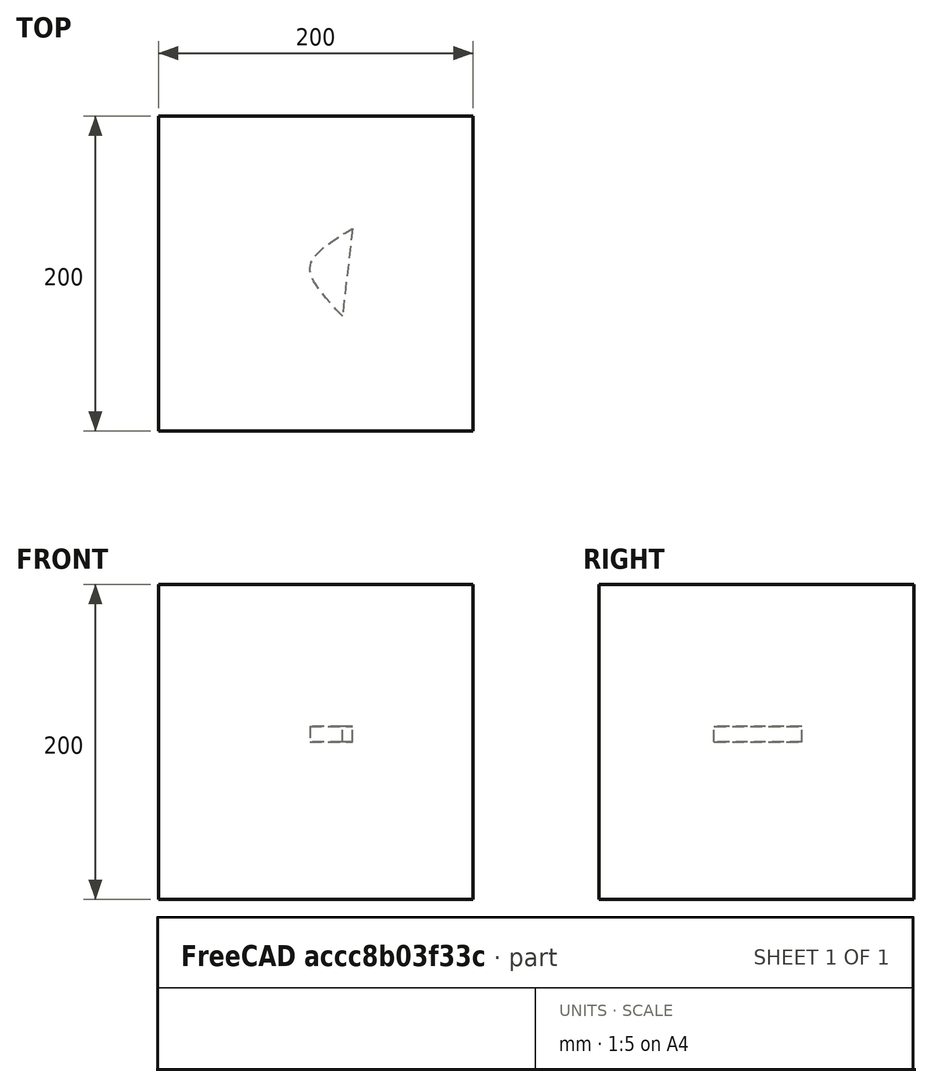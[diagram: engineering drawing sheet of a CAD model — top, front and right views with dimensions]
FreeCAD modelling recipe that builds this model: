
FCSTD DOCUMENT  (FreeCAD 0.21R33694 (Git))
Label: extrudedHyperbola
License: All rights reserved
LicenseURL: http://en.wikipedia.org/wiki/All_rights_reserved
objects: App::DocumentObjectGroupPython×1248, App::Part×2, Part::FeaturePython×1, Sketcher::SketchObject×1, Part::Extrusion×1
note: 3 computed .brp shape members not serialized (recipe doc carries the construction recipe); baked Part::Feature solids carry a one-line shape summary decoded from their .brp

FEATURE [App::DocumentObjectGroupPython] HALFPI  # scripted group (container) (typed FeaturePython)
  name = HALFPI
  value = pi/2.
FEATURE [App::DocumentObjectGroupPython] PI  # scripted group (container) (typed FeaturePython)
  name = PI
  value = 1.*pi
FEATURE [App::DocumentObjectGroupPython] TWOPI  # scripted group (container) (typed FeaturePython)
  name = TWOPI
  value = 2.*pi
FEATURE [App::DocumentObjectGroupPython] Constants  # scripted group (container) (typed FeaturePython)
  Group = -> [HALFPI,PI,TWOPI]
FEATURE [App::DocumentObjectGroupPython] Variables  # scripted group (container) (typed FeaturePython)
FEATURE [App::DocumentObjectGroupPython] Quantities  # scripted group (container) (typed FeaturePython)
FEATURE [App::DocumentObjectGroupPython] Isotopes  # scripted group (container) (typed FeaturePython)
FEATURE [App::DocumentObjectGroupPython] Elements  # scripted group (container) (typed FeaturePython)
FEATURE [App::DocumentObjectGroupPython] G4Isotopes  # scripted group (container) (typed FeaturePython)
FEATURE [App::DocumentObjectGroupPython] H_element  # scripted group (container) (typed FeaturePython)
  Z = 1
  atom_value = 1.008
  formula = H
  name = H_element
FEATURE [App::DocumentObjectGroupPython] He_element  # scripted group (container) (typed FeaturePython)
  Z = 2
  atom_value = 4.0026
  formula = He
  name = He_element
FEATURE [App::DocumentObjectGroupPython] Li_element  # scripted group (container) (typed FeaturePython)
  Z = 3
  atom_value = 6.94
  formula = Li
  name = Li_element
FEATURE [App::DocumentObjectGroupPython] Be_element  # scripted group (container) (typed FeaturePython)
  Z = 4
  atom_value = 9.01218
  formula = Be
  name = Be_element
FEATURE [App::DocumentObjectGroupPython] B_element  # scripted group (container) (typed FeaturePython)
  Z = 5
  atom_value = 10.81
  formula = B
  name = B_element
FEATURE [App::DocumentObjectGroupPython] C_element  # scripted group (container) (typed FeaturePython)
  Z = 6
  atom_value = 12.011
  formula = C
  name = C_element
FEATURE [App::DocumentObjectGroupPython] N_element  # scripted group (container) (typed FeaturePython)
  Z = 7
  atom_value = 14.007
  formula = N
  name = N_element
FEATURE [App::DocumentObjectGroupPython] O_element  # scripted group (container) (typed FeaturePython)
  Z = 8
  atom_value = 15.999
  formula = O
  name = O_element
FEATURE [App::DocumentObjectGroupPython] F_element  # scripted group (container) (typed FeaturePython)
  Z = 9
  atom_value = 18.9984
  formula = F
  name = F_element
FEATURE [App::DocumentObjectGroupPython] Ne_element  # scripted group (container) (typed FeaturePython)
  Z = 10
  atom_value = 20.1797
  formula = Ne
  name = Ne_element
FEATURE [App::DocumentObjectGroupPython] Na_element  # scripted group (container) (typed FeaturePython)
  Z = 11
  atom_value = 22.9898
  formula = Na
  name = Na_element
FEATURE [App::DocumentObjectGroupPython] Mg_element  # scripted group (container) (typed FeaturePython)
  Z = 12
  atom_value = 24.305
  formula = Mg
  name = Mg_element
FEATURE [App::DocumentObjectGroupPython] Al_element  # scripted group (container) (typed FeaturePython)
  Z = 13
  atom_value = 26.9815
  formula = Al
  name = Al_element
FEATURE [App::DocumentObjectGroupPython] Si_element  # scripted group (container) (typed FeaturePython)
  Z = 14
  atom_value = 28.085
  formula = Si
  name = Si_element
FEATURE [App::DocumentObjectGroupPython] P_element  # scripted group (container) (typed FeaturePython)
  Z = 15
  atom_value = 30.9738
  formula = P
  name = P_element
FEATURE [App::DocumentObjectGroupPython] S_element  # scripted group (container) (typed FeaturePython)
  Z = 16
  atom_value = 32.06
  formula = S
  name = S_element
FEATURE [App::DocumentObjectGroupPython] Cl_element  # scripted group (container) (typed FeaturePython)
  Z = 17
  atom_value = 35.45
  formula = Cl
  name = Cl_element
FEATURE [App::DocumentObjectGroupPython] Ar_element  # scripted group (container) (typed FeaturePython)
  Z = 18
  atom_value = 39.95
  formula = Ar
  name = Ar_element
FEATURE [App::DocumentObjectGroupPython] K_element  # scripted group (container) (typed FeaturePython)
  Z = 19
  atom_value = 39.0983
  formula = K
  name = K_element
FEATURE [App::DocumentObjectGroupPython] Ca_element  # scripted group (container) (typed FeaturePython)
  Z = 20
  atom_value = 40.078
  formula = Ca
  name = Ca_element
FEATURE [App::DocumentObjectGroupPython] Sc_element  # scripted group (container) (typed FeaturePython)
  Z = 21
  atom_value = 44.9559
  formula = Sc
  name = Sc_element
FEATURE [App::DocumentObjectGroupPython] Ti_element  # scripted group (container) (typed FeaturePython)
  Z = 22
  atom_value = 47.867
  formula = Ti
  name = Ti_element
FEATURE [App::DocumentObjectGroupPython] V_element  # scripted group (container) (typed FeaturePython)
  Z = 23
  atom_value = 50.9415
  formula = V
  name = V_element
FEATURE [App::DocumentObjectGroupPython] Cr_element  # scripted group (container) (typed FeaturePython)
  Z = 24
  atom_value = 51.9961
  formula = Cr
  name = Cr_element
FEATURE [App::DocumentObjectGroupPython] Mn_element  # scripted group (container) (typed FeaturePython)
  Z = 25
  atom_value = 54.938
  formula = Mn
  name = Mn_element
FEATURE [App::DocumentObjectGroupPython] Fe_element  # scripted group (container) (typed FeaturePython)
  Z = 26
  atom_value = 55.845
  formula = Fe
  name = Fe_element
FEATURE [App::DocumentObjectGroupPython] Co_element  # scripted group (container) (typed FeaturePython)
  Z = 27
  atom_value = 58.9332
  formula = Co
  name = Co_element
FEATURE [App::DocumentObjectGroupPython] Ni_element  # scripted group (container) (typed FeaturePython)
  Z = 28
  atom_value = 58.6934
  formula = Ni
  name = Ni_element
FEATURE [App::DocumentObjectGroupPython] Cu_element  # scripted group (container) (typed FeaturePython)
  Z = 29
  atom_value = 63.546
  formula = Cu
  name = Cu_element
FEATURE [App::DocumentObjectGroupPython] Zn_element  # scripted group (container) (typed FeaturePython)
  Z = 30
  atom_value = 65.38
  formula = Zn
  name = Zn_element
FEATURE [App::DocumentObjectGroupPython] Ga_element  # scripted group (container) (typed FeaturePython)
  Z = 31
  atom_value = 69.723
  formula = Ga
  name = Ga_element
FEATURE [App::DocumentObjectGroupPython] Ge_element  # scripted group (container) (typed FeaturePython)
  Z = 32
  atom_value = 72.63
  formula = Ge
  name = Ge_element
FEATURE [App::DocumentObjectGroupPython] As_element  # scripted group (container) (typed FeaturePython)
  Z = 33
  atom_value = 74.9216
  formula = As
  name = As_element
FEATURE [App::DocumentObjectGroupPython] Se_element  # scripted group (container) (typed FeaturePython)
  Z = 34
  atom_value = 78.971
  formula = Se
  name = Se_element
FEATURE [App::DocumentObjectGroupPython] Br_element  # scripted group (container) (typed FeaturePython)
  Z = 35
  atom_value = 79.904
  formula = Br
  name = Br_element
FEATURE [App::DocumentObjectGroupPython] Kr_element  # scripted group (container) (typed FeaturePython)
  Z = 36
  atom_value = 83.798
  formula = Kr
  name = Kr_element
FEATURE [App::DocumentObjectGroupPython] Rb_element  # scripted group (container) (typed FeaturePython)
  Z = 37
  atom_value = 85.4678
  formula = Rb
  name = Rb_element
FEATURE [App::DocumentObjectGroupPython] Sr_element  # scripted group (container) (typed FeaturePython)
  Z = 38
  atom_value = 87.62
  formula = Sr
  name = Sr_element
FEATURE [App::DocumentObjectGroupPython] Y_element  # scripted group (container) (typed FeaturePython)
  Z = 39
  atom_value = 88.9058
  formula = Y
  name = Y_element
FEATURE [App::DocumentObjectGroupPython] Zr_element  # scripted group (container) (typed FeaturePython)
  Z = 40
  atom_value = 91.224
  formula = Zr
  name = Zr_element
FEATURE [App::DocumentObjectGroupPython] Nb_element  # scripted group (container) (typed FeaturePython)
  Z = 41
  atom_value = 92.9064
  formula = Nb
  name = Nb_element
FEATURE [App::DocumentObjectGroupPython] Mo_element  # scripted group (container) (typed FeaturePython)
  Z = 42
  atom_value = 95.95
  formula = Mo
  name = Mo_element
FEATURE [App::DocumentObjectGroupPython] Tc_element  # scripted group (container) (typed FeaturePython)
  Z = 43
  atom_value = 97
  formula = Tc
  name = Tc_element
FEATURE [App::DocumentObjectGroupPython] Ru_element  # scripted group (container) (typed FeaturePython)
  Z = 44
  atom_value = 101.07
  formula = Ru
  name = Ru_element
FEATURE [App::DocumentObjectGroupPython] Rh_element  # scripted group (container) (typed FeaturePython)
  Z = 45
  atom_value = 102.905
  formula = Rh
  name = Rh_element
FEATURE [App::DocumentObjectGroupPython] Pd_element  # scripted group (container) (typed FeaturePython)
  Z = 46
  atom_value = 106.42
  formula = Pd
  name = Pd_element
FEATURE [App::DocumentObjectGroupPython] Ag_element  # scripted group (container) (typed FeaturePython)
  Z = 47
  atom_value = 107.868
  formula = Ag
  name = Ag_element
FEATURE [App::DocumentObjectGroupPython] Cd_element  # scripted group (container) (typed FeaturePython)
  Z = 48
  atom_value = 112.414
  formula = Cd
  name = Cd_element
FEATURE [App::DocumentObjectGroupPython] In_element  # scripted group (container) (typed FeaturePython)
  Z = 49
  atom_value = 114.818
  formula = In
  name = In_element
FEATURE [App::DocumentObjectGroupPython] Sn_element  # scripted group (container) (typed FeaturePython)
  Z = 50
  atom_value = 118.71
  formula = Sn
  name = Sn_element
FEATURE [App::DocumentObjectGroupPython] Sb_element  # scripted group (container) (typed FeaturePython)
  Z = 51
  atom_value = 121.76
  formula = Sb
  name = Sb_element
FEATURE [App::DocumentObjectGroupPython] Te_element  # scripted group (container) (typed FeaturePython)
  Z = 52
  atom_value = 127.6
  formula = Te
  name = Te_element
FEATURE [App::DocumentObjectGroupPython] I_element  # scripted group (container) (typed FeaturePython)
  Z = 53
  atom_value = 126.904
  formula = I
  name = I_element
FEATURE [App::DocumentObjectGroupPython] Xe_element  # scripted group (container) (typed FeaturePython)
  Z = 54
  atom_value = 131.293
  formula = Xe
  name = Xe_element
FEATURE [App::DocumentObjectGroupPython] Cs_element  # scripted group (container) (typed FeaturePython)
  Z = 55
  atom_value = 132.905
  formula = Cs
  name = Cs_element
FEATURE [App::DocumentObjectGroupPython] Ba_element  # scripted group (container) (typed FeaturePython)
  Z = 56
  atom_value = 137.327
  formula = Ba
  name = Ba_element
FEATURE [App::DocumentObjectGroupPython] La_element  # scripted group (container) (typed FeaturePython)
  Z = 57
  atom_value = 138.905
  formula = La
  name = La_element
FEATURE [App::DocumentObjectGroupPython] Ce_element  # scripted group (container) (typed FeaturePython)
  Z = 58
  atom_value = 140.116
  formula = Ce
  name = Ce_element
FEATURE [App::DocumentObjectGroupPython] Pr_element  # scripted group (container) (typed FeaturePython)
  Z = 59
  atom_value = 140.908
  formula = Pr
  name = Pr_element
FEATURE [App::DocumentObjectGroupPython] Nd_element  # scripted group (container) (typed FeaturePython)
  Z = 60
  atom_value = 144.242
  formula = Nd
  name = Nd_element
FEATURE [App::DocumentObjectGroupPython] Pm_element  # scripted group (container) (typed FeaturePython)
  Z = 61
  atom_value = 145
  formula = Pm
  name = Pm_element
FEATURE [App::DocumentObjectGroupPython] Sm_element  # scripted group (container) (typed FeaturePython)
  Z = 62
  atom_value = 150.36
  formula = Sm
  name = Sm_element
FEATURE [App::DocumentObjectGroupPython] Eu_element  # scripted group (container) (typed FeaturePython)
  Z = 63
  atom_value = 151.964
  formula = Eu
  name = Eu_element
FEATURE [App::DocumentObjectGroupPython] Gd_element  # scripted group (container) (typed FeaturePython)
  Z = 64
  atom_value = 157.25
  formula = Gd
  name = Gd_element
FEATURE [App::DocumentObjectGroupPython] Tb_element  # scripted group (container) (typed FeaturePython)
  Z = 65
  atom_value = 158.925
  formula = Tb
  name = Tb_element
FEATURE [App::DocumentObjectGroupPython] Dy_element  # scripted group (container) (typed FeaturePython)
  Z = 66
  atom_value = 162.5
  formula = Dy
  name = Dy_element
FEATURE [App::DocumentObjectGroupPython] Ho_element  # scripted group (container) (typed FeaturePython)
  Z = 67
  atom_value = 164.93
  formula = Ho
  name = Ho_element
FEATURE [App::DocumentObjectGroupPython] Er_element  # scripted group (container) (typed FeaturePython)
  Z = 68
  atom_value = 167.259
  formula = Er
  name = Er_element
FEATURE [App::DocumentObjectGroupPython] Tm_element  # scripted group (container) (typed FeaturePython)
  Z = 69
  atom_value = 168.934
  formula = Tm
  name = Tm_element
FEATURE [App::DocumentObjectGroupPython] Yb_element  # scripted group (container) (typed FeaturePython)
  Z = 70
  atom_value = 173.045
  formula = Yb
  name = Yb_element
FEATURE [App::DocumentObjectGroupPython] Lu_element  # scripted group (container) (typed FeaturePython)
  Z = 71
  atom_value = 174.967
  formula = Lu
  name = Lu_element
FEATURE [App::DocumentObjectGroupPython] Hf_element  # scripted group (container) (typed FeaturePython)
  Z = 72
  atom_value = 178.49
  formula = Hf
  name = Hf_element
FEATURE [App::DocumentObjectGroupPython] Ta_element  # scripted group (container) (typed FeaturePython)
  Z = 73
  atom_value = 180.948
  formula = Ta
  name = Ta_element
FEATURE [App::DocumentObjectGroupPython] W_element  # scripted group (container) (typed FeaturePython)
  Z = 74
  atom_value = 183.84
  formula = W
  name = W_element
FEATURE [App::DocumentObjectGroupPython] Re_element  # scripted group (container) (typed FeaturePython)
  Z = 75
  atom_value = 186.207
  formula = Re
  name = Re_element
FEATURE [App::DocumentObjectGroupPython] Os_element  # scripted group (container) (typed FeaturePython)
  Z = 76
  atom_value = 190.23
  formula = Os
  name = Os_element
FEATURE [App::DocumentObjectGroupPython] Ir_element  # scripted group (container) (typed FeaturePython)
  Z = 77
  atom_value = 192.217
  formula = Ir
  name = Ir_element
FEATURE [App::DocumentObjectGroupPython] Pt_element  # scripted group (container) (typed FeaturePython)
  Z = 78
  atom_value = 195.084
  formula = Pt
  name = Pt_element
FEATURE [App::DocumentObjectGroupPython] Au_element  # scripted group (container) (typed FeaturePython)
  Z = 79
  atom_value = 196.967
  formula = Au
  name = Au_element
FEATURE [App::DocumentObjectGroupPython] Hg_element  # scripted group (container) (typed FeaturePython)
  Z = 80
  atom_value = 200.592
  formula = Hg
  name = Hg_element
FEATURE [App::DocumentObjectGroupPython] Tl_element  # scripted group (container) (typed FeaturePython)
  Z = 81
  atom_value = 204.38
  formula = Tl
  name = Tl_element
FEATURE [App::DocumentObjectGroupPython] Pb_element  # scripted group (container) (typed FeaturePython)
  Z = 82
  atom_value = 207.2
  formula = Pb
  name = Pb_element
FEATURE [App::DocumentObjectGroupPython] Bi_element  # scripted group (container) (typed FeaturePython)
  Z = 83
  atom_value = 208.98
  formula = Bi
  name = Bi_element
FEATURE [App::DocumentObjectGroupPython] Po_element  # scripted group (container) (typed FeaturePython)
  Z = 84
  atom_value = 209
  formula = Po
  name = Po_element
FEATURE [App::DocumentObjectGroupPython] At_element  # scripted group (container) (typed FeaturePython)
  Z = 85
  atom_value = 210
  formula = At
  name = At_element
FEATURE [App::DocumentObjectGroupPython] Rn_element  # scripted group (container) (typed FeaturePython)
  Z = 86
  atom_value = 222
  formula = Rn
  name = Rn_element
FEATURE [App::DocumentObjectGroupPython] Fr_element  # scripted group (container) (typed FeaturePython)
  Z = 87
  atom_value = 223
  formula = Fr
  name = Fr_element
FEATURE [App::DocumentObjectGroupPython] Ra_element  # scripted group (container) (typed FeaturePython)
  Z = 88
  atom_value = 226
  formula = Ra
  name = Ra_element
FEATURE [App::DocumentObjectGroupPython] Ac_element  # scripted group (container) (typed FeaturePython)
  Z = 89
  atom_value = 227
  formula = Ac
  name = Ac_element
FEATURE [App::DocumentObjectGroupPython] Th_element  # scripted group (container) (typed FeaturePython)
  Z = 90
  atom_value = 232.038
  formula = Th
  name = Th_element
FEATURE [App::DocumentObjectGroupPython] Pa_element  # scripted group (container) (typed FeaturePython)
  Z = 91
  atom_value = 231.036
  formula = Pa
  name = Pa_element
FEATURE [App::DocumentObjectGroupPython] U_element  # scripted group (container) (typed FeaturePython)
  Z = 92
  atom_value = 238.029
  formula = U
  name = U_element
FEATURE [App::DocumentObjectGroupPython] Np_element  # scripted group (container) (typed FeaturePython)
  Z = 93
  atom_value = 237
  formula = Np
  name = Np_element
FEATURE [App::DocumentObjectGroupPython] Pu_element  # scripted group (container) (typed FeaturePython)
  Z = 94
  atom_value = 244
  formula = Pu
  name = Pu_element
FEATURE [App::DocumentObjectGroupPython] Am_element  # scripted group (container) (typed FeaturePython)
  Z = 95
  atom_value = 243
  formula = Am
  name = Am_element
FEATURE [App::DocumentObjectGroupPython] Cm_element  # scripted group (container) (typed FeaturePython)
  Z = 96
  atom_value = 247
  formula = Cm
  name = Cm_element
FEATURE [App::DocumentObjectGroupPython] Bk_element  # scripted group (container) (typed FeaturePython)
  Z = 97
  atom_value = 247
  formula = Bk
  name = Bk_element
FEATURE [App::DocumentObjectGroupPython] Cf_element  # scripted group (container) (typed FeaturePython)
  Z = 98
  atom_value = 251
  formula = Cf
  name = Cf_element
FEATURE [App::DocumentObjectGroupPython] G4Elements  # scripted group (container) (typed FeaturePython)
  Group = -> [H_element,He_element,Li_element,Be_element,B_element,C_element,N_element,O_element,F_element,Ne_element,Na_element,Mg_element,Al_element,Si_element,P_element,S_element,Cl_element,Ar_element,K_element,Ca_element,Sc_element,Ti_element,V_element,Cr_element,Mn_element,Fe_element,Co_element,Ni_element,Cu_element,Zn_element,Ga_element,Ge_element,As_element,Se_element,Br_element,Kr_element,Rb_element,+61 more]
FEATURE [App::DocumentObjectGroupPython] H_element001  label="H_element : 0.101"  # scripted group (container) (typed FeaturePython)
  n = 0.101327
FEATURE [App::DocumentObjectGroupPython] C_element001  label="C_element : 0.775"  # scripted group (container) (typed FeaturePython)
  n = 0.7755
FEATURE [App::DocumentObjectGroupPython] N_element001  label="N_element : 0.035"  # scripted group (container) (typed FeaturePython)
  n = 0.035057
FEATURE [App::DocumentObjectGroupPython] O_element001  label="O_element : 0.052"  # scripted group (container) (typed FeaturePython)
  n = 0.0523159
FEATURE [App::DocumentObjectGroupPython] F_element001  label="F_element : 0.017"  # scripted group (container) (typed FeaturePython)
  n = 0.017422
FEATURE [App::DocumentObjectGroupPython] Ca_element001  label="Ca_element : 0.018"  # scripted group (container) (typed FeaturePython)
  n = 0.018378
FEATURE [App::DocumentObjectGroupPython] G4_A_150_TISSUE  label="G4_A-150_TISSUE"  # scripted group (container) (typed FeaturePython)
  Dunit = g/cm3
  Dvalue = 1.127
  Group = -> [H_element001,C_element001,N_element001,O_element001,F_element001,Ca_element001]
  conduct = 2
  density = 1
  expand = 3
  formula = G4_A-150_TISSUE
  name = G4_A-150_TISSUE
  specific = 4
FEATURE [App::DocumentObjectGroupPython] C_element002  label="C_element : 3"  # scripted group (container) (typed FeaturePython)
  n = 3
  ref = C_element
FEATURE [App::DocumentObjectGroupPython] H_element002  label="H_element : 6"  # scripted group (container) (typed FeaturePython)
  n = 6
  ref = H_element
FEATURE [App::DocumentObjectGroupPython] O_element002  label="O_element : 1"  # scripted group (container) (typed FeaturePython)
  n = 1
  ref = O_element
FEATURE [App::DocumentObjectGroupPython] G4_ACETONE  # scripted group (container) (typed FeaturePython)
  Dunit = g/cm3
  Dvalue = 0.7899
  Group = -> [C_element002,H_element002,O_element002]
  conduct = 2
  density = 1
  expand = 3
  formula = G4_ACETONE
  name = G4_ACETONE
  specific = 4
FEATURE [App::DocumentObjectGroupPython] C_element003  label="C_element : 2"  # scripted group (container) (typed FeaturePython)
  n = 2
  ref = C_element
FEATURE [App::DocumentObjectGroupPython] H_element003  label="H_element : 2"  # scripted group (container) (typed FeaturePython)
  n = 2
  ref = H_element
FEATURE [App::DocumentObjectGroupPython] G4_ACETYLENE  # scripted group (container) (typed FeaturePython)
  Dunit = g/cm3
  Dvalue = 0.0010967
  Group = -> [C_element003,H_element003]
  conduct = 2
  density = 1
  expand = 3
  formula = G4_ACETYLENE
  name = G4_ACETYLENE
  specific = 4
FEATURE [App::DocumentObjectGroupPython] C_element004  label="C_element : 5"  # scripted group (container) (typed FeaturePython)
  n = 5
  ref = C_element
FEATURE [App::DocumentObjectGroupPython] H_element004  label="H_element : 5"  # scripted group (container) (typed FeaturePython)
  n = 5
  ref = H_element
FEATURE [App::DocumentObjectGroupPython] N_element002  label="N_element : 5"  # scripted group (container) (typed FeaturePython)
  n = 5
  ref = N_element
FEATURE [App::DocumentObjectGroupPython] G4_ADENINE  # scripted group (container) (typed FeaturePython)
  Dunit = g/cm3
  Dvalue = 1.6
  Group = -> [C_element004,H_element004,N_element002]
  conduct = 2
  density = 1
  expand = 3
  formula = G4_ADENINE
  name = G4_ADENINE
  specific = 4
FEATURE [App::DocumentObjectGroupPython] H_element005  label="H_element : 0.114"  # scripted group (container) (typed FeaturePython)
  n = 0.114
FEATURE [App::DocumentObjectGroupPython] C_element005  label="C_element : 0.598"  # scripted group (container) (typed FeaturePython)
  n = 0.598
FEATURE [App::DocumentObjectGroupPython] N_element003  label="N_element : 0.007"  # scripted group (container) (typed FeaturePython)
  n = 0.007
FEATURE [App::DocumentObjectGroupPython] O_element003  label="O_element : 0.278"  # scripted group (container) (typed FeaturePython)
  n = 0.278
FEATURE [App::DocumentObjectGroupPython] Na_element001  label="Na_element : 0.001"  # scripted group (container) (typed FeaturePython)
  n = 0.001
FEATURE [App::DocumentObjectGroupPython] S_element001  label="S_element : 0.001"  # scripted group (container) (typed FeaturePython)
  n = 0.001
FEATURE [App::DocumentObjectGroupPython] Cl_element001  label="Cl_element : 0.001"  # scripted group (container) (typed FeaturePython)
  n = 0.001
FEATURE [App::DocumentObjectGroupPython] G4_ADIPOSE_TISSUE_ICRP  # scripted group (container) (typed FeaturePython)
  Dunit = g/cm3
  Dvalue = 0.95
  Group = -> [H_element005,C_element005,N_element003,O_element003,Na_element001,S_element001,Cl_element001]
  conduct = 2
  density = 1
  expand = 3
  formula = G4_ADIPOSE_TISSUE_ICRP
  name = G4_ADIPOSE_TISSUE_ICRP
  specific = 4
FEATURE [App::DocumentObjectGroupPython] C_element006  label="C_element : 0.000"  # scripted group (container) (typed FeaturePython)
  n = 0.000124
FEATURE [App::DocumentObjectGroupPython] N_element004  label="N_element : 0.755"  # scripted group (container) (typed FeaturePython)
  n = 0.755268
FEATURE [App::DocumentObjectGroupPython] O_element004  label="O_element : 0.232"  # scripted group (container) (typed FeaturePython)
  n = 0.231781
FEATURE [App::DocumentObjectGroupPython] Ar_element001  label="Ar_element : 0.013"  # scripted group (container) (typed FeaturePython)
  n = 0.012827
FEATURE [App::DocumentObjectGroupPython] G4_AIR  # scripted group (container) (typed FeaturePython)
  Dunit = g/cm3
  Dvalue = 0.00120479
  Group = -> [C_element006,N_element004,O_element004,Ar_element001]
  conduct = 2
  density = 1
  expand = 3
  formula = G4_AIR
  name = G4_AIR
  specific = 4
FEATURE [App::DocumentObjectGroupPython] C_element007  label="C_element : 006"  # scripted group (container) (typed FeaturePython)
  n = 3
  ref = C_element
FEATURE [App::DocumentObjectGroupPython] H_element006  label="H_element : 7"  # scripted group (container) (typed FeaturePython)
  n = 7
  ref = H_element
FEATURE [App::DocumentObjectGroupPython] N_element005  label="N_element : 1"  # scripted group (container) (typed FeaturePython)
  n = 1
  ref = N_element
FEATURE [App::DocumentObjectGroupPython] O_element005  label="O_element : 2"  # scripted group (container) (typed FeaturePython)
  n = 2
  ref = O_element
FEATURE [App::DocumentObjectGroupPython] G4_ALANINE  # scripted group (container) (typed FeaturePython)
  Dunit = g/cm3
  Dvalue = 1.42
  Group = -> [C_element007,H_element006,N_element005,O_element005]
  conduct = 2
  density = 1
  expand = 3
  formula = G4_ALANINE
  name = G4_ALANINE
  specific = 4
FEATURE [App::DocumentObjectGroupPython] Al_element001  label="Al_element : 2"  # scripted group (container) (typed FeaturePython)
  n = 2
  ref = Al_element
FEATURE [App::DocumentObjectGroupPython] O_element006  label="O_element : 3"  # scripted group (container) (typed FeaturePython)
  n = 3
  ref = O_element
FEATURE [App::DocumentObjectGroupPython] G4_ALUMINUM_OXIDE  # scripted group (container) (typed FeaturePython)
  Dunit = g/cm3
  Dvalue = 3.97
  Group = -> [Al_element001,O_element006]
  conduct = 2
  density = 1
  expand = 3
  formula = G4_ALUMINUM_OXIDE
  name = G4_ALUMINUM_OXIDE
  specific = 4
FEATURE [App::DocumentObjectGroupPython] H_element007  label="H_element : 0.106"  # scripted group (container) (typed FeaturePython)
  n = 0.10593
FEATURE [App::DocumentObjectGroupPython] C_element008  label="C_element : 0.789"  # scripted group (container) (typed FeaturePython)
  n = 0.788974
FEATURE [App::DocumentObjectGroupPython] O_element007  label="O_element : 0.105"  # scripted group (container) (typed FeaturePython)
  n = 0.105096
FEATURE [App::DocumentObjectGroupPython] G4_AMBER  # scripted group (container) (typed FeaturePython)
  Dunit = g/cm3
  Dvalue = 1.1
  Group = -> [H_element007,C_element008,O_element007]
  conduct = 2
  density = 1
  expand = 3
  formula = G4_AMBER
  name = G4_AMBER
  specific = 4
FEATURE [App::DocumentObjectGroupPython] N_element006  label="N_element : 006"  # scripted group (container) (typed FeaturePython)
  n = 1
  ref = N_element
FEATURE [App::DocumentObjectGroupPython] H_element008  label="H_element : 3"  # scripted group (container) (typed FeaturePython)
  n = 3
  ref = H_element
FEATURE [App::DocumentObjectGroupPython] G4_AMMONIA  # scripted group (container) (typed FeaturePython)
  Dunit = g/cm3
  Dvalue = 0.000826019
  Group = -> [N_element006,H_element008]
  conduct = 2
  density = 1
  expand = 3
  formula = G4_AMMONIA
  name = G4_AMMONIA
  specific = 4
FEATURE [App::DocumentObjectGroupPython] C_element009  label="C_element : 6"  # scripted group (container) (typed FeaturePython)
  n = 6
  ref = C_element
FEATURE [App::DocumentObjectGroupPython] H_element009  label="H_element : 008"  # scripted group (container) (typed FeaturePython)
  n = 7
  ref = H_element
FEATURE [App::DocumentObjectGroupPython] N_element007  label="N_element : 007"  # scripted group (container) (typed FeaturePython)
  n = 1
  ref = N_element
FEATURE [App::DocumentObjectGroupPython] G4_ANILINE  # scripted group (container) (typed FeaturePython)
  Dunit = g/cm3
  Dvalue = 1.0235
  Group = -> [C_element009,H_element009,N_element007]
  conduct = 2
  density = 1
  expand = 3
  formula = G4_ANILINE
  name = G4_ANILINE
  specific = 4
FEATURE [App::DocumentObjectGroupPython] C_element010  label="C_element : 14"  # scripted group (container) (typed FeaturePython)
  n = 14
  ref = C_element
FEATURE [App::DocumentObjectGroupPython] H_element010  label="H_element : 10"  # scripted group (container) (typed FeaturePython)
  n = 10
  ref = H_element
FEATURE [App::DocumentObjectGroupPython] G4_ANTHRACENE  # scripted group (container) (typed FeaturePython)
  Dunit = g/cm3
  Dvalue = 1.283
  Group = -> [C_element010,H_element010]
  conduct = 2
  density = 1
  expand = 3
  formula = G4_ANTHRACENE
  name = G4_ANTHRACENE
  specific = 4
FEATURE [App::DocumentObjectGroupPython] H_element011  label="H_element : 0.065"  # scripted group (container) (typed FeaturePython)
  n = 0.0654709
FEATURE [App::DocumentObjectGroupPython] C_element011  label="C_element : 0.537"  # scripted group (container) (typed FeaturePython)
  n = 0.536944
FEATURE [App::DocumentObjectGroupPython] N_element008  label="N_element : 0.021"  # scripted group (container) (typed FeaturePython)
  n = 0.0215
FEATURE [App::DocumentObjectGroupPython] O_element008  label="O_element : 0.032"  # scripted group (container) (typed FeaturePython)
  n = 0.032085
FEATURE [App::DocumentObjectGroupPython] F_element002  label="F_element : 0.167"  # scripted group (container) (typed FeaturePython)
  n = 0.167411
FEATURE [App::DocumentObjectGroupPython] Ca_element002  label="Ca_element : 0.177"  # scripted group (container) (typed FeaturePython)
  n = 0.176589
FEATURE [App::DocumentObjectGroupPython] G4_B_100_BONE  label="G4_B-100_BONE"  # scripted group (container) (typed FeaturePython)
  Dunit = g/cm3
  Dvalue = 1.45
  Group = -> [H_element011,C_element011,N_element008,O_element008,F_element002,Ca_element002]
  conduct = 2
  density = 1
  expand = 3
  formula = G4_B-100_BONE
  name = G4_B-100_BONE
  specific = 4
FEATURE [App::DocumentObjectGroupPython] H_element012  label="H_element : 0.057"  # scripted group (container) (typed FeaturePython)
  n = 0.057441
FEATURE [App::DocumentObjectGroupPython] C_element012  label="C_element : 0.790"  # scripted group (container) (typed FeaturePython)
  n = 0.774591
FEATURE [App::DocumentObjectGroupPython] O_element009  label="O_element : 0.168"  # scripted group (container) (typed FeaturePython)
  n = 0.167968
FEATURE [App::DocumentObjectGroupPython] G4_BAKELITE  # scripted group (container) (typed FeaturePython)
  Dunit = g/cm3
  Dvalue = 1.25
  Group = -> [H_element012,C_element012,O_element009]
  conduct = 2
  density = 1
  expand = 3
  formula = G4_BAKELITE
  name = G4_BAKELITE
  specific = 4
FEATURE [App::DocumentObjectGroupPython] Ba_element001  label="Ba_element : 1"  # scripted group (container) (typed FeaturePython)
  n = 1
  ref = Ba_element
FEATURE [App::DocumentObjectGroupPython] F_element003  label="F_element : 2"  # scripted group (container) (typed FeaturePython)
  n = 2
  ref = F_element
FEATURE [App::DocumentObjectGroupPython] G4_BARIUM_FLUORIDE  # scripted group (container) (typed FeaturePython)
  Dunit = g/cm3
  Dvalue = 4.89
  Group = -> [Ba_element001,F_element003]
  conduct = 2
  density = 1
  expand = 3
  formula = G4_BARIUM_FLUORIDE
  name = G4_BARIUM_FLUORIDE
  specific = 4
FEATURE [App::DocumentObjectGroupPython] Ba_element002  label="Ba_element : 002"  # scripted group (container) (typed FeaturePython)
  n = 1
  ref = Ba_element
FEATURE [App::DocumentObjectGroupPython] S_element002  label="S_element : 1"  # scripted group (container) (typed FeaturePython)
  n = 1
  ref = S_element
FEATURE [App::DocumentObjectGroupPython] O_element010  label="O_element : 4"  # scripted group (container) (typed FeaturePython)
  n = 4
  ref = O_element
FEATURE [App::DocumentObjectGroupPython] G4_BARIUM_SULFATE  # scripted group (container) (typed FeaturePython)
  Dunit = g/cm3
  Dvalue = 4.5
  Group = -> [Ba_element002,S_element002,O_element010]
  conduct = 2
  density = 1
  expand = 3
  formula = G4_BARIUM_SULFATE
  name = G4_BARIUM_SULFATE
  specific = 4
FEATURE [App::DocumentObjectGroupPython] C_element013  label="C_element : 007"  # scripted group (container) (typed FeaturePython)
  n = 6
  ref = C_element
FEATURE [App::DocumentObjectGroupPython] H_element013  label="H_element : 009"  # scripted group (container) (typed FeaturePython)
  n = 6
  ref = H_element
FEATURE [App::DocumentObjectGroupPython] G4_BENZENE  # scripted group (container) (typed FeaturePython)
  Dunit = g/cm3
  Dvalue = 0.87865
  Group = -> [C_element013,H_element013]
  conduct = 2
  density = 1
  expand = 3
  formula = G4_BENZENE
  name = G4_BENZENE
  specific = 4
FEATURE [App::DocumentObjectGroupPython] Be_element001  label="Be_element : 1"  # scripted group (container) (typed FeaturePython)
  n = 1
  ref = Be_element
FEATURE [App::DocumentObjectGroupPython] O_element011  label="O_element : 005"  # scripted group (container) (typed FeaturePython)
  n = 1
  ref = O_element
FEATURE [App::DocumentObjectGroupPython] G4_BERYLLIUM_OXIDE  # scripted group (container) (typed FeaturePython)
  Dunit = g/cm3
  Dvalue = 3.01
  Group = -> [Be_element001,O_element011]
  conduct = 2
  density = 1
  expand = 3
  formula = G4_BERYLLIUM_OXIDE
  name = G4_BERYLLIUM_OXIDE
  specific = 4
FEATURE [App::DocumentObjectGroupPython] Bi_element001  label="Bi_element : 4"  # scripted group (container) (typed FeaturePython)
  n = 4
  ref = Bi_element
FEATURE [App::DocumentObjectGroupPython] Ge_element001  label="Ge_element : 3"  # scripted group (container) (typed FeaturePython)
  n = 3
  ref = Ge_element
FEATURE [App::DocumentObjectGroupPython] O_element012  label="O_element : 12"  # scripted group (container) (typed FeaturePython)
  n = 12
  ref = O_element
FEATURE [App::DocumentObjectGroupPython] G4_BGO  # scripted group (container) (typed FeaturePython)
  Dunit = g/cm3
  Dvalue = 7.13
  Group = -> [Bi_element001,Ge_element001,O_element012]
  conduct = 2
  density = 1
  expand = 3
  formula = G4_BGO
  name = G4_BGO
  specific = 4
FEATURE [App::DocumentObjectGroupPython] H_element014  label="H_element : 0.102"  # scripted group (container) (typed FeaturePython)
  n = 0.102
FEATURE [App::DocumentObjectGroupPython] C_element014  label="C_element : 0.110"  # scripted group (container) (typed FeaturePython)
  n = 0.11
FEATURE [App::DocumentObjectGroupPython] N_element009  label="N_element : 0.033"  # scripted group (container) (typed FeaturePython)
  n = 0.033
FEATURE [App::DocumentObjectGroupPython] O_element013  label="O_element : 0.745"  # scripted group (container) (typed FeaturePython)
  n = 0.745
FEATURE [App::DocumentObjectGroupPython] Na_element002  label="Na_element : 0.002"  # scripted group (container) (typed FeaturePython)
  n = 0.001
FEATURE [App::DocumentObjectGroupPython] P_element001  label="P_element : 0.001"  # scripted group (container) (typed FeaturePython)
  n = 0.001
FEATURE [App::DocumentObjectGroupPython] S_element003  label="S_element : 0.002"  # scripted group (container) (typed FeaturePython)
  n = 0.002
FEATURE [App::DocumentObjectGroupPython] Cl_element002  label="Cl_element : 0.003"  # scripted group (container) (typed FeaturePython)
  n = 0.003
FEATURE [App::DocumentObjectGroupPython] K_element001  label="K_element : 0.002"  # scripted group (container) (typed FeaturePython)
  n = 0.002
FEATURE [App::DocumentObjectGroupPython] Fe_element001  label="Fe_element : 0.001"  # scripted group (container) (typed FeaturePython)
  n = 0.001
FEATURE [App::DocumentObjectGroupPython] G4_BLOOD_ICRP  # scripted group (container) (typed FeaturePython)
  Dunit = g/cm3
  Dvalue = 1.06
  Group = -> [H_element014,C_element014,N_element009,O_element013,Na_element002,P_element001,S_element003,Cl_element002,K_element001,Fe_element001]
  conduct = 2
  density = 1
  expand = 3
  formula = G4_BLOOD_ICRP
  name = G4_BLOOD_ICRP
  specific = 4
FEATURE [App::DocumentObjectGroupPython] H_element015  label="H_element : 0.064"  # scripted group (container) (typed FeaturePython)
  n = 0.064
FEATURE [App::DocumentObjectGroupPython] C_element015  label="C_element : 0.278"  # scripted group (container) (typed FeaturePython)
  n = 0.278
FEATURE [App::DocumentObjectGroupPython] N_element010  label="N_element : 0.027"  # scripted group (container) (typed FeaturePython)
  n = 0.027
FEATURE [App::DocumentObjectGroupPython] O_element014  label="O_element : 0.410"  # scripted group (container) (typed FeaturePython)
  n = 0.41
FEATURE [App::DocumentObjectGroupPython] Mg_element001  label="Mg_element : 0.002"  # scripted group (container) (typed FeaturePython)
  n = 0.002
FEATURE [App::DocumentObjectGroupPython] P_element002  label="P_element : 0.070"  # scripted group (container) (typed FeaturePython)
  n = 0.07
FEATURE [App::DocumentObjectGroupPython] S_element004  label="S_element : 0.003"  # scripted group (container) (typed FeaturePython)
  n = 0.002
FEATURE [App::DocumentObjectGroupPython] Ca_element003  label="Ca_element : 0.147"  # scripted group (container) (typed FeaturePython)
  n = 0.147
FEATURE [App::DocumentObjectGroupPython] G4_BONE_COMPACT_ICRU  # scripted group (container) (typed FeaturePython)
  Dunit = g/cm3
  Dvalue = 1.85
  Group = -> [H_element015,C_element015,N_element010,O_element014,Mg_element001,P_element002,S_element004,Ca_element003]
  conduct = 2
  density = 1
  expand = 3
  formula = G4_BONE_COMPACT_ICRU
  name = G4_BONE_COMPACT_ICRU
  specific = 4
FEATURE [App::DocumentObjectGroupPython] H_element016  label="H_element : 0.034"  # scripted group (container) (typed FeaturePython)
  n = 0.034
FEATURE [App::DocumentObjectGroupPython] C_element016  label="C_element : 0.155"  # scripted group (container) (typed FeaturePython)
  n = 0.155
FEATURE [App::DocumentObjectGroupPython] N_element011  label="N_element : 0.042"  # scripted group (container) (typed FeaturePython)
  n = 0.042
FEATURE [App::DocumentObjectGroupPython] O_element015  label="O_element : 0.435"  # scripted group (container) (typed FeaturePython)
  n = 0.435
FEATURE [App::DocumentObjectGroupPython] Na_element003  label="Na_element : 0.003"  # scripted group (container) (typed FeaturePython)
  n = 0.001
FEATURE [App::DocumentObjectGroupPython] Mg_element002  label="Mg_element : 0.003"  # scripted group (container) (typed FeaturePython)
  n = 0.002
FEATURE [App::DocumentObjectGroupPython] P_element003  label="P_element : 0.103"  # scripted group (container) (typed FeaturePython)
  n = 0.103
FEATURE [App::DocumentObjectGroupPython] S_element005  label="S_element : 0.004"  # scripted group (container) (typed FeaturePython)
  n = 0.003
FEATURE [App::DocumentObjectGroupPython] Ca_element004  label="Ca_element : 0.225"  # scripted group (container) (typed FeaturePython)
  n = 0.225
FEATURE [App::DocumentObjectGroupPython] G4_BONE_CORTICAL_ICRP  # scripted group (container) (typed FeaturePython)
  Dunit = g/cm3
  Dvalue = 1.92
  Group = -> [H_element016,C_element016,N_element011,O_element015,Na_element003,Mg_element002,P_element003,S_element005,Ca_element004]
  conduct = 2
  density = 1
  expand = 3
  formula = G4_BONE_CORTICAL_ICRP
  name = G4_BONE_CORTICAL_ICRP
  specific = 4
FEATURE [App::DocumentObjectGroupPython] B_element001  label="B_element : 4"  # scripted group (container) (typed FeaturePython)
  n = 4
  ref = B_element
FEATURE [App::DocumentObjectGroupPython] C_element017  label="C_element : 1"  # scripted group (container) (typed FeaturePython)
  n = 1
  ref = C_element
FEATURE [App::DocumentObjectGroupPython] G4_BORON_CARBIDE  # scripted group (container) (typed FeaturePython)
  Dunit = g/cm3
  Dvalue = 2.52
  Group = -> [B_element001,C_element017]
  conduct = 2
  density = 1
  expand = 3
  formula = G4_BORON_CARBIDE
  name = G4_BORON_CARBIDE
  specific = 4
FEATURE [App::DocumentObjectGroupPython] B_element002  label="B_element : 2"  # scripted group (container) (typed FeaturePython)
  n = 2
  ref = B_element
FEATURE [App::DocumentObjectGroupPython] O_element016  label="O_element : 006"  # scripted group (container) (typed FeaturePython)
  n = 3
  ref = O_element
FEATURE [App::DocumentObjectGroupPython] G4_BORON_OXIDE  # scripted group (container) (typed FeaturePython)
  Dunit = g/cm3
  Dvalue = 1.812
  Group = -> [B_element002,O_element016]
  conduct = 2
  density = 1
  expand = 3
  formula = G4_BORON_OXIDE
  name = G4_BORON_OXIDE
  specific = 4
FEATURE [App::DocumentObjectGroupPython] H_element017  label="H_element : 0.107"  # scripted group (container) (typed FeaturePython)
  n = 0.107
FEATURE [App::DocumentObjectGroupPython] C_element018  label="C_element : 0.145"  # scripted group (container) (typed FeaturePython)
  n = 0.145
FEATURE [App::DocumentObjectGroupPython] N_element012  label="N_element : 0.022"  # scripted group (container) (typed FeaturePython)
  n = 0.022
FEATURE [App::DocumentObjectGroupPython] O_element017  label="O_element : 0.712"  # scripted group (container) (typed FeaturePython)
  n = 0.712
FEATURE [App::DocumentObjectGroupPython] Na_element004  label="Na_element : 0.004"  # scripted group (container) (typed FeaturePython)
  n = 0.002
FEATURE [App::DocumentObjectGroupPython] P_element004  label="P_element : 0.004"  # scripted group (container) (typed FeaturePython)
  n = 0.004
FEATURE [App::DocumentObjectGroupPython] S_element006  label="S_element : 0.005"  # scripted group (container) (typed FeaturePython)
  n = 0.002
FEATURE [App::DocumentObjectGroupPython] Cl_element003  label="Cl_element : 0.004"  # scripted group (container) (typed FeaturePython)
  n = 0.003
FEATURE [App::DocumentObjectGroupPython] K_element002  label="K_element : 0.003"  # scripted group (container) (typed FeaturePython)
  n = 0.003
FEATURE [App::DocumentObjectGroupPython] G4_BRAIN_ICRP  # scripted group (container) (typed FeaturePython)
  Dunit = g/cm3
  Dvalue = 1.04
  Group = -> [H_element017,C_element018,N_element012,O_element017,Na_element004,P_element004,S_element006,Cl_element003,K_element002]
  conduct = 2
  density = 1
  expand = 3
  formula = G4_BRAIN_ICRP
  name = G4_BRAIN_ICRP
  specific = 4
FEATURE [App::DocumentObjectGroupPython] C_element019  label="C_element : 4"  # scripted group (container) (typed FeaturePython)
  n = 4
  ref = C_element
FEATURE [App::DocumentObjectGroupPython] H_element018  label="H_element : 010"  # scripted group (container) (typed FeaturePython)
  n = 10
  ref = H_element
FEATURE [App::DocumentObjectGroupPython] G4_BUTANE  # scripted group (container) (typed FeaturePython)
  Dunit = g/cm3
  Dvalue = 0.00249343
  Group = -> [C_element019,H_element018]
  conduct = 2
  density = 1
  expand = 3
  formula = G4_BUTANE
  name = G4_BUTANE
  specific = 4
FEATURE [App::DocumentObjectGroupPython] C_element020  label="C_element : 008"  # scripted group (container) (typed FeaturePython)
  n = 4
  ref = C_element
FEATURE [App::DocumentObjectGroupPython] H_element019  label="H_element : 011"  # scripted group (container) (typed FeaturePython)
  n = 10
  ref = H_element
FEATURE [App::DocumentObjectGroupPython] O_element018  label="O_element : 007"  # scripted group (container) (typed FeaturePython)
  n = 1
  ref = O_element
FEATURE [App::DocumentObjectGroupPython] G4_N_BUTYL_ALCOHOL  label="G4_N-BUTYL_ALCOHOL"  # scripted group (container) (typed FeaturePython)
  Dunit = g/cm3
  Dvalue = 0.8098
  Group = -> [C_element020,H_element019,O_element018]
  conduct = 2
  density = 1
  expand = 3
  formula = G4_N-BUTYL_ALCOHOL
  name = G4_N-BUTYL_ALCOHOL
  specific = 4
FEATURE [App::DocumentObjectGroupPython] H_element020  label="H_element : 0.025"  # scripted group (container) (typed FeaturePython)
  n = 0.02468
FEATURE [App::DocumentObjectGroupPython] C_element021  label="C_element : 0.502"  # scripted group (container) (typed FeaturePython)
  n = 0.501611
FEATURE [App::DocumentObjectGroupPython] O_element019  label="O_element : 0.005"  # scripted group (container) (typed FeaturePython)
  n = 0.004527
FEATURE [App::DocumentObjectGroupPython] F_element004  label="F_element : 0.465"  # scripted group (container) (typed FeaturePython)
  n = 0.465209
FEATURE [App::DocumentObjectGroupPython] Si_element001  label="Si_element : 0.004"  # scripted group (container) (typed FeaturePython)
  n = 0.003973
FEATURE [App::DocumentObjectGroupPython] G4_C_552  label="G4_C-552"  # scripted group (container) (typed FeaturePython)
  Dunit = g/cm3
  Dvalue = 1.76
  Group = -> [H_element020,C_element021,O_element019,F_element004,Si_element001]
  conduct = 2
  density = 1
  expand = 3
  formula = G4_C-552
  name = G4_C-552
  specific = 4
FEATURE [App::DocumentObjectGroupPython] Cd_element001  label="Cd_element : 1"  # scripted group (container) (typed FeaturePython)
  n = 1
  ref = Cd_element
FEATURE [App::DocumentObjectGroupPython] Te_element001  label="Te_element : 1"  # scripted group (container) (typed FeaturePython)
  n = 1
  ref = Te_element
FEATURE [App::DocumentObjectGroupPython] G4_CADMIUM_TELLURIDE  # scripted group (container) (typed FeaturePython)
  Dunit = g/cm3
  Dvalue = 6.2
  Group = -> [Cd_element001,Te_element001]
  conduct = 2
  density = 1
  expand = 3
  formula = G4_CADMIUM_TELLURIDE
  name = G4_CADMIUM_TELLURIDE
  specific = 4
FEATURE [App::DocumentObjectGroupPython] Cd_element002  label="Cd_element : 002"  # scripted group (container) (typed FeaturePython)
  n = 1
  ref = Cd_element
FEATURE [App::DocumentObjectGroupPython] W_element001  label="W_element : 1"  # scripted group (container) (typed FeaturePython)
  n = 1
  ref = W_element
FEATURE [App::DocumentObjectGroupPython] O_element020  label="O_element : 008"  # scripted group (container) (typed FeaturePython)
  n = 4
  ref = O_element
FEATURE [App::DocumentObjectGroupPython] G4_CADMIUM_TUNGSTATE  # scripted group (container) (typed FeaturePython)
  Dunit = g/cm3
  Dvalue = 7.9
  Group = -> [Cd_element002,W_element001,O_element020]
  conduct = 2
  density = 1
  expand = 3
  formula = G4_CADMIUM_TUNGSTATE
  name = G4_CADMIUM_TUNGSTATE
  specific = 4
FEATURE [App::DocumentObjectGroupPython] Ca_element005  label="Ca_element : 1"  # scripted group (container) (typed FeaturePython)
  n = 1
  ref = Ca_element
FEATURE [App::DocumentObjectGroupPython] C_element022  label="C_element : 009"  # scripted group (container) (typed FeaturePython)
  n = 1
  ref = C_element
FEATURE [App::DocumentObjectGroupPython] O_element021  label="O_element : 009"  # scripted group (container) (typed FeaturePython)
  n = 3
  ref = O_element
FEATURE [App::DocumentObjectGroupPython] G4_CALCIUM_CARBONATE  # scripted group (container) (typed FeaturePython)
  Dunit = g/cm3
  Dvalue = 2.8
  Group = -> [Ca_element005,C_element022,O_element021]
  conduct = 2
  density = 1
  expand = 3
  formula = G4_CALCIUM_CARBONATE
  name = G4_CALCIUM_CARBONATE
  specific = 4
FEATURE [App::DocumentObjectGroupPython] Ca_element006  label="Ca_element : 002"  # scripted group (container) (typed FeaturePython)
  n = 1
  ref = Ca_element
FEATURE [App::DocumentObjectGroupPython] F_element005  label="F_element : 003"  # scripted group (container) (typed FeaturePython)
  n = 2
  ref = F_element
FEATURE [App::DocumentObjectGroupPython] G4_CALCIUM_FLUORIDE  # scripted group (container) (typed FeaturePython)
  Dunit = g/cm3
  Dvalue = 3.18
  Group = -> [Ca_element006,F_element005]
  conduct = 2
  density = 1
  expand = 3
  formula = G4_CALCIUM_FLUORIDE
  name = G4_CALCIUM_FLUORIDE
  specific = 4
FEATURE [App::DocumentObjectGroupPython] Ca_element007  label="Ca_element : 003"  # scripted group (container) (typed FeaturePython)
  n = 1
  ref = Ca_element
FEATURE [App::DocumentObjectGroupPython] O_element022  label="O_element : 010"  # scripted group (container) (typed FeaturePython)
  n = 1
  ref = O_element
FEATURE [App::DocumentObjectGroupPython] G4_CALCIUM_OXIDE  # scripted group (container) (typed FeaturePython)
  Dunit = g/cm3
  Dvalue = 3.3
  Group = -> [Ca_element007,O_element022]
  conduct = 2
  density = 1
  expand = 3
  formula = G4_CALCIUM_OXIDE
  name = G4_CALCIUM_OXIDE
  specific = 4
FEATURE [App::DocumentObjectGroupPython] Ca_element008  label="Ca_element : 004"  # scripted group (container) (typed FeaturePython)
  n = 1
  ref = Ca_element
FEATURE [App::DocumentObjectGroupPython] S_element007  label="S_element : 002"  # scripted group (container) (typed FeaturePython)
  n = 1
  ref = S_element
FEATURE [App::DocumentObjectGroupPython] O_element023  label="O_element : 011"  # scripted group (container) (typed FeaturePython)
  n = 4
  ref = O_element
FEATURE [App::DocumentObjectGroupPython] G4_CALCIUM_SULFATE  # scripted group (container) (typed FeaturePython)
  Dunit = g/cm3
  Dvalue = 2.96
  Group = -> [Ca_element008,S_element007,O_element023]
  conduct = 2
  density = 1
  expand = 3
  formula = G4_CALCIUM_SULFATE
  name = G4_CALCIUM_SULFATE
  specific = 4
FEATURE [App::DocumentObjectGroupPython] Ca_element009  label="Ca_element : 005"  # scripted group (container) (typed FeaturePython)
  n = 1
  ref = Ca_element
FEATURE [App::DocumentObjectGroupPython] W_element002  label="W_element : 002"  # scripted group (container) (typed FeaturePython)
  n = 1
  ref = W_element
FEATURE [App::DocumentObjectGroupPython] O_element024  label="O_element : 012"  # scripted group (container) (typed FeaturePython)
  n = 4
  ref = O_element
FEATURE [App::DocumentObjectGroupPython] G4_CALCIUM_TUNGSTATE  # scripted group (container) (typed FeaturePython)
  Dunit = g/cm3
  Dvalue = 6.062
  Group = -> [Ca_element009,W_element002,O_element024]
  conduct = 2
  density = 1
  expand = 3
  formula = G4_CALCIUM_TUNGSTATE
  name = G4_CALCIUM_TUNGSTATE
  specific = 4
FEATURE [App::DocumentObjectGroupPython] C_element023  label="C_element : 010"  # scripted group (container) (typed FeaturePython)
  n = 1
  ref = C_element
FEATURE [App::DocumentObjectGroupPython] O_element025  label="O_element : 013"  # scripted group (container) (typed FeaturePython)
  n = 2
  ref = O_element
FEATURE [App::DocumentObjectGroupPython] G4_CARBON_DIOXIDE  # scripted group (container) (typed FeaturePython)
  Dunit = g/cm3
  Dvalue = 0.00184212
  Group = -> [C_element023,O_element025]
  conduct = 2
  density = 1
  expand = 3
  formula = G4_CARBON_DIOXIDE
  name = G4_CARBON_DIOXIDE
  specific = 4
FEATURE [App::DocumentObjectGroupPython] C_element024  label="C_element : 011"  # scripted group (container) (typed FeaturePython)
  n = 1
  ref = C_element
FEATURE [App::DocumentObjectGroupPython] Cl_element004  label="Cl_element : 4"  # scripted group (container) (typed FeaturePython)
  n = 4
  ref = Cl_element
FEATURE [App::DocumentObjectGroupPython] G4_CARBON_TETRACHLORIDE  # scripted group (container) (typed FeaturePython)
  Dunit = g/cm3
  Dvalue = 1.594
  Group = -> [C_element024,Cl_element004]
  conduct = 2
  density = 1
  expand = 3
  formula = G4_CARBON_TETRACHLORIDE
  name = G4_CARBON_TETRACHLORIDE
  specific = 4
FEATURE [App::DocumentObjectGroupPython] C_element025  label="C_element : 012"  # scripted group (container) (typed FeaturePython)
  n = 6
  ref = C_element
FEATURE [App::DocumentObjectGroupPython] H_element021  label="H_element : 012"  # scripted group (container) (typed FeaturePython)
  n = 10
  ref = H_element
FEATURE [App::DocumentObjectGroupPython] O_element026  label="O_element : 5"  # scripted group (container) (typed FeaturePython)
  n = 5
  ref = O_element
FEATURE [App::DocumentObjectGroupPython] G4_CELLULOSE_CELLOPHANE  # scripted group (container) (typed FeaturePython)
  Dunit = g/cm3
  Dvalue = 1.42
  Group = -> [C_element025,H_element021,O_element026]
  conduct = 2
  density = 1
  expand = 3
  formula = G4_CELLULOSE_CELLOPHANE
  name = G4_CELLULOSE_CELLOPHANE
  specific = 4
FEATURE [App::DocumentObjectGroupPython] H_element022  label="H_element : 0.067"  # scripted group (container) (typed FeaturePython)
  n = 0.067125
FEATURE [App::DocumentObjectGroupPython] C_element026  label="C_element : 0.545"  # scripted group (container) (typed FeaturePython)
  n = 0.545403
FEATURE [App::DocumentObjectGroupPython] O_element027  label="O_element : 0.387"  # scripted group (container) (typed FeaturePython)
  n = 0.387472
FEATURE [App::DocumentObjectGroupPython] G4_CELLULOSE_BUTYRATE  # scripted group (container) (typed FeaturePython)
  Dunit = g/cm3
  Dvalue = 1.2
  Group = -> [H_element022,C_element026,O_element027]
  conduct = 2
  density = 1
  expand = 3
  formula = G4_CELLULOSE_BUTYRATE
  name = G4_CELLULOSE_BUTYRATE
  specific = 4
FEATURE [App::DocumentObjectGroupPython] H_element023  label="H_element : 0.029"  # scripted group (container) (typed FeaturePython)
  n = 0.029216
FEATURE [App::DocumentObjectGroupPython] C_element027  label="C_element : 0.271"  # scripted group (container) (typed FeaturePython)
  n = 0.271296
FEATURE [App::DocumentObjectGroupPython] N_element013  label="N_element : 0.121"  # scripted group (container) (typed FeaturePython)
  n = 0.121276
FEATURE [App::DocumentObjectGroupPython] O_element028  label="O_element : 0.578"  # scripted group (container) (typed FeaturePython)
  n = 0.578212
FEATURE [App::DocumentObjectGroupPython] G4_CELLULOSE_NITRATE  # scripted group (container) (typed FeaturePython)
  Dunit = g/cm3
  Dvalue = 1.49
  Group = -> [H_element023,C_element027,N_element013,O_element028]
  conduct = 2
  density = 1
  expand = 3
  formula = G4_CELLULOSE_NITRATE
  name = G4_CELLULOSE_NITRATE
  specific = 4
FEATURE [App::DocumentObjectGroupPython] H_element024  label="H_element : 0.108"  # scripted group (container) (typed FeaturePython)
  n = 0.107596
FEATURE [App::DocumentObjectGroupPython] N_element014  label="N_element : 0.001"  # scripted group (container) (typed FeaturePython)
  n = 0.0008
FEATURE [App::DocumentObjectGroupPython] O_element029  label="O_element : 0.875"  # scripted group (container) (typed FeaturePython)
  n = 0.874976
FEATURE [App::DocumentObjectGroupPython] S_element008  label="S_element : 0.015"  # scripted group (container) (typed FeaturePython)
  n = 0.014627
FEATURE [App::DocumentObjectGroupPython] Ce_element001  label="Ce_element : 0.002"  # scripted group (container) (typed FeaturePython)
  n = 0.002001
FEATURE [App::DocumentObjectGroupPython] G4_CERIC_SULFATE  # scripted group (container) (typed FeaturePython)
  Dunit = g/cm3
  Dvalue = 1.03
  Group = -> [H_element024,N_element014,O_element029,S_element008,Ce_element001]
  conduct = 2
  density = 1
  expand = 3
  formula = G4_CERIC_SULFATE
  name = G4_CERIC_SULFATE
  specific = 4
FEATURE [App::DocumentObjectGroupPython] Cs_element001  label="Cs_element : 1"  # scripted group (container) (typed FeaturePython)
  n = 1
  ref = Cs_element
FEATURE [App::DocumentObjectGroupPython] F_element006  label="F_element : 1"  # scripted group (container) (typed FeaturePython)
  n = 1
  ref = F_element
FEATURE [App::DocumentObjectGroupPython] G4_CESIUM_FLUORIDE  # scripted group (container) (typed FeaturePython)
  Dunit = g/cm3
  Dvalue = 4.115
  Group = -> [Cs_element001,F_element006]
  conduct = 2
  density = 1
  expand = 3
  formula = G4_CESIUM_FLUORIDE
  name = G4_CESIUM_FLUORIDE
  specific = 4
FEATURE [App::DocumentObjectGroupPython] Cs_element002  label="Cs_element : 002"  # scripted group (container) (typed FeaturePython)
  n = 1
  ref = Cs_element
FEATURE [App::DocumentObjectGroupPython] I_element001  label="I_element : 1"  # scripted group (container) (typed FeaturePython)
  n = 1
  ref = I_element
FEATURE [App::DocumentObjectGroupPython] G4_CESIUM_IODIDE  # scripted group (container) (typed FeaturePython)
  Dunit = g/cm3
  Dvalue = 4.51
  Group = -> [Cs_element002,I_element001]
  conduct = 2
  density = 1
  expand = 3
  formula = G4_CESIUM_IODIDE
  name = G4_CESIUM_IODIDE
  specific = 4
FEATURE [App::DocumentObjectGroupPython] C_element028  label="C_element : 013"  # scripted group (container) (typed FeaturePython)
  n = 6
  ref = C_element
FEATURE [App::DocumentObjectGroupPython] H_element025  label="H_element : 013"  # scripted group (container) (typed FeaturePython)
  n = 5
  ref = H_element
FEATURE [App::DocumentObjectGroupPython] Cl_element005  label="Cl_element : 1"  # scripted group (container) (typed FeaturePython)
  n = 1
  ref = Cl_element
FEATURE [App::DocumentObjectGroupPython] G4_CHLOROBENZENE  # scripted group (container) (typed FeaturePython)
  Dunit = g/cm3
  Dvalue = 1.1058
  Group = -> [C_element028,H_element025,Cl_element005]
  conduct = 2
  density = 1
  expand = 3
  formula = G4_CHLOROBENZENE
  name = G4_CHLOROBENZENE
  specific = 4
FEATURE [App::DocumentObjectGroupPython] C_element029  label="C_element : 014"  # scripted group (container) (typed FeaturePython)
  n = 1
  ref = C_element
FEATURE [App::DocumentObjectGroupPython] H_element026  label="H_element : 1"  # scripted group (container) (typed FeaturePython)
  n = 1
  ref = H_element
FEATURE [App::DocumentObjectGroupPython] Cl_element006  label="Cl_element : 3"  # scripted group (container) (typed FeaturePython)
  n = 3
  ref = Cl_element
FEATURE [App::DocumentObjectGroupPython] G4_CHLOROFORM  # scripted group (container) (typed FeaturePython)
  Dunit = g/cm3
  Dvalue = 1.4832
  Group = -> [C_element029,H_element026,Cl_element006]
  conduct = 2
  density = 1
  expand = 3
  formula = G4_CHLOROFORM
  name = G4_CHLOROFORM
  specific = 4
FEATURE [App::DocumentObjectGroupPython] H_element027  label="H_element : 0.010"  # scripted group (container) (typed FeaturePython)
  n = 0.01
FEATURE [App::DocumentObjectGroupPython] C_element030  label="C_element : 0.001"  # scripted group (container) (typed FeaturePython)
  n = 0.001
FEATURE [App::DocumentObjectGroupPython] O_element030  label="O_element : 0.529"  # scripted group (container) (typed FeaturePython)
  n = 0.529107
FEATURE [App::DocumentObjectGroupPython] Na_element005  label="Na_element : 0.016"  # scripted group (container) (typed FeaturePython)
  n = 0.016
FEATURE [App::DocumentObjectGroupPython] Mg_element003  label="Mg_element : 0.004"  # scripted group (container) (typed FeaturePython)
  n = 0.002
FEATURE [App::DocumentObjectGroupPython] Al_element002  label="Al_element : 0.034"  # scripted group (container) (typed FeaturePython)
  n = 0.033872
FEATURE [App::DocumentObjectGroupPython] Si_element002  label="Si_element : 0.337"  # scripted group (container) (typed FeaturePython)
  n = 0.337021
FEATURE [App::DocumentObjectGroupPython] K_element003  label="K_element : 0.013"  # scripted group (container) (typed FeaturePython)
  n = 0.013
FEATURE [App::DocumentObjectGroupPython] Ca_element010  label="Ca_element : 0.044"  # scripted group (container) (typed FeaturePython)
  n = 0.044
FEATURE [App::DocumentObjectGroupPython] Fe_element002  label="Fe_element : 0.014"  # scripted group (container) (typed FeaturePython)
  n = 0.014
FEATURE [App::DocumentObjectGroupPython] G4_CONCRETE  # scripted group (container) (typed FeaturePython)
  Dunit = g/cm3
  Dvalue = 2.3
  Group = -> [H_element027,C_element030,O_element030,Na_element005,Mg_element003,Al_element002,Si_element002,K_element003,Ca_element010,Fe_element002]
  conduct = 2
  density = 1
  expand = 3
  formula = G4_CONCRETE
  name = G4_CONCRETE
  specific = 4
FEATURE [App::DocumentObjectGroupPython] C_element031  label="C_element : 015"  # scripted group (container) (typed FeaturePython)
  n = 6
  ref = C_element
FEATURE [App::DocumentObjectGroupPython] H_element028  label="H_element : 12"  # scripted group (container) (typed FeaturePython)
  n = 12
  ref = H_element
FEATURE [App::DocumentObjectGroupPython] G4_CYCLOHEXANE  # scripted group (container) (typed FeaturePython)
  Dunit = g/cm3
  Dvalue = 0.779
  Group = -> [C_element031,H_element028]
  conduct = 2
  density = 1
  expand = 3
  formula = G4_CYCLOHEXANE
  name = G4_CYCLOHEXANE
  specific = 4
FEATURE [App::DocumentObjectGroupPython] C_element032  label="C_element : 016"  # scripted group (container) (typed FeaturePython)
  n = 6
  ref = C_element
FEATURE [App::DocumentObjectGroupPython] H_element029  label="H_element : 4"  # scripted group (container) (typed FeaturePython)
  n = 4
  ref = H_element
FEATURE [App::DocumentObjectGroupPython] Cl_element007  label="Cl_element : 2"  # scripted group (container) (typed FeaturePython)
  n = 2
  ref = Cl_element
FEATURE [App::DocumentObjectGroupPython] G4_1_2_DICHLOROBENZENE  label="G4_1.2-DICHLOROBENZENE"  # scripted group (container) (typed FeaturePython)
  Dunit = g/cm3
  Dvalue = 1.3048
  Group = -> [C_element032,H_element029,Cl_element007]
  conduct = 2
  density = 1
  expand = 3
  formula = G4_1.2-DICHLOROBENZENE
  name = G4_1.2-DICHLOROBENZENE
  specific = 4
FEATURE [App::DocumentObjectGroupPython] C_element033  label="C_element : 017"  # scripted group (container) (typed FeaturePython)
  n = 4
  ref = C_element
FEATURE [App::DocumentObjectGroupPython] H_element030  label="H_element : 8"  # scripted group (container) (typed FeaturePython)
  n = 8
  ref = H_element
FEATURE [App::DocumentObjectGroupPython] O_element031  label="O_element : 014"  # scripted group (container) (typed FeaturePython)
  n = 1
  ref = O_element
FEATURE [App::DocumentObjectGroupPython] Cl_element008  label="Cl_element : 005"  # scripted group (container) (typed FeaturePython)
  n = 2
  ref = Cl_element
FEATURE [App::DocumentObjectGroupPython] G4_DICHLORODIETHYL_ETHER  # scripted group (container) (typed FeaturePython)
  Dunit = g/cm3
  Dvalue = 1.2199
  Group = -> [C_element033,H_element030,O_element031,Cl_element008]
  conduct = 2
  density = 1
  expand = 3
  formula = G4_DICHLORODIETHYL_ETHER
  name = G4_DICHLORODIETHYL_ETHER
  specific = 4
FEATURE [App::DocumentObjectGroupPython] C_element034  label="C_element : 018"  # scripted group (container) (typed FeaturePython)
  n = 2
  ref = C_element
FEATURE [App::DocumentObjectGroupPython] H_element031  label="H_element : 014"  # scripted group (container) (typed FeaturePython)
  n = 4
  ref = H_element
FEATURE [App::DocumentObjectGroupPython] Cl_element009  label="Cl_element : 006"  # scripted group (container) (typed FeaturePython)
  n = 2
  ref = Cl_element
FEATURE [App::DocumentObjectGroupPython] G4_1_2_DICHLOROETHANE  label="G4_1.2-DICHLOROETHANE"  # scripted group (container) (typed FeaturePython)
  Dunit = g/cm3
  Dvalue = 1.2351
  Group = -> [C_element034,H_element031,Cl_element009]
  conduct = 2
  density = 1
  expand = 3
  formula = G4_1.2-DICHLOROETHANE
  name = G4_1.2-DICHLOROETHANE
  specific = 4
FEATURE [App::DocumentObjectGroupPython] C_element035  label="C_element : 019"  # scripted group (container) (typed FeaturePython)
  n = 4
  ref = C_element
FEATURE [App::DocumentObjectGroupPython] H_element032  label="H_element : 015"  # scripted group (container) (typed FeaturePython)
  n = 10
  ref = H_element
FEATURE [App::DocumentObjectGroupPython] O_element032  label="O_element : 015"  # scripted group (container) (typed FeaturePython)
  n = 1
  ref = O_element
FEATURE [App::DocumentObjectGroupPython] G4_DIETHYL_ETHER  # scripted group (container) (typed FeaturePython)
  Dunit = g/cm3
  Dvalue = 0.71378
  Group = -> [C_element035,H_element032,O_element032]
  conduct = 2
  density = 1
  expand = 3
  formula = G4_DIETHYL_ETHER
  name = G4_DIETHYL_ETHER
  specific = 4
FEATURE [App::DocumentObjectGroupPython] C_element036  label="C_element : 020"  # scripted group (container) (typed FeaturePython)
  n = 3
  ref = C_element
FEATURE [App::DocumentObjectGroupPython] H_element033  label="H_element : 016"  # scripted group (container) (typed FeaturePython)
  n = 7
  ref = H_element
FEATURE [App::DocumentObjectGroupPython] N_element015  label="N_element : 008"  # scripted group (container) (typed FeaturePython)
  n = 1
  ref = N_element
FEATURE [App::DocumentObjectGroupPython] O_element033  label="O_element : 016"  # scripted group (container) (typed FeaturePython)
  n = 1
  ref = O_element
FEATURE [App::DocumentObjectGroupPython] G4_N_N_DIMETHYL_FORMAMIDE  label="G4_N.N-DIMETHYL_FORMAMIDE"  # scripted group (container) (typed FeaturePython)
  Dunit = g/cm3
  Dvalue = 0.9487
  Group = -> [C_element036,H_element033,N_element015,O_element033]
  conduct = 2
  density = 1
  expand = 3
  formula = G4_N.N-DIMETHYL_FORMAMIDE
  name = G4_N.N-DIMETHYL_FORMAMIDE
  specific = 4
FEATURE [App::DocumentObjectGroupPython] C_element037  label="C_element : 021"  # scripted group (container) (typed FeaturePython)
  n = 2
  ref = C_element
FEATURE [App::DocumentObjectGroupPython] H_element034  label="H_element : 017"  # scripted group (container) (typed FeaturePython)
  n = 6
  ref = H_element
FEATURE [App::DocumentObjectGroupPython] O_element034  label="O_element : 017"  # scripted group (container) (typed FeaturePython)
  n = 1
  ref = O_element
FEATURE [App::DocumentObjectGroupPython] S_element009  label="S_element : 003"  # scripted group (container) (typed FeaturePython)
  n = 1
  ref = S_element
FEATURE [App::DocumentObjectGroupPython] G4_DIMETHYL_SULFOXIDE  # scripted group (container) (typed FeaturePython)
  Dunit = g/cm3
  Dvalue = 1.1014
  Group = -> [C_element037,H_element034,O_element034,S_element009]
  conduct = 2
  density = 1
  expand = 3
  formula = G4_DIMETHYL_SULFOXIDE
  name = G4_DIMETHYL_SULFOXIDE
  specific = 4
FEATURE [App::DocumentObjectGroupPython] C_element038  label="C_element : 022"  # scripted group (container) (typed FeaturePython)
  n = 2
  ref = C_element
FEATURE [App::DocumentObjectGroupPython] H_element035  label="H_element : 018"  # scripted group (container) (typed FeaturePython)
  n = 6
  ref = H_element
FEATURE [App::DocumentObjectGroupPython] G4_ETHANE  # scripted group (container) (typed FeaturePython)
  Dunit = g/cm3
  Dvalue = 0.00125324
  Group = -> [C_element038,H_element035]
  conduct = 2
  density = 1
  expand = 3
  formula = G4_ETHANE
  name = G4_ETHANE
  specific = 4
FEATURE [App::DocumentObjectGroupPython] C_element039  label="C_element : 023"  # scripted group (container) (typed FeaturePython)
  n = 2
  ref = C_element
FEATURE [App::DocumentObjectGroupPython] H_element036  label="H_element : 019"  # scripted group (container) (typed FeaturePython)
  n = 6
  ref = H_element
FEATURE [App::DocumentObjectGroupPython] O_element035  label="O_element : 018"  # scripted group (container) (typed FeaturePython)
  n = 1
  ref = O_element
FEATURE [App::DocumentObjectGroupPython] G4_ETHYL_ALCOHOL  # scripted group (container) (typed FeaturePython)
  Dunit = g/cm3
  Dvalue = 0.7893
  Group = -> [C_element039,H_element036,O_element035]
  conduct = 2
  density = 1
  expand = 3
  formula = G4_ETHYL_ALCOHOL
  name = G4_ETHYL_ALCOHOL
  specific = 4
FEATURE [App::DocumentObjectGroupPython] H_element037  label="H_element : 0.090"  # scripted group (container) (typed FeaturePython)
  n = 0.090027
FEATURE [App::DocumentObjectGroupPython] C_element040  label="C_element : 0.585"  # scripted group (container) (typed FeaturePython)
  n = 0.585182
FEATURE [App::DocumentObjectGroupPython] O_element036  label="O_element : 0.325"  # scripted group (container) (typed FeaturePython)
  n = 0.324791
FEATURE [App::DocumentObjectGroupPython] G4_ETHYL_CELLULOSE  # scripted group (container) (typed FeaturePython)
  Dunit = g/cm3
  Dvalue = 1.13
  Group = -> [H_element037,C_element040,O_element036]
  conduct = 2
  density = 1
  expand = 3
  formula = G4_ETHYL_CELLULOSE
  name = G4_ETHYL_CELLULOSE
  specific = 4
FEATURE [App::DocumentObjectGroupPython] C_element041  label="C_element : 024"  # scripted group (container) (typed FeaturePython)
  n = 2
  ref = C_element
FEATURE [App::DocumentObjectGroupPython] H_element038  label="H_element : 020"  # scripted group (container) (typed FeaturePython)
  n = 4
  ref = H_element
FEATURE [App::DocumentObjectGroupPython] G4_ETHYLENE  # scripted group (container) (typed FeaturePython)
  Dunit = g/cm3
  Dvalue = 0.00117497
  Group = -> [C_element041,H_element038]
  conduct = 2
  density = 1
  expand = 3
  formula = G4_ETHYLENE
  name = G4_ETHYLENE
  specific = 4
FEATURE [App::DocumentObjectGroupPython] H_element039  label="H_element : 0.096"  # scripted group (container) (typed FeaturePython)
  n = 0.096
FEATURE [App::DocumentObjectGroupPython] C_element042  label="C_element : 0.195"  # scripted group (container) (typed FeaturePython)
  n = 0.195
FEATURE [App::DocumentObjectGroupPython] N_element016  label="N_element : 0.057"  # scripted group (container) (typed FeaturePython)
  n = 0.057
FEATURE [App::DocumentObjectGroupPython] O_element037  label="O_element : 0.646"  # scripted group (container) (typed FeaturePython)
  n = 0.646
FEATURE [App::DocumentObjectGroupPython] Na_element006  label="Na_element : 0.017"  # scripted group (container) (typed FeaturePython)
  n = 0.001
FEATURE [App::DocumentObjectGroupPython] P_element005  label="P_element : 0.104"  # scripted group (container) (typed FeaturePython)
  n = 0.001
FEATURE [App::DocumentObjectGroupPython] S_element010  label="S_element : 0.016"  # scripted group (container) (typed FeaturePython)
  n = 0.003
FEATURE [App::DocumentObjectGroupPython] Cl_element010  label="Cl_element : 0.005"  # scripted group (container) (typed FeaturePython)
  n = 0.001
FEATURE [App::DocumentObjectGroupPython] G4_EYE_LENS_ICRP  # scripted group (container) (typed FeaturePython)
  Dunit = g/cm3
  Dvalue = 1.07
  Group = -> [H_element039,C_element042,N_element016,O_element037,Na_element006,P_element005,S_element010,Cl_element010]
  conduct = 2
  density = 1
  expand = 3
  formula = G4_EYE_LENS_ICRP
  name = G4_EYE_LENS_ICRP
  specific = 4
FEATURE [App::DocumentObjectGroupPython] Fe_element003  label="Fe_element : 2"  # scripted group (container) (typed FeaturePython)
  n = 2
  ref = Fe_element
FEATURE [App::DocumentObjectGroupPython] O_element038  label="O_element : 019"  # scripted group (container) (typed FeaturePython)
  n = 3
  ref = O_element
FEATURE [App::DocumentObjectGroupPython] G4_FERRIC_OXIDE  # scripted group (container) (typed FeaturePython)
  Dunit = g/cm3
  Dvalue = 5.2
  Group = -> [Fe_element003,O_element038]
  conduct = 2
  density = 1
  expand = 3
  formula = G4_FERRIC_OXIDE
  name = G4_FERRIC_OXIDE
  specific = 4
FEATURE [App::DocumentObjectGroupPython] Fe_element004  label="Fe_element : 1"  # scripted group (container) (typed FeaturePython)
  n = 1
  ref = Fe_element
FEATURE [App::DocumentObjectGroupPython] B_element003  label="B_element : 1"  # scripted group (container) (typed FeaturePython)
  n = 1
  ref = B_element
FEATURE [App::DocumentObjectGroupPython] G4_FERROBORIDE  # scripted group (container) (typed FeaturePython)
  Dunit = g/cm3
  Dvalue = 7.15
  Group = -> [Fe_element004,B_element003]
  conduct = 2
  density = 1
  expand = 3
  formula = G4_FERROBORIDE
  name = G4_FERROBORIDE
  specific = 4
FEATURE [App::DocumentObjectGroupPython] Fe_element005  label="Fe_element : 003"  # scripted group (container) (typed FeaturePython)
  n = 1
  ref = Fe_element
FEATURE [App::DocumentObjectGroupPython] O_element039  label="O_element : 020"  # scripted group (container) (typed FeaturePython)
  n = 1
  ref = O_element
FEATURE [App::DocumentObjectGroupPython] G4_FERROUS_OXIDE  # scripted group (container) (typed FeaturePython)
  Dunit = g/cm3
  Dvalue = 5.7
  Group = -> [Fe_element005,O_element039]
  conduct = 2
  density = 1
  expand = 3
  formula = G4_FERROUS_OXIDE
  name = G4_FERROUS_OXIDE
  specific = 4
FEATURE [App::DocumentObjectGroupPython] H_element040  label="H_element : 0.115"  # scripted group (container) (typed FeaturePython)
  n = 0.108259
FEATURE [App::DocumentObjectGroupPython] N_element017  label="N_element : 0.000"  # scripted group (container) (typed FeaturePython)
  n = 2.7e-05
FEATURE [App::DocumentObjectGroupPython] O_element040  label="O_element : 0.879"  # scripted group (container) (typed FeaturePython)
  n = 0.878636
FEATURE [App::DocumentObjectGroupPython] Na_element007  label="Na_element : 0.000"  # scripted group (container) (typed FeaturePython)
  n = 2.2e-05
FEATURE [App::DocumentObjectGroupPython] S_element011  label="S_element : 0.013"  # scripted group (container) (typed FeaturePython)
  n = 0.012968
FEATURE [App::DocumentObjectGroupPython] Cl_element011  label="Cl_element : 0.000"  # scripted group (container) (typed FeaturePython)
  n = 3.4e-05
FEATURE [App::DocumentObjectGroupPython] Fe_element006  label="Fe_element : 0.000"  # scripted group (container) (typed FeaturePython)
  n = 5.4e-05
FEATURE [App::DocumentObjectGroupPython] G4_FERROUS_SULFATE  # scripted group (container) (typed FeaturePython)
  Dunit = g/cm3
  Dvalue = 1.024
  Group = -> [H_element040,N_element017,O_element040,Na_element007,S_element011,Cl_element011,Fe_element006]
  conduct = 2
  density = 1
  expand = 3
  formula = G4_FERROUS_SULFATE
  name = G4_FERROUS_SULFATE
  specific = 4
FEATURE [App::DocumentObjectGroupPython] C_element043  label="C_element : 0.099"  # scripted group (container) (typed FeaturePython)
  n = 0.099335
FEATURE [App::DocumentObjectGroupPython] F_element007  label="F_element : 0.314"  # scripted group (container) (typed FeaturePython)
  n = 0.314247
FEATURE [App::DocumentObjectGroupPython] Cl_element012  label="Cl_element : 0.586"  # scripted group (container) (typed FeaturePython)
  n = 0.586418
FEATURE [App::DocumentObjectGroupPython] G4_FREON_12  label="G4_FREON-12"  # scripted group (container) (typed FeaturePython)
  Dunit = g/cm3
  Dvalue = 1.12
  Group = -> [C_element043,F_element007,Cl_element012]
  conduct = 2
  density = 1
  expand = 3
  formula = G4_FREON-12
  name = G4_FREON-12
  specific = 4
FEATURE [App::DocumentObjectGroupPython] C_element044  label="C_element : 0.057"  # scripted group (container) (typed FeaturePython)
  n = 0.057245
FEATURE [App::DocumentObjectGroupPython] F_element008  label="F_element : 0.181"  # scripted group (container) (typed FeaturePython)
  n = 0.181096
FEATURE [App::DocumentObjectGroupPython] Br_element001  label="Br_element : 0.762"  # scripted group (container) (typed FeaturePython)
  n = 0.761659
FEATURE [App::DocumentObjectGroupPython] G4_FREON_12B2  label="G4_FREON-12B2"  # scripted group (container) (typed FeaturePython)
  Dunit = g/cm3
  Dvalue = 1.8
  Group = -> [C_element044,F_element008,Br_element001]
  conduct = 2
  density = 1
  expand = 3
  formula = G4_FREON-12B2
  name = G4_FREON-12B2
  specific = 4
FEATURE [App::DocumentObjectGroupPython] C_element045  label="C_element : 0.115"  # scripted group (container) (typed FeaturePython)
  n = 0.114983
FEATURE [App::DocumentObjectGroupPython] F_element009  label="F_element : 0.546"  # scripted group (container) (typed FeaturePython)
  n = 0.545621
FEATURE [App::DocumentObjectGroupPython] Cl_element013  label="Cl_element : 0.339"  # scripted group (container) (typed FeaturePython)
  n = 0.339396
FEATURE [App::DocumentObjectGroupPython] G4_FREON_13  label="G4_FREON-13"  # scripted group (container) (typed FeaturePython)
  Dunit = g/cm3
  Dvalue = 0.95
  Group = -> [C_element045,F_element009,Cl_element013]
  conduct = 2
  density = 1
  expand = 3
  formula = G4_FREON-13
  name = G4_FREON-13
  specific = 4
FEATURE [App::DocumentObjectGroupPython] C_element046  label="C_element : 025"  # scripted group (container) (typed FeaturePython)
  n = 1
  ref = C_element
FEATURE [App::DocumentObjectGroupPython] F_element010  label="F_element : 3"  # scripted group (container) (typed FeaturePython)
  n = 3
  ref = F_element
FEATURE [App::DocumentObjectGroupPython] Br_element002  label="Br_element : 1"  # scripted group (container) (typed FeaturePython)
  n = 1
  ref = Br_element
FEATURE [App::DocumentObjectGroupPython] G4_FREON_13B1  label="G4_FREON-13B1"  # scripted group (container) (typed FeaturePython)
  Dunit = g/cm3
  Dvalue = 1.5
  Group = -> [C_element046,F_element010,Br_element002]
  conduct = 2
  density = 1
  expand = 3
  formula = G4_FREON-13B1
  name = G4_FREON-13B1
  specific = 4
FEATURE [App::DocumentObjectGroupPython] C_element047  label="C_element : 0.061"  # scripted group (container) (typed FeaturePython)
  n = 0.061309
FEATURE [App::DocumentObjectGroupPython] F_element011  label="F_element : 0.291"  # scripted group (container) (typed FeaturePython)
  n = 0.290924
FEATURE [App::DocumentObjectGroupPython] I_element002  label="I_element : 0.648"  # scripted group (container) (typed FeaturePython)
  n = 0.647767
FEATURE [App::DocumentObjectGroupPython] G4_FREON_13I1  label="G4_FREON-13I1"  # scripted group (container) (typed FeaturePython)
  Dunit = g/cm3
  Dvalue = 1.8
  Group = -> [C_element047,F_element011,I_element002]
  conduct = 2
  density = 1
  expand = 3
  formula = G4_FREON-13I1
  name = G4_FREON-13I1
  specific = 4
FEATURE [App::DocumentObjectGroupPython] Gd_element001  label="Gd_element : 2"  # scripted group (container) (typed FeaturePython)
  n = 2
  ref = Gd_element
FEATURE [App::DocumentObjectGroupPython] O_element041  label="O_element : 021"  # scripted group (container) (typed FeaturePython)
  n = 2
  ref = O_element
FEATURE [App::DocumentObjectGroupPython] S_element012  label="S_element : 004"  # scripted group (container) (typed FeaturePython)
  n = 1
  ref = S_element
FEATURE [App::DocumentObjectGroupPython] G4_GADOLINIUM_OXYSULFIDE  # scripted group (container) (typed FeaturePython)
  Dunit = g/cm3
  Dvalue = 7.44
  Group = -> [Gd_element001,O_element041,S_element012]
  conduct = 2
  density = 1
  expand = 3
  formula = G4_GADOLINIUM_OXYSULFIDE
  name = G4_GADOLINIUM_OXYSULFIDE
  specific = 4
FEATURE [App::DocumentObjectGroupPython] Ga_element001  label="Ga_element : 1"  # scripted group (container) (typed FeaturePython)
  n = 1
  ref = Ga_element
FEATURE [App::DocumentObjectGroupPython] As_element001  label="As_element : 1"  # scripted group (container) (typed FeaturePython)
  n = 1
  ref = As_element
FEATURE [App::DocumentObjectGroupPython] G4_GALLIUM_ARSENIDE  # scripted group (container) (typed FeaturePython)
  Dunit = g/cm3
  Dvalue = 5.31
  Group = -> [Ga_element001,As_element001]
  conduct = 2
  density = 1
  expand = 3
  formula = G4_GALLIUM_ARSENIDE
  name = G4_GALLIUM_ARSENIDE
  specific = 4
FEATURE [App::DocumentObjectGroupPython] H_element041  label="H_element : 0.081"  # scripted group (container) (typed FeaturePython)
  n = 0.08118
FEATURE [App::DocumentObjectGroupPython] C_element048  label="C_element : 0.416"  # scripted group (container) (typed FeaturePython)
  n = 0.41606
FEATURE [App::DocumentObjectGroupPython] N_element018  label="N_element : 0.111"  # scripted group (container) (typed FeaturePython)
  n = 0.11124
FEATURE [App::DocumentObjectGroupPython] O_element042  label="O_element : 0.381"  # scripted group (container) (typed FeaturePython)
  n = 0.38064
FEATURE [App::DocumentObjectGroupPython] S_element013  label="S_element : 0.011"  # scripted group (container) (typed FeaturePython)
  n = 0.01088
FEATURE [App::DocumentObjectGroupPython] G4_GEL_PHOTO_EMULSION  # scripted group (container) (typed FeaturePython)
  Dunit = g/cm3
  Dvalue = 1.2914
  Group = -> [H_element041,C_element048,N_element018,O_element042,S_element013]
  conduct = 2
  density = 1
  expand = 3
  formula = G4_GEL_PHOTO_EMULSION
  name = G4_GEL_PHOTO_EMULSION
  specific = 4
FEATURE [App::DocumentObjectGroupPython] B_element004  label="B_element : 0.040"  # scripted group (container) (typed FeaturePython)
  n = 0.0400639
FEATURE [App::DocumentObjectGroupPython] O_element043  label="O_element : 0.540"  # scripted group (container) (typed FeaturePython)
  n = 0.539561
FEATURE [App::DocumentObjectGroupPython] Na_element008  label="Na_element : 0.028"  # scripted group (container) (typed FeaturePython)
  n = 0.0281909
FEATURE [App::DocumentObjectGroupPython] Al_element003  label="Al_element : 0.012"  # scripted group (container) (typed FeaturePython)
  n = 0.011644
FEATURE [App::DocumentObjectGroupPython] Si_element003  label="Si_element : 0.377"  # scripted group (container) (typed FeaturePython)
  n = 0.377219
FEATURE [App::DocumentObjectGroupPython] K_element004  label="K_element : 0.014"  # scripted group (container) (typed FeaturePython)
  n = 0.00332099
FEATURE [App::DocumentObjectGroupPython] G4_Pyrex_Glass  # scripted group (container) (typed FeaturePython)
  Dunit = g/cm3
  Dvalue = 2.23
  Group = -> [B_element004,O_element043,Na_element008,Al_element003,Si_element003,K_element004]
  conduct = 2
  density = 1
  expand = 3
  formula = G4_Pyrex_Glass
  name = G4_Pyrex_Glass
  specific = 4
FEATURE [App::DocumentObjectGroupPython] O_element044  label="O_element : 0.156"  # scripted group (container) (typed FeaturePython)
  n = 0.156453
FEATURE [App::DocumentObjectGroupPython] Si_element004  label="Si_element : 0.081"  # scripted group (container) (typed FeaturePython)
  n = 0.080866
FEATURE [App::DocumentObjectGroupPython] Ti_element001  label="Ti_element : 0.008"  # scripted group (container) (typed FeaturePython)
  n = 0.008092
FEATURE [App::DocumentObjectGroupPython] As_element002  label="As_element : 0.003"  # scripted group (container) (typed FeaturePython)
  n = 0.002651
FEATURE [App::DocumentObjectGroupPython] Pb_element001  label="Pb_element : 0.752"  # scripted group (container) (typed FeaturePython)
  n = 0.751938
FEATURE [App::DocumentObjectGroupPython] G4_GLASS_LEAD  # scripted group (container) (typed FeaturePython)
  Dunit = g/cm3
  Dvalue = 6.22
  Group = -> [O_element044,Si_element004,Ti_element001,As_element002,Pb_element001]
  conduct = 2
  density = 1
  expand = 3
  formula = G4_GLASS_LEAD
  name = G4_GLASS_LEAD
  specific = 4
FEATURE [App::DocumentObjectGroupPython] O_element045  label="O_element : 0.460"  # scripted group (container) (typed FeaturePython)
  n = 0.4598
FEATURE [App::DocumentObjectGroupPython] Na_element009  label="Na_element : 0.096"  # scripted group (container) (typed FeaturePython)
  n = 0.0964411
FEATURE [App::DocumentObjectGroupPython] Si_element005  label="Si_element : 0.378"  # scripted group (container) (typed FeaturePython)
  n = 0.336553
FEATURE [App::DocumentObjectGroupPython] Ca_element011  label="Ca_element : 0.107"  # scripted group (container) (typed FeaturePython)
  n = 0.107205
FEATURE [App::DocumentObjectGroupPython] G4_GLASS_PLATE  # scripted group (container) (typed FeaturePython)
  Dunit = g/cm3
  Dvalue = 2.4
  Group = -> [O_element045,Na_element009,Si_element005,Ca_element011]
  conduct = 2
  density = 1
  expand = 3
  formula = G4_GLASS_PLATE
  name = G4_GLASS_PLATE
  specific = 4
FEATURE [App::DocumentObjectGroupPython] C_element049  label="C_element : 026"  # scripted group (container) (typed FeaturePython)
  n = 5
  ref = C_element
FEATURE [App::DocumentObjectGroupPython] H_element042  label="H_element : 021"  # scripted group (container) (typed FeaturePython)
  n = 10
  ref = H_element
FEATURE [App::DocumentObjectGroupPython] N_element019  label="N_element : 2"  # scripted group (container) (typed FeaturePython)
  n = 2
  ref = N_element
FEATURE [App::DocumentObjectGroupPython] O_element046  label="O_element : 022"  # scripted group (container) (typed FeaturePython)
  n = 3
  ref = O_element
FEATURE [App::DocumentObjectGroupPython] G4_GLUTAMINE  # scripted group (container) (typed FeaturePython)
  Dunit = g/cm3
  Dvalue = 1.46
  Group = -> [C_element049,H_element042,N_element019,O_element046]
  conduct = 2
  density = 1
  expand = 3
  formula = G4_GLUTAMINE
  name = G4_GLUTAMINE
  specific = 4
FEATURE [App::DocumentObjectGroupPython] C_element050  label="C_element : 027"  # scripted group (container) (typed FeaturePython)
  n = 3
  ref = C_element
FEATURE [App::DocumentObjectGroupPython] H_element043  label="H_element : 022"  # scripted group (container) (typed FeaturePython)
  n = 8
  ref = H_element
FEATURE [App::DocumentObjectGroupPython] O_element047  label="O_element : 023"  # scripted group (container) (typed FeaturePython)
  n = 3
  ref = O_element
FEATURE [App::DocumentObjectGroupPython] G4_GLYCEROL  # scripted group (container) (typed FeaturePython)
  Dunit = g/cm3
  Dvalue = 1.2613
  Group = -> [C_element050,H_element043,O_element047]
  conduct = 2
  density = 1
  expand = 3
  formula = G4_GLYCEROL
  name = G4_GLYCEROL
  specific = 4
FEATURE [App::DocumentObjectGroupPython] C_element051  label="C_element : 028"  # scripted group (container) (typed FeaturePython)
  n = 5
  ref = C_element
FEATURE [App::DocumentObjectGroupPython] H_element044  label="H_element : 023"  # scripted group (container) (typed FeaturePython)
  n = 5
  ref = H_element
FEATURE [App::DocumentObjectGroupPython] N_element020  label="N_element : 009"  # scripted group (container) (typed FeaturePython)
  n = 5
  ref = N_element
FEATURE [App::DocumentObjectGroupPython] O_element048  label="O_element : 024"  # scripted group (container) (typed FeaturePython)
  n = 1
  ref = O_element
FEATURE [App::DocumentObjectGroupPython] G4_GUANINE  # scripted group (container) (typed FeaturePython)
  Dunit = g/cm3
  Dvalue = 2.2
  Group = -> [C_element051,H_element044,N_element020,O_element048]
  conduct = 2
  density = 1
  expand = 3
  formula = G4_GUANINE
  name = G4_GUANINE
  specific = 4
FEATURE [App::DocumentObjectGroupPython] Ca_element012  label="Ca_element : 006"  # scripted group (container) (typed FeaturePython)
  n = 1
  ref = Ca_element
FEATURE [App::DocumentObjectGroupPython] S_element014  label="S_element : 005"  # scripted group (container) (typed FeaturePython)
  n = 1
  ref = S_element
FEATURE [App::DocumentObjectGroupPython] O_element049  label="O_element : 6"  # scripted group (container) (typed FeaturePython)
  n = 6
  ref = O_element
FEATURE [App::DocumentObjectGroupPython] H_element045  label="H_element : 024"  # scripted group (container) (typed FeaturePython)
  n = 4
  ref = H_element
FEATURE [App::DocumentObjectGroupPython] G4_GYPSUM  # scripted group (container) (typed FeaturePython)
  Dunit = g/cm3
  Dvalue = 2.32
  Group = -> [Ca_element012,S_element014,O_element049,H_element045]
  conduct = 2
  density = 1
  expand = 3
  formula = G4_GYPSUM
  name = G4_GYPSUM
  specific = 4
FEATURE [App::DocumentObjectGroupPython] C_element052  label="C_element : 7"  # scripted group (container) (typed FeaturePython)
  n = 7
  ref = C_element
FEATURE [App::DocumentObjectGroupPython] H_element046  label="H_element : 16"  # scripted group (container) (typed FeaturePython)
  n = 16
  ref = H_element
FEATURE [App::DocumentObjectGroupPython] G4_N_HEPTANE  label="G4_N-HEPTANE"  # scripted group (container) (typed FeaturePython)
  Dunit = g/cm3
  Dvalue = 0.68376
  Group = -> [C_element052,H_element046]
  conduct = 2
  density = 1
  expand = 3
  formula = G4_N-HEPTANE
  name = G4_N-HEPTANE
  specific = 4
FEATURE [App::DocumentObjectGroupPython] C_element053  label="C_element : 029"  # scripted group (container) (typed FeaturePython)
  n = 6
  ref = C_element
FEATURE [App::DocumentObjectGroupPython] H_element047  label="H_element : 14"  # scripted group (container) (typed FeaturePython)
  n = 14
  ref = H_element
FEATURE [App::DocumentObjectGroupPython] G4_N_HEXANE  label="G4_N-HEXANE"  # scripted group (container) (typed FeaturePython)
  Dunit = g/cm3
  Dvalue = 0.6603
  Group = -> [C_element053,H_element047]
  conduct = 2
  density = 1
  expand = 3
  formula = G4_N-HEXANE
  name = G4_N-HEXANE
  specific = 4
FEATURE [App::DocumentObjectGroupPython] C_element054  label="C_element : 22"  # scripted group (container) (typed FeaturePython)
  n = 22
  ref = C_element
FEATURE [App::DocumentObjectGroupPython] H_element048  label="H_element : 025"  # scripted group (container) (typed FeaturePython)
  n = 10
  ref = H_element
FEATURE [App::DocumentObjectGroupPython] N_element021  label="N_element : 010"  # scripted group (container) (typed FeaturePython)
  n = 2
  ref = N_element
FEATURE [App::DocumentObjectGroupPython] O_element050  label="O_element : 025"  # scripted group (container) (typed FeaturePython)
  n = 5
  ref = O_element
FEATURE [App::DocumentObjectGroupPython] G4_KAPTON  # scripted group (container) (typed FeaturePython)
  Dunit = g/cm3
  Dvalue = 1.42
  Group = -> [C_element054,H_element048,N_element021,O_element050]
  conduct = 2
  density = 1
  expand = 3
  formula = G4_KAPTON
  name = G4_KAPTON
  specific = 4
FEATURE [App::DocumentObjectGroupPython] La_element001  label="La_element : 1"  # scripted group (container) (typed FeaturePython)
  n = 1
  ref = La_element
FEATURE [App::DocumentObjectGroupPython] Br_element003  label="Br_element : 002"  # scripted group (container) (typed FeaturePython)
  n = 1
  ref = Br_element
FEATURE [App::DocumentObjectGroupPython] O_element051  label="O_element : 026"  # scripted group (container) (typed FeaturePython)
  n = 1
  ref = O_element
FEATURE [App::DocumentObjectGroupPython] G4_LANTHANUM_OXYBROMIDE  # scripted group (container) (typed FeaturePython)
  Dunit = g/cm3
  Dvalue = 6.28
  Group = -> [La_element001,Br_element003,O_element051]
  conduct = 2
  density = 1
  expand = 3
  formula = G4_LANTHANUM_OXYBROMIDE
  name = G4_LANTHANUM_OXYBROMIDE
  specific = 4
FEATURE [App::DocumentObjectGroupPython] La_element002  label="La_element : 2"  # scripted group (container) (typed FeaturePython)
  n = 2
  ref = La_element
FEATURE [App::DocumentObjectGroupPython] O_element052  label="O_element : 027"  # scripted group (container) (typed FeaturePython)
  n = 2
  ref = O_element
FEATURE [App::DocumentObjectGroupPython] S_element015  label="S_element : 006"  # scripted group (container) (typed FeaturePython)
  n = 1
  ref = S_element
FEATURE [App::DocumentObjectGroupPython] G4_LANTHANUM_OXYSULFIDE  # scripted group (container) (typed FeaturePython)
  Dunit = g/cm3
  Dvalue = 5.86
  Group = -> [La_element002,O_element052,S_element015]
  conduct = 2
  density = 1
  expand = 3
  formula = G4_LANTHANUM_OXYSULFIDE
  name = G4_LANTHANUM_OXYSULFIDE
  specific = 4
FEATURE [App::DocumentObjectGroupPython] O_element053  label="O_element : 0.072"  # scripted group (container) (typed FeaturePython)
  n = 0.071682
FEATURE [App::DocumentObjectGroupPython] Pb_element002  label="Pb_element : 0.928"  # scripted group (container) (typed FeaturePython)
  n = 0.928318
FEATURE [App::DocumentObjectGroupPython] G4_LEAD_OXIDE  # scripted group (container) (typed FeaturePython)
  Dunit = g/cm3
  Dvalue = 9.53
  Group = -> [O_element053,Pb_element002]
  conduct = 2
  density = 1
  expand = 3
  formula = G4_LEAD_OXIDE
  name = G4_LEAD_OXIDE
  specific = 4
FEATURE [App::DocumentObjectGroupPython] Li_element001  label="Li_element : 1"  # scripted group (container) (typed FeaturePython)
  n = 1
  ref = Li_element
FEATURE [App::DocumentObjectGroupPython] N_element022  label="N_element : 011"  # scripted group (container) (typed FeaturePython)
  n = 1
  ref = N_element
FEATURE [App::DocumentObjectGroupPython] H_element049  label="H_element : 026"  # scripted group (container) (typed FeaturePython)
  n = 2
  ref = H_element
FEATURE [App::DocumentObjectGroupPython] G4_LITHIUM_AMIDE  # scripted group (container) (typed FeaturePython)
  Dunit = g/cm3
  Dvalue = 1.178
  Group = -> [Li_element001,N_element022,H_element049]
  conduct = 2
  density = 1
  expand = 3
  formula = G4_LITHIUM_AMIDE
  name = G4_LITHIUM_AMIDE
  specific = 4
FEATURE [App::DocumentObjectGroupPython] Li_element002  label="Li_element : 2"  # scripted group (container) (typed FeaturePython)
  n = 2
  ref = Li_element
FEATURE [App::DocumentObjectGroupPython] C_element055  label="C_element : 030"  # scripted group (container) (typed FeaturePython)
  n = 1
  ref = C_element
FEATURE [App::DocumentObjectGroupPython] O_element054  label="O_element : 028"  # scripted group (container) (typed FeaturePython)
  n = 3
  ref = O_element
FEATURE [App::DocumentObjectGroupPython] G4_LITHIUM_CARBONATE  # scripted group (container) (typed FeaturePython)
  Dunit = g/cm3
  Dvalue = 2.11
  Group = -> [Li_element002,C_element055,O_element054]
  conduct = 2
  density = 1
  expand = 3
  formula = G4_LITHIUM_CARBONATE
  name = G4_LITHIUM_CARBONATE
  specific = 4
FEATURE [App::DocumentObjectGroupPython] Li_element003  label="Li_element : 003"  # scripted group (container) (typed FeaturePython)
  n = 1
  ref = Li_element
FEATURE [App::DocumentObjectGroupPython] F_element012  label="F_element : 004"  # scripted group (container) (typed FeaturePython)
  n = 1
  ref = F_element
FEATURE [App::DocumentObjectGroupPython] G4_LITHIUM_FLUORIDE  # scripted group (container) (typed FeaturePython)
  Dunit = g/cm3
  Dvalue = 2.635
  Group = -> [Li_element003,F_element012]
  conduct = 2
  density = 1
  expand = 3
  formula = G4_LITHIUM_FLUORIDE
  name = G4_LITHIUM_FLUORIDE
  specific = 4
FEATURE [App::DocumentObjectGroupPython] Li_element004  label="Li_element : 004"  # scripted group (container) (typed FeaturePython)
  n = 1
  ref = Li_element
FEATURE [App::DocumentObjectGroupPython] H_element050  label="H_element : 027"  # scripted group (container) (typed FeaturePython)
  n = 1
  ref = H_element
FEATURE [App::DocumentObjectGroupPython] G4_LITHIUM_HYDRIDE  # scripted group (container) (typed FeaturePython)
  Dunit = g/cm3
  Dvalue = 0.82
  Group = -> [Li_element004,H_element050]
  conduct = 2
  density = 1
  expand = 3
  formula = G4_LITHIUM_HYDRIDE
  name = G4_LITHIUM_HYDRIDE
  specific = 4
FEATURE [App::DocumentObjectGroupPython] Li_element005  label="Li_element : 005"  # scripted group (container) (typed FeaturePython)
  n = 1
  ref = Li_element
FEATURE [App::DocumentObjectGroupPython] I_element003  label="I_element : 002"  # scripted group (container) (typed FeaturePython)
  n = 1
  ref = I_element
FEATURE [App::DocumentObjectGroupPython] G4_LITHIUM_IODIDE  # scripted group (container) (typed FeaturePython)
  Dunit = g/cm3
  Dvalue = 3.494
  Group = -> [Li_element005,I_element003]
  conduct = 2
  density = 1
  expand = 3
  formula = G4_LITHIUM_IODIDE
  name = G4_LITHIUM_IODIDE
  specific = 4
FEATURE [App::DocumentObjectGroupPython] Li_element006  label="Li_element : 006"  # scripted group (container) (typed FeaturePython)
  n = 2
  ref = Li_element
FEATURE [App::DocumentObjectGroupPython] O_element055  label="O_element : 029"  # scripted group (container) (typed FeaturePython)
  n = 1
  ref = O_element
FEATURE [App::DocumentObjectGroupPython] G4_LITHIUM_OXIDE  # scripted group (container) (typed FeaturePython)
  Dunit = g/cm3
  Dvalue = 2.013
  Group = -> [Li_element006,O_element055]
  conduct = 2
  density = 1
  expand = 3
  formula = G4_LITHIUM_OXIDE
  name = G4_LITHIUM_OXIDE
  specific = 4
FEATURE [App::DocumentObjectGroupPython] Li_element007  label="Li_element : 007"  # scripted group (container) (typed FeaturePython)
  n = 2
  ref = Li_element
FEATURE [App::DocumentObjectGroupPython] B_element005  label="B_element : 005"  # scripted group (container) (typed FeaturePython)
  n = 4
  ref = B_element
FEATURE [App::DocumentObjectGroupPython] O_element056  label="O_element : 7"  # scripted group (container) (typed FeaturePython)
  n = 7
  ref = O_element
FEATURE [App::DocumentObjectGroupPython] G4_LITHIUM_TETRABORATE  # scripted group (container) (typed FeaturePython)
  Dunit = g/cm3
  Dvalue = 2.44
  Group = -> [Li_element007,B_element005,O_element056]
  conduct = 2
  density = 1
  expand = 3
  formula = G4_LITHIUM_TETRABORATE
  name = G4_LITHIUM_TETRABORATE
  specific = 4
FEATURE [App::DocumentObjectGroupPython] H_element051  label="H_element : 0.105"  # scripted group (container) (typed FeaturePython)
  n = 0.105
FEATURE [App::DocumentObjectGroupPython] C_element056  label="C_element : 0.083"  # scripted group (container) (typed FeaturePython)
  n = 0.083
FEATURE [App::DocumentObjectGroupPython] N_element023  label="N_element : 0.023"  # scripted group (container) (typed FeaturePython)
  n = 0.023
FEATURE [App::DocumentObjectGroupPython] O_element057  label="O_element : 0.779"  # scripted group (container) (typed FeaturePython)
  n = 0.779
FEATURE [App::DocumentObjectGroupPython] Na_element010  label="Na_element : 0.097"  # scripted group (container) (typed FeaturePython)
  n = 0.002
FEATURE [App::DocumentObjectGroupPython] P_element006  label="P_element : 0.105"  # scripted group (container) (typed FeaturePython)
  n = 0.001
FEATURE [App::DocumentObjectGroupPython] S_element016  label="S_element : 0.017"  # scripted group (container) (typed FeaturePython)
  n = 0.002
FEATURE [App::DocumentObjectGroupPython] Cl_element014  label="Cl_element : 0.587"  # scripted group (container) (typed FeaturePython)
  n = 0.003
FEATURE [App::DocumentObjectGroupPython] K_element005  label="K_element : 0.015"  # scripted group (container) (typed FeaturePython)
  n = 0.002
FEATURE [App::DocumentObjectGroupPython] G4_LUNG_ICRP  # scripted group (container) (typed FeaturePython)
  Dunit = g/cm3
  Dvalue = 1.04
  Group = -> [H_element051,C_element056,N_element023,O_element057,Na_element010,P_element006,S_element016,Cl_element014,K_element005]
  conduct = 2
  density = 1
  expand = 3
  formula = G4_LUNG_ICRP
  name = G4_LUNG_ICRP
  specific = 4
FEATURE [App::DocumentObjectGroupPython] H_element052  label="H_element : 0.116"  # scripted group (container) (typed FeaturePython)
  n = 0.114318
FEATURE [App::DocumentObjectGroupPython] C_element057  label="C_element : 0.656"  # scripted group (container) (typed FeaturePython)
  n = 0.655824
FEATURE [App::DocumentObjectGroupPython] O_element058  label="O_element : 0.092"  # scripted group (container) (typed FeaturePython)
  n = 0.0921831
FEATURE [App::DocumentObjectGroupPython] Mg_element004  label="Mg_element : 0.135"  # scripted group (container) (typed FeaturePython)
  n = 0.134792
FEATURE [App::DocumentObjectGroupPython] Ca_element013  label="Ca_element : 0.003"  # scripted group (container) (typed FeaturePython)
  n = 0.002883
FEATURE [App::DocumentObjectGroupPython] G4_M3_WAX  # scripted group (container) (typed FeaturePython)
  Dunit = g/cm3
  Dvalue = 1.05
  Group = -> [H_element052,C_element057,O_element058,Mg_element004,Ca_element013]
  conduct = 2
  density = 1
  expand = 3
  formula = G4_M3_WAX
  name = G4_M3_WAX
  specific = 4
FEATURE [App::DocumentObjectGroupPython] Mg_element005  label="Mg_element : 1"  # scripted group (container) (typed FeaturePython)
  n = 1
  ref = Mg_element
FEATURE [App::DocumentObjectGroupPython] C_element058  label="C_element : 031"  # scripted group (container) (typed FeaturePython)
  n = 1
  ref = C_element
FEATURE [App::DocumentObjectGroupPython] O_element059  label="O_element : 030"  # scripted group (container) (typed FeaturePython)
  n = 3
  ref = O_element
FEATURE [App::DocumentObjectGroupPython] G4_MAGNESIUM_CARBONATE  # scripted group (container) (typed FeaturePython)
  Dunit = g/cm3
  Dvalue = 2.958
  Group = -> [Mg_element005,C_element058,O_element059]
  conduct = 2
  density = 1
  expand = 3
  formula = G4_MAGNESIUM_CARBONATE
  name = G4_MAGNESIUM_CARBONATE
  specific = 4
FEATURE [App::DocumentObjectGroupPython] Mg_element006  label="Mg_element : 002"  # scripted group (container) (typed FeaturePython)
  n = 1
  ref = Mg_element
FEATURE [App::DocumentObjectGroupPython] F_element013  label="F_element : 005"  # scripted group (container) (typed FeaturePython)
  n = 2
  ref = F_element
FEATURE [App::DocumentObjectGroupPython] G4_MAGNESIUM_FLUORIDE  # scripted group (container) (typed FeaturePython)
  Dunit = g/cm3
  Dvalue = 3
  Group = -> [Mg_element006,F_element013]
  conduct = 2
  density = 1
  expand = 3
  formula = G4_MAGNESIUM_FLUORIDE
  name = G4_MAGNESIUM_FLUORIDE
  specific = 4
FEATURE [App::DocumentObjectGroupPython] Mg_element007  label="Mg_element : 003"  # scripted group (container) (typed FeaturePython)
  n = 1
  ref = Mg_element
FEATURE [App::DocumentObjectGroupPython] O_element060  label="O_element : 031"  # scripted group (container) (typed FeaturePython)
  n = 1
  ref = O_element
FEATURE [App::DocumentObjectGroupPython] G4_MAGNESIUM_OXIDE  # scripted group (container) (typed FeaturePython)
  Dunit = g/cm3
  Dvalue = 3.58
  Group = -> [Mg_element007,O_element060]
  conduct = 2
  density = 1
  expand = 3
  formula = G4_MAGNESIUM_OXIDE
  name = G4_MAGNESIUM_OXIDE
  specific = 4
FEATURE [App::DocumentObjectGroupPython] Mg_element008  label="Mg_element : 004"  # scripted group (container) (typed FeaturePython)
  n = 1
  ref = Mg_element
FEATURE [App::DocumentObjectGroupPython] B_element006  label="B_element : 006"  # scripted group (container) (typed FeaturePython)
  n = 4
  ref = B_element
FEATURE [App::DocumentObjectGroupPython] O_element061  label="O_element : 032"  # scripted group (container) (typed FeaturePython)
  n = 7
  ref = O_element
FEATURE [App::DocumentObjectGroupPython] G4_MAGNESIUM_TETRABORATE  # scripted group (container) (typed FeaturePython)
  Dunit = g/cm3
  Dvalue = 2.53
  Group = -> [Mg_element008,B_element006,O_element061]
  conduct = 2
  density = 1
  expand = 3
  formula = G4_MAGNESIUM_TETRABORATE
  name = G4_MAGNESIUM_TETRABORATE
  specific = 4
FEATURE [App::DocumentObjectGroupPython] Hg_element001  label="Hg_element : 1"  # scripted group (container) (typed FeaturePython)
  n = 1
  ref = Hg_element
FEATURE [App::DocumentObjectGroupPython] I_element004  label="I_element : 2"  # scripted group (container) (typed FeaturePython)
  n = 2
  ref = I_element
FEATURE [App::DocumentObjectGroupPython] G4_MERCURIC_IODIDE  # scripted group (container) (typed FeaturePython)
  Dunit = g/cm3
  Dvalue = 6.36
  Group = -> [Hg_element001,I_element004]
  conduct = 2
  density = 1
  expand = 3
  formula = G4_MERCURIC_IODIDE
  name = G4_MERCURIC_IODIDE
  specific = 4
FEATURE [App::DocumentObjectGroupPython] C_element059  label="C_element : 032"  # scripted group (container) (typed FeaturePython)
  n = 1
  ref = C_element
FEATURE [App::DocumentObjectGroupPython] H_element053  label="H_element : 028"  # scripted group (container) (typed FeaturePython)
  n = 4
  ref = H_element
FEATURE [App::DocumentObjectGroupPython] G4_METHANE  # scripted group (container) (typed FeaturePython)
  Dunit = g/cm3
  Dvalue = 0.000667151
  Group = -> [C_element059,H_element053]
  conduct = 2
  density = 1
  expand = 3
  formula = G4_METHANE
  name = G4_METHANE
  specific = 4
FEATURE [App::DocumentObjectGroupPython] C_element060  label="C_element : 033"  # scripted group (container) (typed FeaturePython)
  n = 1
  ref = C_element
FEATURE [App::DocumentObjectGroupPython] H_element054  label="H_element : 029"  # scripted group (container) (typed FeaturePython)
  n = 4
  ref = H_element
FEATURE [App::DocumentObjectGroupPython] O_element062  label="O_element : 033"  # scripted group (container) (typed FeaturePython)
  n = 1
  ref = O_element
FEATURE [App::DocumentObjectGroupPython] G4_METHANOL  # scripted group (container) (typed FeaturePython)
  Dunit = g/cm3
  Dvalue = 0.7914
  Group = -> [C_element060,H_element054,O_element062]
  conduct = 2
  density = 1
  expand = 3
  formula = G4_METHANOL
  name = G4_METHANOL
  specific = 4
FEATURE [App::DocumentObjectGroupPython] H_element055  label="H_element : 0.134"  # scripted group (container) (typed FeaturePython)
  n = 0.13404
FEATURE [App::DocumentObjectGroupPython] C_element061  label="C_element : 0.778"  # scripted group (container) (typed FeaturePython)
  n = 0.77796
FEATURE [App::DocumentObjectGroupPython] O_element063  label="O_element : 0.035"  # scripted group (container) (typed FeaturePython)
  n = 0.03502
FEATURE [App::DocumentObjectGroupPython] Mg_element009  label="Mg_element : 0.039"  # scripted group (container) (typed FeaturePython)
  n = 0.038594
FEATURE [App::DocumentObjectGroupPython] Ti_element002  label="Ti_element : 0.014"  # scripted group (container) (typed FeaturePython)
  n = 0.014386
FEATURE [App::DocumentObjectGroupPython] G4_MIX_D_WAX  # scripted group (container) (typed FeaturePython)
  Dunit = g/cm3
  Dvalue = 0.99
  Group = -> [H_element055,C_element061,O_element063,Mg_element009,Ti_element002]
  conduct = 2
  density = 1
  expand = 3
  formula = G4_MIX_D_WAX
  name = G4_MIX_D_WAX
  specific = 4
FEATURE [App::DocumentObjectGroupPython] H_element056  label="H_element : 0.135"  # scripted group (container) (typed FeaturePython)
  n = 0.081192
FEATURE [App::DocumentObjectGroupPython] C_element062  label="C_element : 0.583"  # scripted group (container) (typed FeaturePython)
  n = 0.583442
FEATURE [App::DocumentObjectGroupPython] N_element024  label="N_element : 0.018"  # scripted group (container) (typed FeaturePython)
  n = 0.017798
FEATURE [App::DocumentObjectGroupPython] O_element064  label="O_element : 0.186"  # scripted group (container) (typed FeaturePython)
  n = 0.186381
FEATURE [App::DocumentObjectGroupPython] Mg_element010  label="Mg_element : 0.130"  # scripted group (container) (typed FeaturePython)
  n = 0.130287
FEATURE [App::DocumentObjectGroupPython] Cl_element015  label="Cl_element : 0.588"  # scripted group (container) (typed FeaturePython)
  n = 0.0009
FEATURE [App::DocumentObjectGroupPython] G4_MS20_TISSUE  # scripted group (container) (typed FeaturePython)
  Dunit = g/cm3
  Dvalue = 1
  Group = -> [H_element056,C_element062,N_element024,O_element064,Mg_element010,Cl_element015]
  conduct = 2
  density = 1
  expand = 3
  formula = G4_MS20_TISSUE
  name = G4_MS20_TISSUE
  specific = 4
FEATURE [App::DocumentObjectGroupPython] H_element057  label="H_element : 0.136"  # scripted group (container) (typed FeaturePython)
  n = 0.102
FEATURE [App::DocumentObjectGroupPython] C_element063  label="C_element : 0.143"  # scripted group (container) (typed FeaturePython)
  n = 0.143
FEATURE [App::DocumentObjectGroupPython] N_element025  label="N_element : 0.034"  # scripted group (container) (typed FeaturePython)
  n = 0.034
FEATURE [App::DocumentObjectGroupPython] O_element065  label="O_element : 0.710"  # scripted group (container) (typed FeaturePython)
  n = 0.71
FEATURE [App::DocumentObjectGroupPython] Na_element011  label="Na_element : 0.098"  # scripted group (container) (typed FeaturePython)
  n = 0.001
FEATURE [App::DocumentObjectGroupPython] P_element007  label="P_element : 0.002"  # scripted group (container) (typed FeaturePython)
  n = 0.002
FEATURE [App::DocumentObjectGroupPython] S_element017  label="S_element : 0.018"  # scripted group (container) (typed FeaturePython)
  n = 0.003
FEATURE [App::DocumentObjectGroupPython] Cl_element016  label="Cl_element : 0.589"  # scripted group (container) (typed FeaturePython)
  n = 0.001
FEATURE [App::DocumentObjectGroupPython] K_element006  label="K_element : 0.004"  # scripted group (container) (typed FeaturePython)
  n = 0.004
FEATURE [App::DocumentObjectGroupPython] G4_MUSCLE_SKELETAL_ICRP  # scripted group (container) (typed FeaturePython)
  Dunit = g/cm3
  Dvalue = 1.05
  Group = -> [H_element057,C_element063,N_element025,O_element065,Na_element011,P_element007,S_element017,Cl_element016,K_element006]
  conduct = 2
  density = 1
  expand = 3
  formula = G4_MUSCLE_SKELETAL_ICRP
  name = G4_MUSCLE_SKELETAL_ICRP
  specific = 4
FEATURE [App::DocumentObjectGroupPython] H_element058  label="H_element : 0.137"  # scripted group (container) (typed FeaturePython)
  n = 0.102102
FEATURE [App::DocumentObjectGroupPython] C_element064  label="C_element : 0.123"  # scripted group (container) (typed FeaturePython)
  n = 0.123123
FEATURE [App::DocumentObjectGroupPython] N_element026  label="N_element : 0.756"  # scripted group (container) (typed FeaturePython)
  n = 0.035035
FEATURE [App::DocumentObjectGroupPython] O_element066  label="O_element : 0.730"  # scripted group (container) (typed FeaturePython)
  n = 0.72973
FEATURE [App::DocumentObjectGroupPython] Na_element012  label="Na_element : 0.099"  # scripted group (container) (typed FeaturePython)
  n = 0.001001
FEATURE [App::DocumentObjectGroupPython] P_element008  label="P_element : 0.106"  # scripted group (container) (typed FeaturePython)
  n = 0.002002
FEATURE [App::DocumentObjectGroupPython] S_element018  label="S_element : 0.019"  # scripted group (container) (typed FeaturePython)
  n = 0.004004
FEATURE [App::DocumentObjectGroupPython] K_element007  label="K_element : 0.016"  # scripted group (container) (typed FeaturePython)
  n = 0.003003
FEATURE [App::DocumentObjectGroupPython] G4_MUSCLE_STRIATED_ICRU  # scripted group (container) (typed FeaturePython)
  Dunit = g/cm3
  Dvalue = 1.04
  Group = -> [H_element058,C_element064,N_element026,O_element066,Na_element012,P_element008,S_element018,K_element007]
  conduct = 2
  density = 1
  expand = 3
  formula = G4_MUSCLE_STRIATED_ICRU
  name = G4_MUSCLE_STRIATED_ICRU
  specific = 4
FEATURE [App::DocumentObjectGroupPython] H_element059  label="H_element : 0.098"  # scripted group (container) (typed FeaturePython)
  n = 0.0982341
FEATURE [App::DocumentObjectGroupPython] C_element065  label="C_element : 0.156"  # scripted group (container) (typed FeaturePython)
  n = 0.156214
FEATURE [App::DocumentObjectGroupPython] N_element027  label="N_element : 0.757"  # scripted group (container) (typed FeaturePython)
  n = 0.035451
FEATURE [App::DocumentObjectGroupPython] O_element067  label="O_element : 0.880"  # scripted group (container) (typed FeaturePython)
  n = 0.710101
FEATURE [App::DocumentObjectGroupPython] G4_MUSCLE_WITH_SUCROSE  # scripted group (container) (typed FeaturePython)
  Dunit = g/cm3
  Dvalue = 1.11
  Group = -> [H_element059,C_element065,N_element027,O_element067]
  conduct = 2
  density = 1
  expand = 3
  formula = G4_MUSCLE_WITH_SUCROSE
  name = G4_MUSCLE_WITH_SUCROSE
  specific = 4
FEATURE [App::DocumentObjectGroupPython] H_element060  label="H_element : 0.138"  # scripted group (container) (typed FeaturePython)
  n = 0.101969
FEATURE [App::DocumentObjectGroupPython] C_element066  label="C_element : 0.120"  # scripted group (container) (typed FeaturePython)
  n = 0.120058
FEATURE [App::DocumentObjectGroupPython] N_element028  label="N_element : 0.758"  # scripted group (container) (typed FeaturePython)
  n = 0.035451
FEATURE [App::DocumentObjectGroupPython] O_element068  label="O_element : 0.743"  # scripted group (container) (typed FeaturePython)
  n = 0.742522
FEATURE [App::DocumentObjectGroupPython] G4_MUSCLE_WITHOUT_SUCROSE  # scripted group (container) (typed FeaturePython)
  Dunit = g/cm3
  Dvalue = 1.07
  Group = -> [H_element060,C_element066,N_element028,O_element068]
  conduct = 2
  density = 1
  expand = 3
  formula = G4_MUSCLE_WITHOUT_SUCROSE
  name = G4_MUSCLE_WITHOUT_SUCROSE
  specific = 4
FEATURE [App::DocumentObjectGroupPython] C_element067  label="C_element : 10"  # scripted group (container) (typed FeaturePython)
  n = 10
  ref = C_element
FEATURE [App::DocumentObjectGroupPython] H_element061  label="H_element : 030"  # scripted group (container) (typed FeaturePython)
  n = 8
  ref = H_element
FEATURE [App::DocumentObjectGroupPython] G4_NAPHTHALENE  # scripted group (container) (typed FeaturePython)
  Dunit = g/cm3
  Dvalue = 1.145
  Group = -> [C_element067,H_element061]
  conduct = 2
  density = 1
  expand = 3
  formula = G4_NAPHTHALENE
  name = G4_NAPHTHALENE
  specific = 4
FEATURE [App::DocumentObjectGroupPython] C_element068  label="C_element : 034"  # scripted group (container) (typed FeaturePython)
  n = 6
  ref = C_element
FEATURE [App::DocumentObjectGroupPython] H_element062  label="H_element : 031"  # scripted group (container) (typed FeaturePython)
  n = 5
  ref = H_element
FEATURE [App::DocumentObjectGroupPython] N_element029  label="N_element : 012"  # scripted group (container) (typed FeaturePython)
  n = 1
  ref = N_element
FEATURE [App::DocumentObjectGroupPython] O_element069  label="O_element : 034"  # scripted group (container) (typed FeaturePython)
  n = 2
  ref = O_element
FEATURE [App::DocumentObjectGroupPython] G4_NITROBENZENE  # scripted group (container) (typed FeaturePython)
  Dunit = g/cm3
  Dvalue = 1.19867
  Group = -> [C_element068,H_element062,N_element029,O_element069]
  conduct = 2
  density = 1
  expand = 3
  formula = G4_NITROBENZENE
  name = G4_NITROBENZENE
  specific = 4
FEATURE [App::DocumentObjectGroupPython] N_element030  label="N_element : 013"  # scripted group (container) (typed FeaturePython)
  n = 2
  ref = N_element
FEATURE [App::DocumentObjectGroupPython] O_element070  label="O_element : 035"  # scripted group (container) (typed FeaturePython)
  n = 1
  ref = O_element
FEATURE [App::DocumentObjectGroupPython] G4_NITROUS_OXIDE  # scripted group (container) (typed FeaturePython)
  Dunit = g/cm3
  Dvalue = 0.00183094
  Group = -> [N_element030,O_element070]
  conduct = 2
  density = 1
  expand = 3
  formula = G4_NITROUS_OXIDE
  name = G4_NITROUS_OXIDE
  specific = 4
FEATURE [App::DocumentObjectGroupPython] H_element063  label="H_element : 0.104"  # scripted group (container) (typed FeaturePython)
  n = 0.103509
FEATURE [App::DocumentObjectGroupPython] C_element069  label="C_element : 0.648"  # scripted group (container) (typed FeaturePython)
  n = 0.648416
FEATURE [App::DocumentObjectGroupPython] N_element031  label="N_element : 0.100"  # scripted group (container) (typed FeaturePython)
  n = 0.0995361
FEATURE [App::DocumentObjectGroupPython] O_element071  label="O_element : 0.149"  # scripted group (container) (typed FeaturePython)
  n = 0.148539
FEATURE [App::DocumentObjectGroupPython] G4_NYLON_8062  label="G4_NYLON-8062"  # scripted group (container) (typed FeaturePython)
  Dunit = g/cm3
  Dvalue = 1.08
  Group = -> [H_element063,C_element069,N_element031,O_element071]
  conduct = 2
  density = 1
  expand = 3
  formula = G4_NYLON-8062
  name = G4_NYLON-8062
  specific = 4
FEATURE [App::DocumentObjectGroupPython] C_element070  label="C_element : 035"  # scripted group (container) (typed FeaturePython)
  n = 6
  ref = C_element
FEATURE [App::DocumentObjectGroupPython] H_element064  label="H_element : 11"  # scripted group (container) (typed FeaturePython)
  n = 11
  ref = H_element
FEATURE [App::DocumentObjectGroupPython] N_element032  label="N_element : 014"  # scripted group (container) (typed FeaturePython)
  n = 1
  ref = N_element
FEATURE [App::DocumentObjectGroupPython] O_element072  label="O_element : 036"  # scripted group (container) (typed FeaturePython)
  n = 1
  ref = O_element
FEATURE [App::DocumentObjectGroupPython] G4_NYLON_6_6  label="G4_NYLON-6-6"  # scripted group (container) (typed FeaturePython)
  Dunit = g/cm3
  Dvalue = 1.14
  Group = -> [C_element070,H_element064,N_element032,O_element072]
  conduct = 2
  density = 1
  expand = 3
  formula = G4_NYLON-6-6
  name = G4_NYLON-6-6
  specific = 4
FEATURE [App::DocumentObjectGroupPython] H_element065  label="H_element : 0.139"  # scripted group (container) (typed FeaturePython)
  n = 0.107062
FEATURE [App::DocumentObjectGroupPython] C_element071  label="C_element : 0.680"  # scripted group (container) (typed FeaturePython)
  n = 0.680449
FEATURE [App::DocumentObjectGroupPython] N_element033  label="N_element : 0.099"  # scripted group (container) (typed FeaturePython)
  n = 0.099189
FEATURE [App::DocumentObjectGroupPython] O_element073  label="O_element : 0.113"  # scripted group (container) (typed FeaturePython)
  n = 0.1133
FEATURE [App::DocumentObjectGroupPython] G4_NYLON_6_10  label="G4_NYLON-6-10"  # scripted group (container) (typed FeaturePython)
  Dunit = g/cm3
  Dvalue = 1.14
  Group = -> [H_element065,C_element071,N_element033,O_element073]
  conduct = 2
  density = 1
  expand = 3
  formula = G4_NYLON-6-10
  name = G4_NYLON-6-10
  specific = 4
FEATURE [App::DocumentObjectGroupPython] H_element066  label="H_element : 0.140"  # scripted group (container) (typed FeaturePython)
  n = 0.115476
FEATURE [App::DocumentObjectGroupPython] C_element072  label="C_element : 0.721"  # scripted group (container) (typed FeaturePython)
  n = 0.720818
FEATURE [App::DocumentObjectGroupPython] N_element034  label="N_element : 0.076"  # scripted group (container) (typed FeaturePython)
  n = 0.0764169
FEATURE [App::DocumentObjectGroupPython] O_element074  label="O_element : 0.087"  # scripted group (container) (typed FeaturePython)
  n = 0.0872889
FEATURE [App::DocumentObjectGroupPython] G4_NYLON_11_RILSAN  label="G4_NYLON-11_RILSAN"  # scripted group (container) (typed FeaturePython)
  Dunit = g/cm3
  Dvalue = 1.425
  Group = -> [H_element066,C_element072,N_element034,O_element074]
  conduct = 2
  density = 1
  expand = 3
  formula = G4_NYLON-11_RILSAN
  name = G4_NYLON-11_RILSAN
  specific = 4
FEATURE [App::DocumentObjectGroupPython] C_element073  label="C_element : 8"  # scripted group (container) (typed FeaturePython)
  n = 8
  ref = C_element
FEATURE [App::DocumentObjectGroupPython] H_element067  label="H_element : 18"  # scripted group (container) (typed FeaturePython)
  n = 18
  ref = H_element
FEATURE [App::DocumentObjectGroupPython] G4_OCTANE  # scripted group (container) (typed FeaturePython)
  Dunit = g/cm3
  Dvalue = 0.7026
  Group = -> [C_element073,H_element067]
  conduct = 2
  density = 1
  expand = 3
  formula = G4_OCTANE
  name = G4_OCTANE
  specific = 4
FEATURE [App::DocumentObjectGroupPython] C_element074  label="C_element : 25"  # scripted group (container) (typed FeaturePython)
  n = 25
  ref = C_element
FEATURE [App::DocumentObjectGroupPython] H_element068  label="H_element : 52"  # scripted group (container) (typed FeaturePython)
  n = 52
  ref = H_element
FEATURE [App::DocumentObjectGroupPython] G4_PARAFFIN  # scripted group (container) (typed FeaturePython)
  Dunit = g/cm3
  Dvalue = 0.93
  Group = -> [C_element074,H_element068]
  conduct = 2
  density = 1
  expand = 3
  formula = G4_PARAFFIN
  name = G4_PARAFFIN
  specific = 4
FEATURE [App::DocumentObjectGroupPython] C_element075  label="C_element : 036"  # scripted group (container) (typed FeaturePython)
  n = 5
  ref = C_element
FEATURE [App::DocumentObjectGroupPython] H_element069  label="H_element : 032"  # scripted group (container) (typed FeaturePython)
  n = 12
  ref = H_element
FEATURE [App::DocumentObjectGroupPython] G4_N_PENTANE  label="G4_N-PENTANE"  # scripted group (container) (typed FeaturePython)
  Dunit = g/cm3
  Dvalue = 0.6262
  Group = -> [C_element075,H_element069]
  conduct = 2
  density = 1
  expand = 3
  formula = G4_N-PENTANE
  name = G4_N-PENTANE
  specific = 4
FEATURE [App::DocumentObjectGroupPython] H_element070  label="H_element : 0.014"  # scripted group (container) (typed FeaturePython)
  n = 0.0141
FEATURE [App::DocumentObjectGroupPython] C_element076  label="C_element : 0.072"  # scripted group (container) (typed FeaturePython)
  n = 0.072261
FEATURE [App::DocumentObjectGroupPython] N_element035  label="N_element : 0.019"  # scripted group (container) (typed FeaturePython)
  n = 0.01932
FEATURE [App::DocumentObjectGroupPython] O_element075  label="O_element : 0.066"  # scripted group (container) (typed FeaturePython)
  n = 0.066101
FEATURE [App::DocumentObjectGroupPython] S_element019  label="S_element : 0.020"  # scripted group (container) (typed FeaturePython)
  n = 0.00189
FEATURE [App::DocumentObjectGroupPython] Br_element004  label="Br_element : 0.349"  # scripted group (container) (typed FeaturePython)
  n = 0.349103
FEATURE [App::DocumentObjectGroupPython] Ag_element001  label="Ag_element : 0.474"  # scripted group (container) (typed FeaturePython)
  n = 0.474105
FEATURE [App::DocumentObjectGroupPython] I_element005  label="I_element : 0.003"  # scripted group (container) (typed FeaturePython)
  n = 0.00312
FEATURE [App::DocumentObjectGroupPython] G4_PHOTO_EMULSION  # scripted group (container) (typed FeaturePython)
  Dunit = g/cm3
  Dvalue = 3.815
  Group = -> [H_element070,C_element076,N_element035,O_element075,S_element019,Br_element004,Ag_element001,I_element005]
  conduct = 2
  density = 1
  expand = 3
  formula = G4_PHOTO_EMULSION
  name = G4_PHOTO_EMULSION
  specific = 4
FEATURE [App::DocumentObjectGroupPython] C_element077  label="C_element : 9"  # scripted group (container) (typed FeaturePython)
  n = 9
  ref = C_element
FEATURE [App::DocumentObjectGroupPython] H_element071  label="H_element : 033"  # scripted group (container) (typed FeaturePython)
  n = 10
  ref = H_element
FEATURE [App::DocumentObjectGroupPython] G4_PLASTIC_SC_VINYLTOLUENE  # scripted group (container) (typed FeaturePython)
  Dunit = g/cm3
  Dvalue = 1.032
  Group = -> [C_element077,H_element071]
  conduct = 2
  density = 1
  expand = 3
  formula = G4_PLASTIC_SC_VINYLTOLUENE
  name = G4_PLASTIC_SC_VINYLTOLUENE
  specific = 4
FEATURE [App::DocumentObjectGroupPython] Pu_element001  label="Pu_element : 1"  # scripted group (container) (typed FeaturePython)
  n = 1
  ref = Pu_element
FEATURE [App::DocumentObjectGroupPython] O_element076  label="O_element : 037"  # scripted group (container) (typed FeaturePython)
  n = 2
  ref = O_element
FEATURE [App::DocumentObjectGroupPython] G4_PLUTONIUM_DIOXIDE  # scripted group (container) (typed FeaturePython)
  Dunit = g/cm3
  Dvalue = 11.46
  Group = -> [Pu_element001,O_element076]
  conduct = 2
  density = 1
  expand = 3
  formula = G4_PLUTONIUM_DIOXIDE
  name = G4_PLUTONIUM_DIOXIDE
  specific = 4
FEATURE [App::DocumentObjectGroupPython] C_element078  label="C_element : 037"  # scripted group (container) (typed FeaturePython)
  n = 3
  ref = C_element
FEATURE [App::DocumentObjectGroupPython] H_element072  label="H_element : 034"  # scripted group (container) (typed FeaturePython)
  n = 3
  ref = H_element
FEATURE [App::DocumentObjectGroupPython] N_element036  label="N_element : 015"  # scripted group (container) (typed FeaturePython)
  n = 1
  ref = N_element
FEATURE [App::DocumentObjectGroupPython] G4_POLYACRYLONITRILE  # scripted group (container) (typed FeaturePython)
  Dunit = g/cm3
  Dvalue = 1.17
  Group = -> [C_element078,H_element072,N_element036]
  conduct = 2
  density = 1
  expand = 3
  formula = G4_POLYACRYLONITRILE
  name = G4_POLYACRYLONITRILE
  specific = 4
FEATURE [App::DocumentObjectGroupPython] C_element079  label="C_element : 16"  # scripted group (container) (typed FeaturePython)
  n = 16
  ref = C_element
FEATURE [App::DocumentObjectGroupPython] H_element073  label="H_element : 035"  # scripted group (container) (typed FeaturePython)
  n = 14
  ref = H_element
FEATURE [App::DocumentObjectGroupPython] O_element077  label="O_element : 038"  # scripted group (container) (typed FeaturePython)
  n = 3
  ref = O_element
FEATURE [App::DocumentObjectGroupPython] G4_POLYCARBONATE  # scripted group (container) (typed FeaturePython)
  Dunit = g/cm3
  Dvalue = 1.2
  Group = -> [C_element079,H_element073,O_element077]
  conduct = 2
  density = 1
  expand = 3
  formula = G4_POLYCARBONATE
  name = G4_POLYCARBONATE
  specific = 4
FEATURE [App::DocumentObjectGroupPython] C_element080  label="C_element : 038"  # scripted group (container) (typed FeaturePython)
  n = 8
  ref = C_element
FEATURE [App::DocumentObjectGroupPython] H_element074  label="H_element : 036"  # scripted group (container) (typed FeaturePython)
  n = 7
  ref = H_element
FEATURE [App::DocumentObjectGroupPython] Cl_element017  label="Cl_element : 007"  # scripted group (container) (typed FeaturePython)
  n = 1
  ref = Cl_element
FEATURE [App::DocumentObjectGroupPython] G4_POLYCHLOROSTYRENE  # scripted group (container) (typed FeaturePython)
  Dunit = g/cm3
  Dvalue = 1.3
  Group = -> [C_element080,H_element074,Cl_element017]
  conduct = 2
  density = 1
  expand = 3
  formula = G4_POLYCHLOROSTYRENE
  name = G4_POLYCHLOROSTYRENE
  specific = 4
FEATURE [App::DocumentObjectGroupPython] C_element081  label="C_element : 039"  # scripted group (container) (typed FeaturePython)
  n = 1
  ref = C_element
FEATURE [App::DocumentObjectGroupPython] H_element075  label="H_element : 037"  # scripted group (container) (typed FeaturePython)
  n = 2
  ref = H_element
FEATURE [App::DocumentObjectGroupPython] G4_POLYETHYLENE  # scripted group (container) (typed FeaturePython)
  Dunit = g/cm3
  Dvalue = 0.94
  Group = -> [C_element081,H_element075]
  conduct = 2
  density = 1
  expand = 3
  formula = G4_POLYETHYLENE
  name = G4_POLYETHYLENE
  specific = 4
FEATURE [App::DocumentObjectGroupPython] C_element082  label="C_element : 040"  # scripted group (container) (typed FeaturePython)
  n = 10
  ref = C_element
FEATURE [App::DocumentObjectGroupPython] H_element076  label="H_element : 038"  # scripted group (container) (typed FeaturePython)
  n = 8
  ref = H_element
FEATURE [App::DocumentObjectGroupPython] O_element078  label="O_element : 039"  # scripted group (container) (typed FeaturePython)
  n = 4
  ref = O_element
FEATURE [App::DocumentObjectGroupPython] G4_MYLAR  # scripted group (container) (typed FeaturePython)
  Dunit = g/cm3
  Dvalue = 1.4
  Group = -> [C_element082,H_element076,O_element078]
  conduct = 2
  density = 1
  expand = 3
  formula = G4_MYLAR
  name = G4_MYLAR
  specific = 4
FEATURE [App::DocumentObjectGroupPython] C_element083  label="C_element : 041"  # scripted group (container) (typed FeaturePython)
  n = 5
  ref = C_element
FEATURE [App::DocumentObjectGroupPython] H_element077  label="H_element : 039"  # scripted group (container) (typed FeaturePython)
  n = 8
  ref = H_element
FEATURE [App::DocumentObjectGroupPython] O_element079  label="O_element : 040"  # scripted group (container) (typed FeaturePython)
  n = 2
  ref = O_element
FEATURE [App::DocumentObjectGroupPython] G4_PLEXIGLASS  # scripted group (container) (typed FeaturePython)
  Dunit = g/cm3
  Dvalue = 1.19
  Group = -> [C_element083,H_element077,O_element079]
  conduct = 2
  density = 1
  expand = 3
  formula = G4_PLEXIGLASS
  name = G4_PLEXIGLASS
  specific = 4
FEATURE [App::DocumentObjectGroupPython] C_element084  label="C_element : 042"  # scripted group (container) (typed FeaturePython)
  n = 1
  ref = C_element
FEATURE [App::DocumentObjectGroupPython] H_element078  label="H_element : 040"  # scripted group (container) (typed FeaturePython)
  n = 2
  ref = H_element
FEATURE [App::DocumentObjectGroupPython] O_element080  label="O_element : 041"  # scripted group (container) (typed FeaturePython)
  n = 1
  ref = O_element
FEATURE [App::DocumentObjectGroupPython] G4_POLYOXYMETHYLENE  # scripted group (container) (typed FeaturePython)
  Dunit = g/cm3
  Dvalue = 1.425
  Group = -> [C_element084,H_element078,O_element080]
  conduct = 2
  density = 1
  expand = 3
  formula = G4_POLYOXYMETHYLENE
  name = G4_POLYOXYMETHYLENE
  specific = 4
FEATURE [App::DocumentObjectGroupPython] C_element085  label="C_element : 043"  # scripted group (container) (typed FeaturePython)
  n = 2
  ref = C_element
FEATURE [App::DocumentObjectGroupPython] H_element079  label="H_element : 041"  # scripted group (container) (typed FeaturePython)
  n = 4
  ref = H_element
FEATURE [App::DocumentObjectGroupPython] G4_POLYPROPYLENE  # scripted group (container) (typed FeaturePython)
  Dunit = g/cm3
  Dvalue = 0.9
  Group = -> [C_element085,H_element079]
  conduct = 2
  density = 1
  expand = 3
  formula = G4_POLYPROPYLENE
  name = G4_POLYPROPYLENE
  specific = 4
FEATURE [App::DocumentObjectGroupPython] C_element086  label="C_element : 044"  # scripted group (container) (typed FeaturePython)
  n = 8
  ref = C_element
FEATURE [App::DocumentObjectGroupPython] H_element080  label="H_element : 042"  # scripted group (container) (typed FeaturePython)
  n = 8
  ref = H_element
FEATURE [App::DocumentObjectGroupPython] G4_POLYSTYRENE  # scripted group (container) (typed FeaturePython)
  Dunit = g/cm3
  Dvalue = 1.06
  Group = -> [C_element086,H_element080]
  conduct = 2
  density = 1
  expand = 3
  formula = G4_POLYSTYRENE
  name = G4_POLYSTYRENE
  specific = 4
FEATURE [App::DocumentObjectGroupPython] C_element087  label="C_element : 045"  # scripted group (container) (typed FeaturePython)
  n = 2
  ref = C_element
FEATURE [App::DocumentObjectGroupPython] F_element014  label="F_element : 4"  # scripted group (container) (typed FeaturePython)
  n = 4
  ref = F_element
FEATURE [App::DocumentObjectGroupPython] G4_TEFLON  # scripted group (container) (typed FeaturePython)
  Dunit = g/cm3
  Dvalue = 2.2
  Group = -> [C_element087,F_element014]
  conduct = 2
  density = 1
  expand = 3
  formula = G4_TEFLON
  name = G4_TEFLON
  specific = 4
FEATURE [App::DocumentObjectGroupPython] C_element088  label="C_element : 046"  # scripted group (container) (typed FeaturePython)
  n = 2
  ref = C_element
FEATURE [App::DocumentObjectGroupPython] F_element015  label="F_element : 006"  # scripted group (container) (typed FeaturePython)
  n = 3
  ref = F_element
FEATURE [App::DocumentObjectGroupPython] Cl_element018  label="Cl_element : 008"  # scripted group (container) (typed FeaturePython)
  n = 1
  ref = Cl_element
FEATURE [App::DocumentObjectGroupPython] G4_POLYTRIFLUOROCHLOROETHYLENE  # scripted group (container) (typed FeaturePython)
  Dunit = g/cm3
  Dvalue = 2.1
  Group = -> [C_element088,F_element015,Cl_element018]
  conduct = 2
  density = 1
  expand = 3
  formula = G4_POLYTRIFLUOROCHLOROETHYLENE
  name = G4_POLYTRIFLUOROCHLOROETHYLENE
  specific = 4
FEATURE [App::DocumentObjectGroupPython] C_element089  label="C_element : 047"  # scripted group (container) (typed FeaturePython)
  n = 4
  ref = C_element
FEATURE [App::DocumentObjectGroupPython] H_element081  label="H_element : 043"  # scripted group (container) (typed FeaturePython)
  n = 6
  ref = H_element
FEATURE [App::DocumentObjectGroupPython] O_element081  label="O_element : 042"  # scripted group (container) (typed FeaturePython)
  n = 2
  ref = O_element
FEATURE [App::DocumentObjectGroupPython] G4_POLYVINYL_ACETATE  # scripted group (container) (typed FeaturePython)
  Dunit = g/cm3
  Dvalue = 1.19
  Group = -> [C_element089,H_element081,O_element081]
  conduct = 2
  density = 1
  expand = 3
  formula = G4_POLYVINYL_ACETATE
  name = G4_POLYVINYL_ACETATE
  specific = 4
FEATURE [App::DocumentObjectGroupPython] C_element090  label="C_element : 048"  # scripted group (container) (typed FeaturePython)
  n = 2
  ref = C_element
FEATURE [App::DocumentObjectGroupPython] H_element082  label="H_element : 044"  # scripted group (container) (typed FeaturePython)
  n = 4
  ref = H_element
FEATURE [App::DocumentObjectGroupPython] O_element082  label="O_element : 043"  # scripted group (container) (typed FeaturePython)
  n = 1
  ref = O_element
FEATURE [App::DocumentObjectGroupPython] G4_POLYVINYL_ALCOHOL  # scripted group (container) (typed FeaturePython)
  Dunit = g/cm3
  Dvalue = 1.3
  Group = -> [C_element090,H_element082,O_element082]
  conduct = 2
  density = 1
  expand = 3
  formula = G4_POLYVINYL_ALCOHOL
  name = G4_POLYVINYL_ALCOHOL
  specific = 4
FEATURE [App::DocumentObjectGroupPython] C_element091  label="C_element : 049"  # scripted group (container) (typed FeaturePython)
  n = 8
  ref = C_element
FEATURE [App::DocumentObjectGroupPython] H_element083  label="H_element : 045"  # scripted group (container) (typed FeaturePython)
  n = 14
  ref = H_element
FEATURE [App::DocumentObjectGroupPython] O_element083  label="O_element : 044"  # scripted group (container) (typed FeaturePython)
  n = 2
  ref = O_element
FEATURE [App::DocumentObjectGroupPython] G4_POLYVINYL_BUTYRAL  # scripted group (container) (typed FeaturePython)
  Dunit = g/cm3
  Dvalue = 1.12
  Group = -> [C_element091,H_element083,O_element083]
  conduct = 2
  density = 1
  expand = 3
  formula = G4_POLYVINYL_BUTYRAL
  name = G4_POLYVINYL_BUTYRAL
  specific = 4
FEATURE [App::DocumentObjectGroupPython] C_element092  label="C_element : 050"  # scripted group (container) (typed FeaturePython)
  n = 2
  ref = C_element
FEATURE [App::DocumentObjectGroupPython] H_element084  label="H_element : 046"  # scripted group (container) (typed FeaturePython)
  n = 3
  ref = H_element
FEATURE [App::DocumentObjectGroupPython] Cl_element019  label="Cl_element : 009"  # scripted group (container) (typed FeaturePython)
  n = 1
  ref = Cl_element
FEATURE [App::DocumentObjectGroupPython] G4_POLYVINYL_CHLORIDE  # scripted group (container) (typed FeaturePython)
  Dunit = g/cm3
  Dvalue = 1.3
  Group = -> [C_element092,H_element084,Cl_element019]
  conduct = 2
  density = 1
  expand = 3
  formula = G4_POLYVINYL_CHLORIDE
  name = G4_POLYVINYL_CHLORIDE
  specific = 4
FEATURE [App::DocumentObjectGroupPython] C_element093  label="C_element : 051"  # scripted group (container) (typed FeaturePython)
  n = 2
  ref = C_element
FEATURE [App::DocumentObjectGroupPython] H_element085  label="H_element : 047"  # scripted group (container) (typed FeaturePython)
  n = 2
  ref = H_element
FEATURE [App::DocumentObjectGroupPython] Cl_element020  label="Cl_element : 010"  # scripted group (container) (typed FeaturePython)
  n = 2
  ref = Cl_element
FEATURE [App::DocumentObjectGroupPython] G4_POLYVINYLIDENE_CHLORIDE  # scripted group (container) (typed FeaturePython)
  Dunit = g/cm3
  Dvalue = 1.7
  Group = -> [C_element093,H_element085,Cl_element020]
  conduct = 2
  density = 1
  expand = 3
  formula = G4_POLYVINYLIDENE_CHLORIDE
  name = G4_POLYVINYLIDENE_CHLORIDE
  specific = 4
FEATURE [App::DocumentObjectGroupPython] C_element094  label="C_element : 052"  # scripted group (container) (typed FeaturePython)
  n = 2
  ref = C_element
FEATURE [App::DocumentObjectGroupPython] H_element086  label="H_element : 048"  # scripted group (container) (typed FeaturePython)
  n = 2
  ref = H_element
FEATURE [App::DocumentObjectGroupPython] F_element016  label="F_element : 007"  # scripted group (container) (typed FeaturePython)
  n = 2
  ref = F_element
FEATURE [App::DocumentObjectGroupPython] G4_POLYVINYLIDENE_FLUORIDE  # scripted group (container) (typed FeaturePython)
  Dunit = g/cm3
  Dvalue = 1.76
  Group = -> [C_element094,H_element086,F_element016]
  conduct = 2
  density = 1
  expand = 3
  formula = G4_POLYVINYLIDENE_FLUORIDE
  name = G4_POLYVINYLIDENE_FLUORIDE
  specific = 4
FEATURE [App::DocumentObjectGroupPython] C_element095  label="C_element : 053"  # scripted group (container) (typed FeaturePython)
  n = 6
  ref = C_element
FEATURE [App::DocumentObjectGroupPython] H_element087  label="H_element : 9"  # scripted group (container) (typed FeaturePython)
  n = 9
  ref = H_element
FEATURE [App::DocumentObjectGroupPython] N_element037  label="N_element : 016"  # scripted group (container) (typed FeaturePython)
  n = 1
  ref = N_element
FEATURE [App::DocumentObjectGroupPython] O_element084  label="O_element : 045"  # scripted group (container) (typed FeaturePython)
  n = 1
  ref = O_element
FEATURE [App::DocumentObjectGroupPython] G4_POLYVINYL_PYRROLIDONE  # scripted group (container) (typed FeaturePython)
  Dunit = g/cm3
  Dvalue = 1.25
  Group = -> [C_element095,H_element087,N_element037,O_element084]
  conduct = 2
  density = 1
  expand = 3
  formula = G4_POLYVINYL_PYRROLIDONE
  name = G4_POLYVINYL_PYRROLIDONE
  specific = 4
FEATURE [App::DocumentObjectGroupPython] K_element008  label="K_element : 1"  # scripted group (container) (typed FeaturePython)
  n = 1
  ref = K_element
FEATURE [App::DocumentObjectGroupPython] I_element006  label="I_element : 003"  # scripted group (container) (typed FeaturePython)
  n = 1
  ref = I_element
FEATURE [App::DocumentObjectGroupPython] G4_POTASSIUM_IODIDE  # scripted group (container) (typed FeaturePython)
  Dunit = g/cm3
  Dvalue = 3.13
  Group = -> [K_element008,I_element006]
  conduct = 2
  density = 1
  expand = 3
  formula = G4_POTASSIUM_IODIDE
  name = G4_POTASSIUM_IODIDE
  specific = 4
FEATURE [App::DocumentObjectGroupPython] K_element009  label="K_element : 2"  # scripted group (container) (typed FeaturePython)
  n = 2
  ref = K_element
FEATURE [App::DocumentObjectGroupPython] O_element085  label="O_element : 046"  # scripted group (container) (typed FeaturePython)
  n = 1
  ref = O_element
FEATURE [App::DocumentObjectGroupPython] G4_POTASSIUM_OXIDE  # scripted group (container) (typed FeaturePython)
  Dunit = g/cm3
  Dvalue = 2.32
  Group = -> [K_element009,O_element085]
  conduct = 2
  density = 1
  expand = 3
  formula = G4_POTASSIUM_OXIDE
  name = G4_POTASSIUM_OXIDE
  specific = 4
FEATURE [App::DocumentObjectGroupPython] C_element096  label="C_element : 054"  # scripted group (container) (typed FeaturePython)
  n = 3
  ref = C_element
FEATURE [App::DocumentObjectGroupPython] H_element088  label="H_element : 049"  # scripted group (container) (typed FeaturePython)
  n = 8
  ref = H_element
FEATURE [App::DocumentObjectGroupPython] G4_PROPANE  # scripted group (container) (typed FeaturePython)
  Dunit = g/cm3
  Dvalue = 0.00187939
  Group = -> [C_element096,H_element088]
  conduct = 2
  density = 1
  expand = 3
  formula = G4_PROPANE
  name = G4_PROPANE
  specific = 4
FEATURE [App::DocumentObjectGroupPython] C_element097  label="C_element : 055"  # scripted group (container) (typed FeaturePython)
  n = 3
  ref = C_element
FEATURE [App::DocumentObjectGroupPython] H_element089  label="H_element : 050"  # scripted group (container) (typed FeaturePython)
  n = 8
  ref = H_element
FEATURE [App::DocumentObjectGroupPython] G4_lPROPANE  # scripted group (container) (typed FeaturePython)
  Dunit = g/cm3
  Dvalue = 0.43
  Group = -> [C_element097,H_element089]
  conduct = 2
  density = 1
  expand = 3
  formula = G4_lPROPANE
  name = G4_lPROPANE
  specific = 4
FEATURE [App::DocumentObjectGroupPython] C_element098  label="C_element : 056"  # scripted group (container) (typed FeaturePython)
  n = 3
  ref = C_element
FEATURE [App::DocumentObjectGroupPython] H_element090  label="H_element : 051"  # scripted group (container) (typed FeaturePython)
  n = 8
  ref = H_element
FEATURE [App::DocumentObjectGroupPython] O_element086  label="O_element : 047"  # scripted group (container) (typed FeaturePython)
  n = 1
  ref = O_element
FEATURE [App::DocumentObjectGroupPython] G4_N_PROPYL_ALCOHOL  label="G4_N-PROPYL_ALCOHOL"  # scripted group (container) (typed FeaturePython)
  Dunit = g/cm3
  Dvalue = 0.8035
  Group = -> [C_element098,H_element090,O_element086]
  conduct = 2
  density = 1
  expand = 3
  formula = G4_N-PROPYL_ALCOHOL
  name = G4_N-PROPYL_ALCOHOL
  specific = 4
FEATURE [App::DocumentObjectGroupPython] C_element099  label="C_element : 057"  # scripted group (container) (typed FeaturePython)
  n = 5
  ref = C_element
FEATURE [App::DocumentObjectGroupPython] H_element091  label="H_element : 052"  # scripted group (container) (typed FeaturePython)
  n = 5
  ref = H_element
FEATURE [App::DocumentObjectGroupPython] N_element038  label="N_element : 017"  # scripted group (container) (typed FeaturePython)
  n = 1
  ref = N_element
FEATURE [App::DocumentObjectGroupPython] G4_PYRIDINE  # scripted group (container) (typed FeaturePython)
  Dunit = g/cm3
  Dvalue = 0.9819
  Group = -> [C_element099,H_element091,N_element038]
  conduct = 2
  density = 1
  expand = 3
  formula = G4_PYRIDINE
  name = G4_PYRIDINE
  specific = 4
FEATURE [App::DocumentObjectGroupPython] H_element092  label="H_element : 0.144"  # scripted group (container) (typed FeaturePython)
  n = 0.143711
FEATURE [App::DocumentObjectGroupPython] C_element100  label="C_element : 0.856"  # scripted group (container) (typed FeaturePython)
  n = 0.856289
FEATURE [App::DocumentObjectGroupPython] G4_RUBBER_BUTYL  # scripted group (container) (typed FeaturePython)
  Dunit = g/cm3
  Dvalue = 0.92
  Group = -> [H_element092,C_element100]
  conduct = 2
  density = 1
  expand = 3
  formula = G4_RUBBER_BUTYL
  name = G4_RUBBER_BUTYL
  specific = 4
FEATURE [App::DocumentObjectGroupPython] H_element093  label="H_element : 0.118"  # scripted group (container) (typed FeaturePython)
  n = 0.118371
FEATURE [App::DocumentObjectGroupPython] C_element101  label="C_element : 0.882"  # scripted group (container) (typed FeaturePython)
  n = 0.881629
FEATURE [App::DocumentObjectGroupPython] G4_RUBBER_NATURAL  # scripted group (container) (typed FeaturePython)
  Dunit = g/cm3
  Dvalue = 0.92
  Group = -> [H_element093,C_element101]
  conduct = 2
  density = 1
  expand = 3
  formula = G4_RUBBER_NATURAL
  name = G4_RUBBER_NATURAL
  specific = 4
FEATURE [App::DocumentObjectGroupPython] H_element094  label="H_element : 0.145"  # scripted group (container) (typed FeaturePython)
  n = 0.05692
FEATURE [App::DocumentObjectGroupPython] C_element102  label="C_element : 0.543"  # scripted group (container) (typed FeaturePython)
  n = 0.542646
FEATURE [App::DocumentObjectGroupPython] Cl_element021  label="Cl_element : 0.400"  # scripted group (container) (typed FeaturePython)
  n = 0.400434
FEATURE [App::DocumentObjectGroupPython] G4_RUBBER_NEOPRENE  # scripted group (container) (typed FeaturePython)
  Dunit = g/cm3
  Dvalue = 1.23
  Group = -> [H_element094,C_element102,Cl_element021]
  conduct = 2
  density = 1
  expand = 3
  formula = G4_RUBBER_NEOPRENE
  name = G4_RUBBER_NEOPRENE
  specific = 4
FEATURE [App::DocumentObjectGroupPython] Si_element006  label="Si_element : 1"  # scripted group (container) (typed FeaturePython)
  n = 1
  ref = Si_element
FEATURE [App::DocumentObjectGroupPython] O_element087  label="O_element : 048"  # scripted group (container) (typed FeaturePython)
  n = 2
  ref = O_element
FEATURE [App::DocumentObjectGroupPython] G4_SILICON_DIOXIDE  # scripted group (container) (typed FeaturePython)
  Dunit = g/cm3
  Dvalue = 2.32
  Group = -> [Si_element006,O_element087]
  conduct = 2
  density = 1
  expand = 3
  formula = G4_SILICON_DIOXIDE
  name = G4_SILICON_DIOXIDE
  specific = 4
FEATURE [App::DocumentObjectGroupPython] Ag_element002  label="Ag_element : 1"  # scripted group (container) (typed FeaturePython)
  n = 1
  ref = Ag_element
FEATURE [App::DocumentObjectGroupPython] Br_element005  label="Br_element : 003"  # scripted group (container) (typed FeaturePython)
  n = 1
  ref = Br_element
FEATURE [App::DocumentObjectGroupPython] G4_SILVER_BROMIDE  # scripted group (container) (typed FeaturePython)
  Dunit = g/cm3
  Dvalue = 6.473
  Group = -> [Ag_element002,Br_element005]
  conduct = 2
  density = 1
  expand = 3
  formula = G4_SILVER_BROMIDE
  name = G4_SILVER_BROMIDE
  specific = 4
FEATURE [App::DocumentObjectGroupPython] Ag_element003  label="Ag_element : 002"  # scripted group (container) (typed FeaturePython)
  n = 1
  ref = Ag_element
FEATURE [App::DocumentObjectGroupPython] Cl_element022  label="Cl_element : 011"  # scripted group (container) (typed FeaturePython)
  n = 1
  ref = Cl_element
FEATURE [App::DocumentObjectGroupPython] G4_SILVER_CHLORIDE  # scripted group (container) (typed FeaturePython)
  Dunit = g/cm3
  Dvalue = 5.56
  Group = -> [Ag_element003,Cl_element022]
  conduct = 2
  density = 1
  expand = 3
  formula = G4_SILVER_CHLORIDE
  name = G4_SILVER_CHLORIDE
  specific = 4
FEATURE [App::DocumentObjectGroupPython] Br_element006  label="Br_element : 0.423"  # scripted group (container) (typed FeaturePython)
  n = 0.422895
FEATURE [App::DocumentObjectGroupPython] Ag_element004  label="Ag_element : 0.574"  # scripted group (container) (typed FeaturePython)
  n = 0.573748
FEATURE [App::DocumentObjectGroupPython] I_element007  label="I_element : 0.649"  # scripted group (container) (typed FeaturePython)
  n = 0.003357
FEATURE [App::DocumentObjectGroupPython] G4_SILVER_HALIDES  # scripted group (container) (typed FeaturePython)
  Dunit = g/cm3
  Dvalue = 6.47
  Group = -> [Br_element006,Ag_element004,I_element007]
  conduct = 2
  density = 1
  expand = 3
  formula = G4_SILVER_HALIDES
  name = G4_SILVER_HALIDES
  specific = 4
FEATURE [App::DocumentObjectGroupPython] Ag_element005  label="Ag_element : 003"  # scripted group (container) (typed FeaturePython)
  n = 1
  ref = Ag_element
FEATURE [App::DocumentObjectGroupPython] I_element008  label="I_element : 004"  # scripted group (container) (typed FeaturePython)
  n = 1
  ref = I_element
FEATURE [App::DocumentObjectGroupPython] G4_SILVER_IODIDE  # scripted group (container) (typed FeaturePython)
  Dunit = g/cm3
  Dvalue = 6.01
  Group = -> [Ag_element005,I_element008]
  conduct = 2
  density = 1
  expand = 3
  formula = G4_SILVER_IODIDE
  name = G4_SILVER_IODIDE
  specific = 4
FEATURE [App::DocumentObjectGroupPython] H_element095  label="H_element : 0.100"  # scripted group (container) (typed FeaturePython)
  n = 0.1
FEATURE [App::DocumentObjectGroupPython] C_element103  label="C_element : 0.204"  # scripted group (container) (typed FeaturePython)
  n = 0.204
FEATURE [App::DocumentObjectGroupPython] N_element039  label="N_element : 0.759"  # scripted group (container) (typed FeaturePython)
  n = 0.042
FEATURE [App::DocumentObjectGroupPython] O_element088  label="O_element : 0.645"  # scripted group (container) (typed FeaturePython)
  n = 0.645
FEATURE [App::DocumentObjectGroupPython] Na_element013  label="Na_element : 0.100"  # scripted group (container) (typed FeaturePython)
  n = 0.002
FEATURE [App::DocumentObjectGroupPython] P_element009  label="P_element : 0.107"  # scripted group (container) (typed FeaturePython)
  n = 0.001
FEATURE [App::DocumentObjectGroupPython] S_element020  label="S_element : 0.021"  # scripted group (container) (typed FeaturePython)
  n = 0.002
FEATURE [App::DocumentObjectGroupPython] Cl_element023  label="Cl_element : 0.590"  # scripted group (container) (typed FeaturePython)
  n = 0.003
FEATURE [App::DocumentObjectGroupPython] K_element010  label="K_element : 0.001"  # scripted group (container) (typed FeaturePython)
  n = 0.001
FEATURE [App::DocumentObjectGroupPython] G4_SKIN_ICRP  # scripted group (container) (typed FeaturePython)
  Dunit = g/cm3
  Dvalue = 1.09
  Group = -> [H_element095,C_element103,N_element039,O_element088,Na_element013,P_element009,S_element020,Cl_element023,K_element010]
  conduct = 2
  density = 1
  expand = 3
  formula = G4_SKIN_ICRP
  name = G4_SKIN_ICRP
  specific = 4
FEATURE [App::DocumentObjectGroupPython] Na_element014  label="Na_element : 2"  # scripted group (container) (typed FeaturePython)
  n = 2
  ref = Na_element
FEATURE [App::DocumentObjectGroupPython] C_element104  label="C_element : 058"  # scripted group (container) (typed FeaturePython)
  n = 1
  ref = C_element
FEATURE [App::DocumentObjectGroupPython] O_element089  label="O_element : 049"  # scripted group (container) (typed FeaturePython)
  n = 3
  ref = O_element
FEATURE [App::DocumentObjectGroupPython] G4_SODIUM_CARBONATE  # scripted group (container) (typed FeaturePython)
  Dunit = g/cm3
  Dvalue = 2.532
  Group = -> [Na_element014,C_element104,O_element089]
  conduct = 2
  density = 1
  expand = 3
  formula = G4_SODIUM_CARBONATE
  name = G4_SODIUM_CARBONATE
  specific = 4
FEATURE [App::DocumentObjectGroupPython] Na_element015  label="Na_element : 1"  # scripted group (container) (typed FeaturePython)
  n = 1
  ref = Na_element
FEATURE [App::DocumentObjectGroupPython] I_element009  label="I_element : 005"  # scripted group (container) (typed FeaturePython)
  n = 1
  ref = I_element
FEATURE [App::DocumentObjectGroupPython] G4_SODIUM_IODIDE  # scripted group (container) (typed FeaturePython)
  Dunit = g/cm3
  Dvalue = 3.667
  Group = -> [Na_element015,I_element009]
  conduct = 2
  density = 1
  expand = 3
  formula = G4_SODIUM_IODIDE
  name = G4_SODIUM_IODIDE
  specific = 4
FEATURE [App::DocumentObjectGroupPython] Na_element016  label="Na_element : 003"  # scripted group (container) (typed FeaturePython)
  n = 2
  ref = Na_element
FEATURE [App::DocumentObjectGroupPython] O_element090  label="O_element : 050"  # scripted group (container) (typed FeaturePython)
  n = 1
  ref = O_element
FEATURE [App::DocumentObjectGroupPython] G4_SODIUM_MONOXIDE  # scripted group (container) (typed FeaturePython)
  Dunit = g/cm3
  Dvalue = 2.27
  Group = -> [Na_element016,O_element090]
  conduct = 2
  density = 1
  expand = 3
  formula = G4_SODIUM_MONOXIDE
  name = G4_SODIUM_MONOXIDE
  specific = 4
FEATURE [App::DocumentObjectGroupPython] Na_element017  label="Na_element : 004"  # scripted group (container) (typed FeaturePython)
  n = 1
  ref = Na_element
FEATURE [App::DocumentObjectGroupPython] N_element040  label="N_element : 018"  # scripted group (container) (typed FeaturePython)
  n = 1
  ref = N_element
FEATURE [App::DocumentObjectGroupPython] O_element091  label="O_element : 051"  # scripted group (container) (typed FeaturePython)
  n = 3
  ref = O_element
FEATURE [App::DocumentObjectGroupPython] G4_SODIUM_NITRATE  # scripted group (container) (typed FeaturePython)
  Dunit = g/cm3
  Dvalue = 2.261
  Group = -> [Na_element017,N_element040,O_element091]
  conduct = 2
  density = 1
  expand = 3
  formula = G4_SODIUM_NITRATE
  name = G4_SODIUM_NITRATE
  specific = 4
FEATURE [App::DocumentObjectGroupPython] C_element105  label="C_element : 059"  # scripted group (container) (typed FeaturePython)
  n = 14
  ref = C_element
FEATURE [App::DocumentObjectGroupPython] H_element096  label="H_element : 053"  # scripted group (container) (typed FeaturePython)
  n = 12
  ref = H_element
FEATURE [App::DocumentObjectGroupPython] G4_STILBENE  # scripted group (container) (typed FeaturePython)
  Dunit = g/cm3
  Dvalue = 0.9707
  Group = -> [C_element105,H_element096]
  conduct = 2
  density = 1
  expand = 3
  formula = G4_STILBENE
  name = G4_STILBENE
  specific = 4
FEATURE [App::DocumentObjectGroupPython] C_element106  label="C_element : 12"  # scripted group (container) (typed FeaturePython)
  n = 12
  ref = C_element
FEATURE [App::DocumentObjectGroupPython] H_element097  label="H_element : 22"  # scripted group (container) (typed FeaturePython)
  n = 22
  ref = H_element
FEATURE [App::DocumentObjectGroupPython] O_element092  label="O_element : 11"  # scripted group (container) (typed FeaturePython)
  n = 11
  ref = O_element
FEATURE [App::DocumentObjectGroupPython] G4_SUCROSE  # scripted group (container) (typed FeaturePython)
  Dunit = g/cm3
  Dvalue = 1.5805
  Group = -> [C_element106,H_element097,O_element092]
  conduct = 2
  density = 1
  expand = 3
  formula = G4_SUCROSE
  name = G4_SUCROSE
  specific = 4
FEATURE [App::DocumentObjectGroupPython] C_element107  label="C_element : 18"  # scripted group (container) (typed FeaturePython)
  n = 18
  ref = C_element
FEATURE [App::DocumentObjectGroupPython] H_element098  label="H_element : 054"  # scripted group (container) (typed FeaturePython)
  n = 14
  ref = H_element
FEATURE [App::DocumentObjectGroupPython] G4_TERPHENYL  # scripted group (container) (typed FeaturePython)
  Dunit = g/cm3
  Dvalue = 1.24
  Group = -> [C_element107,H_element098]
  conduct = 2
  density = 1
  expand = 3
  formula = G4_TERPHENYL
  name = G4_TERPHENYL
  specific = 4
FEATURE [App::DocumentObjectGroupPython] H_element099  label="H_element : 0.146"  # scripted group (container) (typed FeaturePython)
  n = 0.106
FEATURE [App::DocumentObjectGroupPython] C_element108  label="C_element : 0.883"  # scripted group (container) (typed FeaturePython)
  n = 0.099
FEATURE [App::DocumentObjectGroupPython] N_element041  label="N_element : 0.020"  # scripted group (container) (typed FeaturePython)
  n = 0.02
FEATURE [App::DocumentObjectGroupPython] O_element093  label="O_element : 0.766"  # scripted group (container) (typed FeaturePython)
  n = 0.766
FEATURE [App::DocumentObjectGroupPython] Na_element018  label="Na_element : 0.101"  # scripted group (container) (typed FeaturePython)
  n = 0.002
FEATURE [App::DocumentObjectGroupPython] P_element010  label="P_element : 0.108"  # scripted group (container) (typed FeaturePython)
  n = 0.001
FEATURE [App::DocumentObjectGroupPython] S_element021  label="S_element : 0.022"  # scripted group (container) (typed FeaturePython)
  n = 0.002
FEATURE [App::DocumentObjectGroupPython] Cl_element024  label="Cl_element : 0.002"  # scripted group (container) (typed FeaturePython)
  n = 0.002
FEATURE [App::DocumentObjectGroupPython] K_element011  label="K_element : 0.017"  # scripted group (container) (typed FeaturePython)
  n = 0.002
FEATURE [App::DocumentObjectGroupPython] G4_TESTIS_ICRP  # scripted group (container) (typed FeaturePython)
  Dunit = g/cm3
  Dvalue = 1.04
  Group = -> [H_element099,C_element108,N_element041,O_element093,Na_element018,P_element010,S_element021,Cl_element024,K_element011]
  conduct = 2
  density = 1
  expand = 3
  formula = G4_TESTIS_ICRP
  name = G4_TESTIS_ICRP
  specific = 4
FEATURE [App::DocumentObjectGroupPython] C_element109  label="C_element : 060"  # scripted group (container) (typed FeaturePython)
  n = 2
  ref = C_element
FEATURE [App::DocumentObjectGroupPython] Cl_element025  label="Cl_element : 012"  # scripted group (container) (typed FeaturePython)
  n = 4
  ref = Cl_element
FEATURE [App::DocumentObjectGroupPython] G4_TETRACHLOROETHYLENE  # scripted group (container) (typed FeaturePython)
  Dunit = g/cm3
  Dvalue = 1.625
  Group = -> [C_element109,Cl_element025]
  conduct = 2
  density = 1
  expand = 3
  formula = G4_TETRACHLOROETHYLENE
  name = G4_TETRACHLOROETHYLENE
  specific = 4
FEATURE [App::DocumentObjectGroupPython] Tl_element001  label="Tl_element : 1"  # scripted group (container) (typed FeaturePython)
  n = 1
  ref = Tl_element
FEATURE [App::DocumentObjectGroupPython] Cl_element026  label="Cl_element : 013"  # scripted group (container) (typed FeaturePython)
  n = 1
  ref = Cl_element
FEATURE [App::DocumentObjectGroupPython] G4_THALLIUM_CHLORIDE  # scripted group (container) (typed FeaturePython)
  Dunit = g/cm3
  Dvalue = 7.004
  Group = -> [Tl_element001,Cl_element026]
  conduct = 2
  density = 1
  expand = 3
  formula = G4_THALLIUM_CHLORIDE
  name = G4_THALLIUM_CHLORIDE
  specific = 4
FEATURE [App::DocumentObjectGroupPython] H_element100  label="H_element : 0.147"  # scripted group (container) (typed FeaturePython)
  n = 0.105
FEATURE [App::DocumentObjectGroupPython] C_element110  label="C_element : 0.256"  # scripted group (container) (typed FeaturePython)
  n = 0.256
FEATURE [App::DocumentObjectGroupPython] N_element042  label="N_element : 0.760"  # scripted group (container) (typed FeaturePython)
  n = 0.027
FEATURE [App::DocumentObjectGroupPython] O_element094  label="O_element : 0.602"  # scripted group (container) (typed FeaturePython)
  n = 0.602
FEATURE [App::DocumentObjectGroupPython] Na_element019  label="Na_element : 0.102"  # scripted group (container) (typed FeaturePython)
  n = 0.001
FEATURE [App::DocumentObjectGroupPython] P_element011  label="P_element : 0.109"  # scripted group (container) (typed FeaturePython)
  n = 0.002
FEATURE [App::DocumentObjectGroupPython] S_element022  label="S_element : 0.023"  # scripted group (container) (typed FeaturePython)
  n = 0.003
FEATURE [App::DocumentObjectGroupPython] Cl_element027  label="Cl_element : 0.591"  # scripted group (container) (typed FeaturePython)
  n = 0.002
FEATURE [App::DocumentObjectGroupPython] K_element012  label="K_element : 0.018"  # scripted group (container) (typed FeaturePython)
  n = 0.002
FEATURE [App::DocumentObjectGroupPython] G4_TISSUE_SOFT_ICRP  # scripted group (container) (typed FeaturePython)
  Dunit = g/cm3
  Dvalue = 1.03
  Group = -> [H_element100,C_element110,N_element042,O_element094,Na_element019,P_element011,S_element022,Cl_element027,K_element012]
  conduct = 2
  density = 1
  expand = 3
  formula = G4_TISSUE_SOFT_ICRP
  name = G4_TISSUE_SOFT_ICRP
  specific = 4
FEATURE [App::DocumentObjectGroupPython] H_element101  label="H_element : 0.148"  # scripted group (container) (typed FeaturePython)
  n = 0.101
FEATURE [App::DocumentObjectGroupPython] C_element111  label="C_element : 0.111"  # scripted group (container) (typed FeaturePython)
  n = 0.111
FEATURE [App::DocumentObjectGroupPython] N_element043  label="N_element : 0.026"  # scripted group (container) (typed FeaturePython)
  n = 0.026
FEATURE [App::DocumentObjectGroupPython] O_element095  label="O_element : 0.762"  # scripted group (container) (typed FeaturePython)
  n = 0.762
FEATURE [App::DocumentObjectGroupPython] G4_TISSUE_SOFT_ICRU_4  label="G4_TISSUE_SOFT_ICRU-4"  # scripted group (container) (typed FeaturePython)
  Dunit = g/cm3
  Dvalue = 1
  Group = -> [H_element101,C_element111,N_element043,O_element095]
  conduct = 2
  density = 1
  expand = 3
  formula = G4_TISSUE_SOFT_ICRU-4
  name = G4_TISSUE_SOFT_ICRU-4
  specific = 4
FEATURE [App::DocumentObjectGroupPython] H_element102  label="H_element : 0.149"  # scripted group (container) (typed FeaturePython)
  n = 0.101869
FEATURE [App::DocumentObjectGroupPython] C_element112  label="C_element : 0.456"  # scripted group (container) (typed FeaturePython)
  n = 0.456179
FEATURE [App::DocumentObjectGroupPython] N_element044  label="N_element : 0.761"  # scripted group (container) (typed FeaturePython)
  n = 0.035172
FEATURE [App::DocumentObjectGroupPython] O_element096  label="O_element : 0.407"  # scripted group (container) (typed FeaturePython)
  n = 0.40678
FEATURE [App::DocumentObjectGroupPython] G4_TISSUE_METHANE  label="G4_TISSUE-METHANE"  # scripted group (container) (typed FeaturePython)
  Dunit = g/cm3
  Dvalue = 0.00106409
  Group = -> [H_element102,C_element112,N_element044,O_element096]
  conduct = 2
  density = 1
  expand = 3
  formula = G4_TISSUE-METHANE
  name = G4_TISSUE-METHANE
  specific = 4
FEATURE [App::DocumentObjectGroupPython] H_element103  label="H_element : 0.103"  # scripted group (container) (typed FeaturePython)
  n = 0.102672
FEATURE [App::DocumentObjectGroupPython] C_element113  label="C_element : 0.569"  # scripted group (container) (typed FeaturePython)
  n = 0.56894
FEATURE [App::DocumentObjectGroupPython] N_element045  label="N_element : 0.762"  # scripted group (container) (typed FeaturePython)
  n = 0.035022
FEATURE [App::DocumentObjectGroupPython] O_element097  label="O_element : 0.293"  # scripted group (container) (typed FeaturePython)
  n = 0.293366
FEATURE [App::DocumentObjectGroupPython] G4_TISSUE_PROPANE  label="G4_TISSUE-PROPANE"  # scripted group (container) (typed FeaturePython)
  Dunit = g/cm3
  Dvalue = 0.00182628
  Group = -> [H_element103,C_element113,N_element045,O_element097]
  conduct = 2
  density = 1
  expand = 3
  formula = G4_TISSUE-PROPANE
  name = G4_TISSUE-PROPANE
  specific = 4
FEATURE [App::DocumentObjectGroupPython] Ti_element003  label="Ti_element : 1"  # scripted group (container) (typed FeaturePython)
  n = 1
  ref = Ti_element
FEATURE [App::DocumentObjectGroupPython] O_element098  label="O_element : 052"  # scripted group (container) (typed FeaturePython)
  n = 2
  ref = O_element
FEATURE [App::DocumentObjectGroupPython] G4_TITANIUM_DIOXIDE  # scripted group (container) (typed FeaturePython)
  Dunit = g/cm3
  Dvalue = 4.26
  Group = -> [Ti_element003,O_element098]
  conduct = 2
  density = 1
  expand = 3
  formula = G4_TITANIUM_DIOXIDE
  name = G4_TITANIUM_DIOXIDE
  specific = 4
FEATURE [App::DocumentObjectGroupPython] C_element114  label="C_element : 061"  # scripted group (container) (typed FeaturePython)
  n = 7
  ref = C_element
FEATURE [App::DocumentObjectGroupPython] H_element104  label="H_element : 055"  # scripted group (container) (typed FeaturePython)
  n = 8
  ref = H_element
FEATURE [App::DocumentObjectGroupPython] G4_TOLUENE  # scripted group (container) (typed FeaturePython)
  Dunit = g/cm3
  Dvalue = 0.8669
  Group = -> [C_element114,H_element104]
  conduct = 2
  density = 1
  expand = 3
  formula = G4_TOLUENE
  name = G4_TOLUENE
  specific = 4
FEATURE [App::DocumentObjectGroupPython] C_element115  label="C_element : 062"  # scripted group (container) (typed FeaturePython)
  n = 2
  ref = C_element
FEATURE [App::DocumentObjectGroupPython] H_element105  label="H_element : 056"  # scripted group (container) (typed FeaturePython)
  n = 1
  ref = H_element
FEATURE [App::DocumentObjectGroupPython] Cl_element028  label="Cl_element : 014"  # scripted group (container) (typed FeaturePython)
  n = 3
  ref = Cl_element
FEATURE [App::DocumentObjectGroupPython] G4_TRICHLOROETHYLENE  # scripted group (container) (typed FeaturePython)
  Dunit = g/cm3
  Dvalue = 1.46
  Group = -> [C_element115,H_element105,Cl_element028]
  conduct = 2
  density = 1
  expand = 3
  formula = G4_TRICHLOROETHYLENE
  name = G4_TRICHLOROETHYLENE
  specific = 4
FEATURE [App::DocumentObjectGroupPython] C_element116  label="C_element : 063"  # scripted group (container) (typed FeaturePython)
  n = 6
  ref = C_element
FEATURE [App::DocumentObjectGroupPython] H_element106  label="H_element : 15"  # scripted group (container) (typed FeaturePython)
  n = 15
  ref = H_element
FEATURE [App::DocumentObjectGroupPython] O_element099  label="O_element : 053"  # scripted group (container) (typed FeaturePython)
  n = 4
  ref = O_element
FEATURE [App::DocumentObjectGroupPython] P_element012  label="P_element : 1"  # scripted group (container) (typed FeaturePython)
  n = 1
  ref = P_element
FEATURE [App::DocumentObjectGroupPython] G4_TRIETHYL_PHOSPHATE  # scripted group (container) (typed FeaturePython)
  Dunit = g/cm3
  Dvalue = 1.07
  Group = -> [C_element116,H_element106,O_element099,P_element012]
  conduct = 2
  density = 1
  expand = 3
  formula = G4_TRIETHYL_PHOSPHATE
  name = G4_TRIETHYL_PHOSPHATE
  specific = 4
FEATURE [App::DocumentObjectGroupPython] W_element003  label="W_element : 003"  # scripted group (container) (typed FeaturePython)
  n = 1
  ref = W_element
FEATURE [App::DocumentObjectGroupPython] F_element017  label="F_element : 6"  # scripted group (container) (typed FeaturePython)
  n = 6
  ref = F_element
FEATURE [App::DocumentObjectGroupPython] G4_TUNGSTEN_HEXAFLUORIDE  # scripted group (container) (typed FeaturePython)
  Dunit = g/cm3
  Dvalue = 2.4
  Group = -> [W_element003,F_element017]
  conduct = 2
  density = 1
  expand = 3
  formula = G4_TUNGSTEN_HEXAFLUORIDE
  name = G4_TUNGSTEN_HEXAFLUORIDE
  specific = 4
FEATURE [App::DocumentObjectGroupPython] U_element001  label="U_element : 1"  # scripted group (container) (typed FeaturePython)
  n = 1
  ref = U_element
FEATURE [App::DocumentObjectGroupPython] C_element117  label="C_element : 064"  # scripted group (container) (typed FeaturePython)
  n = 2
  ref = C_element
FEATURE [App::DocumentObjectGroupPython] G4_URANIUM_DICARBIDE  # scripted group (container) (typed FeaturePython)
  Dunit = g/cm3
  Dvalue = 11.28
  Group = -> [U_element001,C_element117]
  conduct = 2
  density = 1
  expand = 3
  formula = G4_URANIUM_DICARBIDE
  name = G4_URANIUM_DICARBIDE
  specific = 4
FEATURE [App::DocumentObjectGroupPython] U_element002  label="U_element : 002"  # scripted group (container) (typed FeaturePython)
  n = 1
  ref = U_element
FEATURE [App::DocumentObjectGroupPython] C_element118  label="C_element : 065"  # scripted group (container) (typed FeaturePython)
  n = 1
  ref = C_element
FEATURE [App::DocumentObjectGroupPython] G4_URANIUM_MONOCARBIDE  # scripted group (container) (typed FeaturePython)
  Dunit = g/cm3
  Dvalue = 13.63
  Group = -> [U_element002,C_element118]
  conduct = 2
  density = 1
  expand = 3
  formula = G4_URANIUM_MONOCARBIDE
  name = G4_URANIUM_MONOCARBIDE
  specific = 4
FEATURE [App::DocumentObjectGroupPython] U_element003  label="U_element : 003"  # scripted group (container) (typed FeaturePython)
  n = 1
  ref = U_element
FEATURE [App::DocumentObjectGroupPython] O_element100  label="O_element : 054"  # scripted group (container) (typed FeaturePython)
  n = 2
  ref = O_element
FEATURE [App::DocumentObjectGroupPython] G4_URANIUM_OXIDE  # scripted group (container) (typed FeaturePython)
  Dunit = g/cm3
  Dvalue = 10.96
  Group = -> [U_element003,O_element100]
  conduct = 2
  density = 1
  expand = 3
  formula = G4_URANIUM_OXIDE
  name = G4_URANIUM_OXIDE
  specific = 4
FEATURE [App::DocumentObjectGroupPython] C_element119  label="C_element : 066"  # scripted group (container) (typed FeaturePython)
  n = 1
  ref = C_element
FEATURE [App::DocumentObjectGroupPython] H_element107  label="H_element : 057"  # scripted group (container) (typed FeaturePython)
  n = 4
  ref = H_element
FEATURE [App::DocumentObjectGroupPython] N_element046  label="N_element : 019"  # scripted group (container) (typed FeaturePython)
  n = 2
  ref = N_element
FEATURE [App::DocumentObjectGroupPython] O_element101  label="O_element : 055"  # scripted group (container) (typed FeaturePython)
  n = 1
  ref = O_element
FEATURE [App::DocumentObjectGroupPython] G4_UREA  # scripted group (container) (typed FeaturePython)
  Dunit = g/cm3
  Dvalue = 1.323
  Group = -> [C_element119,H_element107,N_element046,O_element101]
  conduct = 2
  density = 1
  expand = 3
  formula = G4_UREA
  name = G4_UREA
  specific = 4
FEATURE [App::DocumentObjectGroupPython] C_element120  label="C_element : 067"  # scripted group (container) (typed FeaturePython)
  n = 5
  ref = C_element
FEATURE [App::DocumentObjectGroupPython] H_element108  label="H_element : 058"  # scripted group (container) (typed FeaturePython)
  n = 11
  ref = H_element
FEATURE [App::DocumentObjectGroupPython] N_element047  label="N_element : 020"  # scripted group (container) (typed FeaturePython)
  n = 1
  ref = N_element
FEATURE [App::DocumentObjectGroupPython] O_element102  label="O_element : 056"  # scripted group (container) (typed FeaturePython)
  n = 2
  ref = O_element
FEATURE [App::DocumentObjectGroupPython] G4_VALINE  # scripted group (container) (typed FeaturePython)
  Dunit = g/cm3
  Dvalue = 1.23
  Group = -> [C_element120,H_element108,N_element047,O_element102]
  conduct = 2
  density = 1
  expand = 3
  formula = G4_VALINE
  name = G4_VALINE
  specific = 4
FEATURE [App::DocumentObjectGroupPython] H_element109  label="H_element : 0.009"  # scripted group (container) (typed FeaturePython)
  n = 0.009417
FEATURE [App::DocumentObjectGroupPython] C_element121  label="C_element : 0.281"  # scripted group (container) (typed FeaturePython)
  n = 0.280555
FEATURE [App::DocumentObjectGroupPython] F_element018  label="F_element : 0.710"  # scripted group (container) (typed FeaturePython)
  n = 0.710028
FEATURE [App::DocumentObjectGroupPython] G4_VITON  # scripted group (container) (typed FeaturePython)
  Dunit = g/cm3
  Dvalue = 1.8
  Group = -> [H_element109,C_element121,F_element018]
  conduct = 2
  density = 1
  expand = 3
  formula = G4_VITON
  name = G4_VITON
  specific = 4
FEATURE [App::DocumentObjectGroupPython] H_element110  label="H_element : 059"  # scripted group (container) (typed FeaturePython)
  n = 2
  ref = H_element
FEATURE [App::DocumentObjectGroupPython] O_element103  label="O_element : 057"  # scripted group (container) (typed FeaturePython)
  n = 1
  ref = O_element
FEATURE [App::DocumentObjectGroupPython] G4_WATER  # scripted group (container) (typed FeaturePython)
  Dunit = g/cm3
  Dvalue = 1
  Group = -> [H_element110,O_element103]
  conduct = 2
  density = 1
  expand = 3
  formula = G4_WATER
  name = G4_WATER
  specific = 4
FEATURE [App::DocumentObjectGroupPython] H_element111  label="H_element : 060"  # scripted group (container) (typed FeaturePython)
  n = 2
  ref = H_element
FEATURE [App::DocumentObjectGroupPython] O_element104  label="O_element : 058"  # scripted group (container) (typed FeaturePython)
  n = 1
  ref = O_element
FEATURE [App::DocumentObjectGroupPython] G4_WATER_VAPOR  # scripted group (container) (typed FeaturePython)
  Dunit = g/cm3
  Dvalue = 0.000756182
  Group = -> [H_element111,O_element104]
  conduct = 2
  density = 1
  expand = 3
  formula = G4_WATER_VAPOR
  name = G4_WATER_VAPOR
  specific = 4
FEATURE [App::DocumentObjectGroupPython] C_element122  label="C_element : 068"  # scripted group (container) (typed FeaturePython)
  n = 8
  ref = C_element
FEATURE [App::DocumentObjectGroupPython] H_element112  label="H_element : 061"  # scripted group (container) (typed FeaturePython)
  n = 10
  ref = H_element
FEATURE [App::DocumentObjectGroupPython] G4_XYLENE  # scripted group (container) (typed FeaturePython)
  Dunit = g/cm3
  Dvalue = 0.87
  Group = -> [C_element122,H_element112]
  conduct = 2
  density = 1
  expand = 3
  formula = G4_XYLENE
  name = G4_XYLENE
  specific = 4
FEATURE [App::DocumentObjectGroupPython] C_element123  label="C_element : 069"  # scripted group (container) (typed FeaturePython)
  n = 1
  ref = C_element
FEATURE [App::DocumentObjectGroupPython] G4_GRAPHITE  # scripted group (container) (typed FeaturePython)
  Dunit = g/cm3
  Dvalue = 2.21
  Group = -> [C_element123]
  conduct = 2
  density = 1
  expand = 3
  formula = G4_GRAPHITE
  name = G4_GRAPHITE
  specific = 4
FEATURE [App::DocumentObjectGroupPython] NIST  # scripted group (container) (typed FeaturePython)
  Group = -> [G4_A_150_TISSUE,G4_ACETONE,G4_ACETYLENE,G4_ADENINE,G4_ADIPOSE_TISSUE_ICRP,G4_AIR,G4_ALANINE,G4_ALUMINUM_OXIDE,G4_AMBER,G4_AMMONIA,G4_ANILINE,G4_ANTHRACENE,G4_B_100_BONE,G4_BAKELITE,G4_BARIUM_FLUORIDE,G4_BARIUM_SULFATE,G4_BENZENE,G4_BERYLLIUM_OXIDE,G4_BGO,G4_BLOOD_ICRP,G4_BONE_COMPACT_ICRU,G4_BONE_CORTICAL_ICRP,G4_BORON_CARBIDE,G4_BORON_OXIDE,G4_BRAIN_ICRP,G4_BUTANE,G4_N_BUTYL_ALCOHOL,G4_C_552,+152 more]
FEATURE [App::DocumentObjectGroupPython] H_element113  label="H_element : 062"  # scripted group (container) (typed FeaturePython)
  n = 1
  ref = H_element
FEATURE [App::DocumentObjectGroupPython] G4_H  # scripted group (container) (typed FeaturePython)
  Dunit = g/cm3
  Dvalue = 8.3748e-05
  Group = -> [H_element113]
  conduct = 2
  density = 1
  expand = 3
  formula = H
  name = G4_H
  specific = 4
FEATURE [App::DocumentObjectGroupPython] He_element001  label="He_element : 1"  # scripted group (container) (typed FeaturePython)
  n = 1
  ref = He_element
FEATURE [App::DocumentObjectGroupPython] G4_He  # scripted group (container) (typed FeaturePython)
  Dunit = g/cm3
  Dvalue = 0.000166322
  Group = -> [He_element001]
  conduct = 2
  density = 1
  expand = 3
  formula = He
  name = G4_He
  specific = 4
FEATURE [App::DocumentObjectGroupPython] Li_element008  label="Li_element : 008"  # scripted group (container) (typed FeaturePython)
  n = 1
  ref = Li_element
FEATURE [App::DocumentObjectGroupPython] G4_Li  # scripted group (container) (typed FeaturePython)
  Dunit = g/cm3
  Dvalue = 0.534
  Group = -> [Li_element008]
  conduct = 2
  density = 1
  expand = 3
  formula = Li
  name = G4_Li
  specific = 4
FEATURE [App::DocumentObjectGroupPython] Be_element002  label="Be_element : 002"  # scripted group (container) (typed FeaturePython)
  n = 1
  ref = Be_element
FEATURE [App::DocumentObjectGroupPython] G4_Be  # scripted group (container) (typed FeaturePython)
  Dunit = g/cm3
  Dvalue = 1.848
  Group = -> [Be_element002]
  conduct = 2
  density = 1
  expand = 3
  formula = Be
  name = G4_Be
  specific = 4
FEATURE [App::DocumentObjectGroupPython] B_element007  label="B_element : 007"  # scripted group (container) (typed FeaturePython)
  n = 1
  ref = B_element
FEATURE [App::DocumentObjectGroupPython] G4_B  # scripted group (container) (typed FeaturePython)
  Dunit = g/cm3
  Dvalue = 2.37
  Group = -> [B_element007]
  conduct = 2
  density = 1
  expand = 3
  formula = B
  name = G4_B
  specific = 4
FEATURE [App::DocumentObjectGroupPython] C_element124  label="C_element : 070"  # scripted group (container) (typed FeaturePython)
  n = 1
  ref = C_element
FEATURE [App::DocumentObjectGroupPython] G4_C  # scripted group (container) (typed FeaturePython)
  Dunit = g/cm3
  Dvalue = 2
  Group = -> [C_element124]
  conduct = 2
  density = 1
  expand = 3
  formula = C
  name = G4_C
  specific = 4
FEATURE [App::DocumentObjectGroupPython] N_element048  label="N_element : 021"  # scripted group (container) (typed FeaturePython)
  n = 1
  ref = N_element
FEATURE [App::DocumentObjectGroupPython] G4_N  # scripted group (container) (typed FeaturePython)
  Dunit = g/cm3
  Dvalue = 0.0011652
  Group = -> [N_element048]
  conduct = 2
  density = 1
  expand = 3
  formula = N
  name = G4_N
  specific = 4
FEATURE [App::DocumentObjectGroupPython] O_element105  label="O_element : 059"  # scripted group (container) (typed FeaturePython)
  n = 1
  ref = O_element
FEATURE [App::DocumentObjectGroupPython] G4_O  # scripted group (container) (typed FeaturePython)
  Dunit = g/cm3
  Dvalue = 0.00133151
  Group = -> [O_element105]
  conduct = 2
  density = 1
  expand = 3
  formula = O
  name = G4_O
  specific = 4
FEATURE [App::DocumentObjectGroupPython] F_element019  label="F_element : 008"  # scripted group (container) (typed FeaturePython)
  n = 1
  ref = F_element
FEATURE [App::DocumentObjectGroupPython] G4_F  # scripted group (container) (typed FeaturePython)
  Dunit = g/cm3
  Dvalue = 0.00158029
  Group = -> [F_element019]
  conduct = 2
  density = 1
  expand = 3
  formula = F
  name = G4_F
  specific = 4
FEATURE [App::DocumentObjectGroupPython] Ne_element001  label="Ne_element : 1"  # scripted group (container) (typed FeaturePython)
  n = 1
  ref = Ne_element
FEATURE [App::DocumentObjectGroupPython] G4_Ne  # scripted group (container) (typed FeaturePython)
  Dunit = g/cm3
  Dvalue = 0.000838505
  Group = -> [Ne_element001]
  conduct = 2
  density = 1
  expand = 3
  formula = Ne
  name = G4_Ne
  specific = 4
FEATURE [App::DocumentObjectGroupPython] Na_element020  label="Na_element : 005"  # scripted group (container) (typed FeaturePython)
  n = 1
  ref = Na_element
FEATURE [App::DocumentObjectGroupPython] G4_Na  # scripted group (container) (typed FeaturePython)
  Dunit = g/cm3
  Dvalue = 0.971
  Group = -> [Na_element020]
  conduct = 2
  density = 1
  expand = 3
  formula = Na
  name = G4_Na
  specific = 4
FEATURE [App::DocumentObjectGroupPython] Mg_element011  label="Mg_element : 005"  # scripted group (container) (typed FeaturePython)
  n = 1
  ref = Mg_element
FEATURE [App::DocumentObjectGroupPython] G4_Mg  # scripted group (container) (typed FeaturePython)
  Dunit = g/cm3
  Dvalue = 1.74
  Group = -> [Mg_element011]
  conduct = 2
  density = 1
  expand = 3
  formula = Mg
  name = G4_Mg
  specific = 4
FEATURE [App::DocumentObjectGroupPython] Al_element004  label="Al_element : 1"  # scripted group (container) (typed FeaturePython)
  n = 1
  ref = Al_element
FEATURE [App::DocumentObjectGroupPython] G4_Al  # scripted group (container) (typed FeaturePython)
  Dunit = g/cm3
  Dvalue = 2.699
  Group = -> [Al_element004]
  conduct = 2
  density = 1
  expand = 3
  formula = Al
  name = G4_Al
  specific = 4
FEATURE [App::DocumentObjectGroupPython] Si_element007  label="Si_element : 002"  # scripted group (container) (typed FeaturePython)
  n = 1
  ref = Si_element
FEATURE [App::DocumentObjectGroupPython] G4_Si  # scripted group (container) (typed FeaturePython)
  Dunit = g/cm3
  Dvalue = 2.33
  Group = -> [Si_element007]
  conduct = 2
  density = 1
  expand = 3
  formula = Si
  name = G4_Si
  specific = 4
FEATURE [App::DocumentObjectGroupPython] P_element013  label="P_element : 002"  # scripted group (container) (typed FeaturePython)
  n = 1
  ref = P_element
FEATURE [App::DocumentObjectGroupPython] G4_P  # scripted group (container) (typed FeaturePython)
  Dunit = g/cm3
  Dvalue = 2.2
  Group = -> [P_element013]
  conduct = 2
  density = 1
  expand = 3
  formula = P
  name = G4_P
  specific = 4
FEATURE [App::DocumentObjectGroupPython] S_element023  label="S_element : 007"  # scripted group (container) (typed FeaturePython)
  n = 1
  ref = S_element
FEATURE [App::DocumentObjectGroupPython] G4_S  # scripted group (container) (typed FeaturePython)
  Dunit = g/cm3
  Dvalue = 2
  Group = -> [S_element023]
  conduct = 2
  density = 1
  expand = 3
  formula = S
  name = G4_S
  specific = 4
FEATURE [App::DocumentObjectGroupPython] Cl_element029  label="Cl_element : 015"  # scripted group (container) (typed FeaturePython)
  n = 1
  ref = Cl_element
FEATURE [App::DocumentObjectGroupPython] G4_Cl  # scripted group (container) (typed FeaturePython)
  Dunit = g/cm3
  Dvalue = 0.00299473
  Group = -> [Cl_element029]
  conduct = 2
  density = 1
  expand = 3
  formula = Cl
  name = G4_Cl
  specific = 4
FEATURE [App::DocumentObjectGroupPython] Ar_element002  label="Ar_element : 1"  # scripted group (container) (typed FeaturePython)
  n = 1
  ref = Ar_element
FEATURE [App::DocumentObjectGroupPython] G4_Ar  # scripted group (container) (typed FeaturePython)
  Dunit = g/cm3
  Dvalue = 0.00166201
  Group = -> [Ar_element002]
  conduct = 2
  density = 1
  expand = 3
  formula = Ar
  name = G4_Ar
  specific = 4
FEATURE [App::DocumentObjectGroupPython] K_element013  label="K_element : 003"  # scripted group (container) (typed FeaturePython)
  n = 1
  ref = K_element
FEATURE [App::DocumentObjectGroupPython] G4_K  # scripted group (container) (typed FeaturePython)
  Dunit = g/cm3
  Dvalue = 0.862
  Group = -> [K_element013]
  conduct = 2
  density = 1
  expand = 3
  formula = K
  name = G4_K
  specific = 4
FEATURE [App::DocumentObjectGroupPython] Ca_element014  label="Ca_element : 007"  # scripted group (container) (typed FeaturePython)
  n = 1
  ref = Ca_element
FEATURE [App::DocumentObjectGroupPython] G4_Ca  # scripted group (container) (typed FeaturePython)
  Dunit = g/cm3
  Dvalue = 1.55
  Group = -> [Ca_element014]
  conduct = 2
  density = 1
  expand = 3
  formula = Ca
  name = G4_Ca
  specific = 4
FEATURE [App::DocumentObjectGroupPython] Sc_element001  label="Sc_element : 1"  # scripted group (container) (typed FeaturePython)
  n = 1
  ref = Sc_element
FEATURE [App::DocumentObjectGroupPython] G4_Sc  # scripted group (container) (typed FeaturePython)
  Dunit = g/cm3
  Dvalue = 2.989
  Group = -> [Sc_element001]
  conduct = 2
  density = 1
  expand = 3
  formula = Sc
  name = G4_Sc
  specific = 4
FEATURE [App::DocumentObjectGroupPython] Ti_element004  label="Ti_element : 002"  # scripted group (container) (typed FeaturePython)
  n = 1
  ref = Ti_element
FEATURE [App::DocumentObjectGroupPython] G4_Ti  # scripted group (container) (typed FeaturePython)
  Dunit = g/cm3
  Dvalue = 4.54
  Group = -> [Ti_element004]
  conduct = 2
  density = 1
  expand = 3
  formula = Ti
  name = G4_Ti
  specific = 4
FEATURE [App::DocumentObjectGroupPython] V_element001  label="V_element : 1"  # scripted group (container) (typed FeaturePython)
  n = 1
  ref = V_element
FEATURE [App::DocumentObjectGroupPython] G4_V  # scripted group (container) (typed FeaturePython)
  Dunit = g/cm3
  Dvalue = 6.11
  Group = -> [V_element001]
  conduct = 2
  density = 1
  expand = 3
  formula = V
  name = G4_V
  specific = 4
FEATURE [App::DocumentObjectGroupPython] Cr_element001  label="Cr_element : 1"  # scripted group (container) (typed FeaturePython)
  n = 1
  ref = Cr_element
FEATURE [App::DocumentObjectGroupPython] G4_Cr  # scripted group (container) (typed FeaturePython)
  Dunit = g/cm3
  Dvalue = 7.18
  Group = -> [Cr_element001]
  conduct = 2
  density = 1
  expand = 3
  formula = Cr
  name = G4_Cr
  specific = 4
FEATURE [App::DocumentObjectGroupPython] Mn_element001  label="Mn_element : 1"  # scripted group (container) (typed FeaturePython)
  n = 1
  ref = Mn_element
FEATURE [App::DocumentObjectGroupPython] G4_Mn  # scripted group (container) (typed FeaturePython)
  Dunit = g/cm3
  Dvalue = 7.44
  Group = -> [Mn_element001]
  conduct = 2
  density = 1
  expand = 3
  formula = Mn
  name = G4_Mn
  specific = 4
FEATURE [App::DocumentObjectGroupPython] Fe_element007  label="Fe_element : 004"  # scripted group (container) (typed FeaturePython)
  n = 1
  ref = Fe_element
FEATURE [App::DocumentObjectGroupPython] G4_Fe  # scripted group (container) (typed FeaturePython)
  Dunit = g/cm3
  Dvalue = 7.874
  Group = -> [Fe_element007]
  conduct = 2
  density = 1
  expand = 3
  formula = Fe
  name = G4_Fe
  specific = 4
FEATURE [App::DocumentObjectGroupPython] Co_element001  label="Co_element : 1"  # scripted group (container) (typed FeaturePython)
  n = 1
  ref = Co_element
FEATURE [App::DocumentObjectGroupPython] G4_Co  # scripted group (container) (typed FeaturePython)
  Dunit = g/cm3
  Dvalue = 8.9
  Group = -> [Co_element001]
  conduct = 2
  density = 1
  expand = 3
  formula = Co
  name = G4_Co
  specific = 4
FEATURE [App::DocumentObjectGroupPython] Ni_element001  label="Ni_element : 1"  # scripted group (container) (typed FeaturePython)
  n = 1
  ref = Ni_element
FEATURE [App::DocumentObjectGroupPython] G4_Ni  # scripted group (container) (typed FeaturePython)
  Dunit = g/cm3
  Dvalue = 8.902
  Group = -> [Ni_element001]
  conduct = 2
  density = 1
  expand = 3
  formula = Ni
  name = G4_Ni
  specific = 4
FEATURE [App::DocumentObjectGroupPython] Cu_element001  label="Cu_element : 1"  # scripted group (container) (typed FeaturePython)
  n = 1
  ref = Cu_element
FEATURE [App::DocumentObjectGroupPython] G4_Cu  # scripted group (container) (typed FeaturePython)
  Dunit = g/cm3
  Dvalue = 8.96
  Group = -> [Cu_element001]
  conduct = 2
  density = 1
  expand = 3
  formula = Cu
  name = G4_Cu
  specific = 4
FEATURE [App::DocumentObjectGroupPython] Zn_element001  label="Zn_element : 1"  # scripted group (container) (typed FeaturePython)
  n = 1
  ref = Zn_element
FEATURE [App::DocumentObjectGroupPython] G4_Zn  # scripted group (container) (typed FeaturePython)
  Dunit = g/cm3
  Dvalue = 7.133
  Group = -> [Zn_element001]
  conduct = 2
  density = 1
  expand = 3
  formula = Zn
  name = G4_Zn
  specific = 4
FEATURE [App::DocumentObjectGroupPython] Ga_element002  label="Ga_element : 002"  # scripted group (container) (typed FeaturePython)
  n = 1
  ref = Ga_element
FEATURE [App::DocumentObjectGroupPython] G4_Ga  # scripted group (container) (typed FeaturePython)
  Dunit = g/cm3
  Dvalue = 5.904
  Group = -> [Ga_element002]
  conduct = 2
  density = 1
  expand = 3
  formula = Ga
  name = G4_Ga
  specific = 4
FEATURE [App::DocumentObjectGroupPython] Ge_element002  label="Ge_element : 1"  # scripted group (container) (typed FeaturePython)
  n = 1
  ref = Ge_element
FEATURE [App::DocumentObjectGroupPython] G4_Ge  # scripted group (container) (typed FeaturePython)
  Dunit = g/cm3
  Dvalue = 5.323
  Group = -> [Ge_element002]
  conduct = 2
  density = 1
  expand = 3
  formula = Ge
  name = G4_Ge
  specific = 4
FEATURE [App::DocumentObjectGroupPython] As_element003  label="As_element : 002"  # scripted group (container) (typed FeaturePython)
  n = 1
  ref = As_element
FEATURE [App::DocumentObjectGroupPython] G4_As  # scripted group (container) (typed FeaturePython)
  Dunit = g/cm3
  Dvalue = 5.73
  Group = -> [As_element003]
  conduct = 2
  density = 1
  expand = 3
  formula = As
  name = G4_As
  specific = 4
FEATURE [App::DocumentObjectGroupPython] Se_element001  label="Se_element : 1"  # scripted group (container) (typed FeaturePython)
  n = 1
  ref = Se_element
FEATURE [App::DocumentObjectGroupPython] G4_Se  # scripted group (container) (typed FeaturePython)
  Dunit = g/cm3
  Dvalue = 4.5
  Group = -> [Se_element001]
  conduct = 2
  density = 1
  expand = 3
  formula = Se
  name = G4_Se
  specific = 4
FEATURE [App::DocumentObjectGroupPython] Br_element007  label="Br_element : 004"  # scripted group (container) (typed FeaturePython)
  n = 1
  ref = Br_element
FEATURE [App::DocumentObjectGroupPython] G4_Br  # scripted group (container) (typed FeaturePython)
  Dunit = g/cm3
  Dvalue = 0.0070721
  Group = -> [Br_element007]
  conduct = 2
  density = 1
  expand = 3
  formula = Br
  name = G4_Br
  specific = 4
FEATURE [App::DocumentObjectGroupPython] Kr_element001  label="Kr_element : 1"  # scripted group (container) (typed FeaturePython)
  n = 1
  ref = Kr_element
FEATURE [App::DocumentObjectGroupPython] G4_Kr  # scripted group (container) (typed FeaturePython)
  Dunit = g/cm3
  Dvalue = 0.00347832
  Group = -> [Kr_element001]
  conduct = 2
  density = 1
  expand = 3
  formula = Kr
  name = G4_Kr
  specific = 4
FEATURE [App::DocumentObjectGroupPython] Rb_element001  label="Rb_element : 1"  # scripted group (container) (typed FeaturePython)
  n = 1
  ref = Rb_element
FEATURE [App::DocumentObjectGroupPython] G4_Rb  # scripted group (container) (typed FeaturePython)
  Dunit = g/cm3
  Dvalue = 1.532
  Group = -> [Rb_element001]
  conduct = 2
  density = 1
  expand = 3
  formula = Rb
  name = G4_Rb
  specific = 4
FEATURE [App::DocumentObjectGroupPython] Sr_element001  label="Sr_element : 1"  # scripted group (container) (typed FeaturePython)
  n = 1
  ref = Sr_element
FEATURE [App::DocumentObjectGroupPython] G4_Sr  # scripted group (container) (typed FeaturePython)
  Dunit = g/cm3
  Dvalue = 2.54
  Group = -> [Sr_element001]
  conduct = 2
  density = 1
  expand = 3
  formula = Sr
  name = G4_Sr
  specific = 4
FEATURE [App::DocumentObjectGroupPython] Y_element001  label="Y_element : 1"  # scripted group (container) (typed FeaturePython)
  n = 1
  ref = Y_element
FEATURE [App::DocumentObjectGroupPython] G4_Y  # scripted group (container) (typed FeaturePython)
  Dunit = g/cm3
  Dvalue = 4.469
  Group = -> [Y_element001]
  conduct = 2
  density = 1
  expand = 3
  formula = Y
  name = G4_Y
  specific = 4
FEATURE [App::DocumentObjectGroupPython] Zr_element001  label="Zr_element : 1"  # scripted group (container) (typed FeaturePython)
  n = 1
  ref = Zr_element
FEATURE [App::DocumentObjectGroupPython] G4_Zr  # scripted group (container) (typed FeaturePython)
  Dunit = g/cm3
  Dvalue = 6.506
  Group = -> [Zr_element001]
  conduct = 2
  density = 1
  expand = 3
  formula = Zr
  name = G4_Zr
  specific = 4
FEATURE [App::DocumentObjectGroupPython] Nb_element001  label="Nb_element : 1"  # scripted group (container) (typed FeaturePython)
  n = 1
  ref = Nb_element
FEATURE [App::DocumentObjectGroupPython] G4_Nb  # scripted group (container) (typed FeaturePython)
  Dunit = g/cm3
  Dvalue = 8.57
  Group = -> [Nb_element001]
  conduct = 2
  density = 1
  expand = 3
  formula = Nb
  name = G4_Nb
  specific = 4
FEATURE [App::DocumentObjectGroupPython] Mo_element001  label="Mo_element : 1"  # scripted group (container) (typed FeaturePython)
  n = 1
  ref = Mo_element
FEATURE [App::DocumentObjectGroupPython] G4_Mo  # scripted group (container) (typed FeaturePython)
  Dunit = g/cm3
  Dvalue = 10.22
  Group = -> [Mo_element001]
  conduct = 2
  density = 1
  expand = 3
  formula = Mo
  name = G4_Mo
  specific = 4
FEATURE [App::DocumentObjectGroupPython] Tc_element001  label="Tc_element : 1"  # scripted group (container) (typed FeaturePython)
  n = 1
  ref = Tc_element
FEATURE [App::DocumentObjectGroupPython] G4_Tc  # scripted group (container) (typed FeaturePython)
  Dunit = g/cm3
  Dvalue = 11.5
  Group = -> [Tc_element001]
  conduct = 2
  density = 1
  expand = 3
  formula = Tc
  name = G4_Tc
  specific = 4
FEATURE [App::DocumentObjectGroupPython] Ru_element001  label="Ru_element : 1"  # scripted group (container) (typed FeaturePython)
  n = 1
  ref = Ru_element
FEATURE [App::DocumentObjectGroupPython] G4_Ru  # scripted group (container) (typed FeaturePython)
  Dunit = g/cm3
  Dvalue = 12.41
  Group = -> [Ru_element001]
  conduct = 2
  density = 1
  expand = 3
  formula = Ru
  name = G4_Ru
  specific = 4
FEATURE [App::DocumentObjectGroupPython] Rh_element001  label="Rh_element : 1"  # scripted group (container) (typed FeaturePython)
  n = 1
  ref = Rh_element
FEATURE [App::DocumentObjectGroupPython] G4_Rh  # scripted group (container) (typed FeaturePython)
  Dunit = g/cm3
  Dvalue = 12.41
  Group = -> [Rh_element001]
  conduct = 2
  density = 1
  expand = 3
  formula = Rh
  name = G4_Rh
  specific = 4
FEATURE [App::DocumentObjectGroupPython] Pd_element001  label="Pd_element : 1"  # scripted group (container) (typed FeaturePython)
  n = 1
  ref = Pd_element
FEATURE [App::DocumentObjectGroupPython] G4_Pd  # scripted group (container) (typed FeaturePython)
  Dunit = g/cm3
  Dvalue = 12.02
  Group = -> [Pd_element001]
  conduct = 2
  density = 1
  expand = 3
  formula = Pd
  name = G4_Pd
  specific = 4
FEATURE [App::DocumentObjectGroupPython] Ag_element006  label="Ag_element : 004"  # scripted group (container) (typed FeaturePython)
  n = 1
  ref = Ag_element
FEATURE [App::DocumentObjectGroupPython] G4_Ag  # scripted group (container) (typed FeaturePython)
  Dunit = g/cm3
  Dvalue = 10.5
  Group = -> [Ag_element006]
  conduct = 2
  density = 1
  expand = 3
  formula = Ag
  name = G4_Ag
  specific = 4
FEATURE [App::DocumentObjectGroupPython] Cd_element003  label="Cd_element : 003"  # scripted group (container) (typed FeaturePython)
  n = 1
  ref = Cd_element
FEATURE [App::DocumentObjectGroupPython] G4_Cd  # scripted group (container) (typed FeaturePython)
  Dunit = g/cm3
  Dvalue = 8.65
  Group = -> [Cd_element003]
  conduct = 2
  density = 1
  expand = 3
  formula = Cd
  name = G4_Cd
  specific = 4
FEATURE [App::DocumentObjectGroupPython] In_element001  label="In_element : 1"  # scripted group (container) (typed FeaturePython)
  n = 1
  ref = In_element
FEATURE [App::DocumentObjectGroupPython] G4_In  # scripted group (container) (typed FeaturePython)
  Dunit = g/cm3
  Dvalue = 7.31
  Group = -> [In_element001]
  conduct = 2
  density = 1
  expand = 3
  formula = In
  name = G4_In
  specific = 4
FEATURE [App::DocumentObjectGroupPython] Sn_element001  label="Sn_element : 1"  # scripted group (container) (typed FeaturePython)
  n = 1
  ref = Sn_element
FEATURE [App::DocumentObjectGroupPython] G4_Sn  # scripted group (container) (typed FeaturePython)
  Dunit = g/cm3
  Dvalue = 7.31
  Group = -> [Sn_element001]
  conduct = 2
  density = 1
  expand = 3
  formula = Sn
  name = G4_Sn
  specific = 4
FEATURE [App::DocumentObjectGroupPython] Sb_element001  label="Sb_element : 1"  # scripted group (container) (typed FeaturePython)
  n = 1
  ref = Sb_element
FEATURE [App::DocumentObjectGroupPython] G4_Sb  # scripted group (container) (typed FeaturePython)
  Dunit = g/cm3
  Dvalue = 6.691
  Group = -> [Sb_element001]
  conduct = 2
  density = 1
  expand = 3
  formula = Sb
  name = G4_Sb
  specific = 4
FEATURE [App::DocumentObjectGroupPython] Te_element002  label="Te_element : 002"  # scripted group (container) (typed FeaturePython)
  n = 1
  ref = Te_element
FEATURE [App::DocumentObjectGroupPython] G4_Te  # scripted group (container) (typed FeaturePython)
  Dunit = g/cm3
  Dvalue = 6.24
  Group = -> [Te_element002]
  conduct = 2
  density = 1
  expand = 3
  formula = Te
  name = G4_Te
  specific = 4
FEATURE [App::DocumentObjectGroupPython] I_element010  label="I_element : 006"  # scripted group (container) (typed FeaturePython)
  n = 1
  ref = I_element
FEATURE [App::DocumentObjectGroupPython] G4_I  # scripted group (container) (typed FeaturePython)
  Dunit = g/cm3
  Dvalue = 4.93
  Group = -> [I_element010]
  conduct = 2
  density = 1
  expand = 3
  formula = I
  name = G4_I
  specific = 4
FEATURE [App::DocumentObjectGroupPython] Xe_element001  label="Xe_element : 1"  # scripted group (container) (typed FeaturePython)
  n = 1
  ref = Xe_element
FEATURE [App::DocumentObjectGroupPython] G4_Xe  # scripted group (container) (typed FeaturePython)
  Dunit = g/cm3
  Dvalue = 0.00548536
  Group = -> [Xe_element001]
  conduct = 2
  density = 1
  expand = 3
  formula = Xe
  name = G4_Xe
  specific = 4
FEATURE [App::DocumentObjectGroupPython] Cs_element003  label="Cs_element : 003"  # scripted group (container) (typed FeaturePython)
  n = 1
  ref = Cs_element
FEATURE [App::DocumentObjectGroupPython] G4_Cs  # scripted group (container) (typed FeaturePython)
  Dunit = g/cm3
  Dvalue = 1.873
  Group = -> [Cs_element003]
  conduct = 2
  density = 1
  expand = 3
  formula = Cs
  name = G4_Cs
  specific = 4
FEATURE [App::DocumentObjectGroupPython] Ba_element003  label="Ba_element : 003"  # scripted group (container) (typed FeaturePython)
  n = 1
  ref = Ba_element
FEATURE [App::DocumentObjectGroupPython] G4_Ba  # scripted group (container) (typed FeaturePython)
  Dunit = g/cm3
  Dvalue = 3.5
  Group = -> [Ba_element003]
  conduct = 2
  density = 1
  expand = 3
  formula = Ba
  name = G4_Ba
  specific = 4
FEATURE [App::DocumentObjectGroupPython] La_element003  label="La_element : 003"  # scripted group (container) (typed FeaturePython)
  n = 1
  ref = La_element
FEATURE [App::DocumentObjectGroupPython] G4_La  # scripted group (container) (typed FeaturePython)
  Dunit = g/cm3
  Dvalue = 6.154
  Group = -> [La_element003]
  conduct = 2
  density = 1
  expand = 3
  formula = La
  name = G4_La
  specific = 4
FEATURE [App::DocumentObjectGroupPython] Ce_element002  label="Ce_element : 1"  # scripted group (container) (typed FeaturePython)
  n = 1
  ref = Ce_element
FEATURE [App::DocumentObjectGroupPython] G4_Ce  # scripted group (container) (typed FeaturePython)
  Dunit = g/cm3
  Dvalue = 6.657
  Group = -> [Ce_element002]
  conduct = 2
  density = 1
  expand = 3
  formula = Ce
  name = G4_Ce
  specific = 4
FEATURE [App::DocumentObjectGroupPython] Pr_element001  label="Pr_element : 1"  # scripted group (container) (typed FeaturePython)
  n = 1
  ref = Pr_element
FEATURE [App::DocumentObjectGroupPython] G4_Pr  # scripted group (container) (typed FeaturePython)
  Dunit = g/cm3
  Dvalue = 6.71
  Group = -> [Pr_element001]
  conduct = 2
  density = 1
  expand = 3
  formula = Pr
  name = G4_Pr
  specific = 4
FEATURE [App::DocumentObjectGroupPython] Nd_element001  label="Nd_element : 1"  # scripted group (container) (typed FeaturePython)
  n = 1
  ref = Nd_element
FEATURE [App::DocumentObjectGroupPython] G4_Nd  # scripted group (container) (typed FeaturePython)
  Dunit = g/cm3
  Dvalue = 6.9
  Group = -> [Nd_element001]
  conduct = 2
  density = 1
  expand = 3
  formula = Nd
  name = G4_Nd
  specific = 4
FEATURE [App::DocumentObjectGroupPython] Pm_element001  label="Pm_element : 1"  # scripted group (container) (typed FeaturePython)
  n = 1
  ref = Pm_element
FEATURE [App::DocumentObjectGroupPython] G4_Pm  # scripted group (container) (typed FeaturePython)
  Dunit = g/cm3
  Dvalue = 7.22
  Group = -> [Pm_element001]
  conduct = 2
  density = 1
  expand = 3
  formula = Pm
  name = G4_Pm
  specific = 4
FEATURE [App::DocumentObjectGroupPython] Sm_element001  label="Sm_element : 1"  # scripted group (container) (typed FeaturePython)
  n = 1
  ref = Sm_element
FEATURE [App::DocumentObjectGroupPython] G4_Sm  # scripted group (container) (typed FeaturePython)
  Dunit = g/cm3
  Dvalue = 7.46
  Group = -> [Sm_element001]
  conduct = 2
  density = 1
  expand = 3
  formula = Sm
  name = G4_Sm
  specific = 4
FEATURE [App::DocumentObjectGroupPython] Eu_element001  label="Eu_element : 1"  # scripted group (container) (typed FeaturePython)
  n = 1
  ref = Eu_element
FEATURE [App::DocumentObjectGroupPython] G4_Eu  # scripted group (container) (typed FeaturePython)
  Dunit = g/cm3
  Dvalue = 5.243
  Group = -> [Eu_element001]
  conduct = 2
  density = 1
  expand = 3
  formula = Eu
  name = G4_Eu
  specific = 4
FEATURE [App::DocumentObjectGroupPython] Gd_element002  label="Gd_element : 1"  # scripted group (container) (typed FeaturePython)
  n = 1
  ref = Gd_element
FEATURE [App::DocumentObjectGroupPython] G4_Gd  # scripted group (container) (typed FeaturePython)
  Dunit = g/cm3
  Dvalue = 7.9004
  Group = -> [Gd_element002]
  conduct = 2
  density = 1
  expand = 3
  formula = Gd
  name = G4_Gd
  specific = 4
FEATURE [App::DocumentObjectGroupPython] Tb_element001  label="Tb_element : 1"  # scripted group (container) (typed FeaturePython)
  n = 1
  ref = Tb_element
FEATURE [App::DocumentObjectGroupPython] G4_Tb  # scripted group (container) (typed FeaturePython)
  Dunit = g/cm3
  Dvalue = 8.229
  Group = -> [Tb_element001]
  conduct = 2
  density = 1
  expand = 3
  formula = Tb
  name = G4_Tb
  specific = 4
FEATURE [App::DocumentObjectGroupPython] Dy_element001  label="Dy_element : 1"  # scripted group (container) (typed FeaturePython)
  n = 1
  ref = Dy_element
FEATURE [App::DocumentObjectGroupPython] G4_Dy  # scripted group (container) (typed FeaturePython)
  Dunit = g/cm3
  Dvalue = 8.55
  Group = -> [Dy_element001]
  conduct = 2
  density = 1
  expand = 3
  formula = Dy
  name = G4_Dy
  specific = 4
FEATURE [App::DocumentObjectGroupPython] Ho_element001  label="Ho_element : 1"  # scripted group (container) (typed FeaturePython)
  n = 1
  ref = Ho_element
FEATURE [App::DocumentObjectGroupPython] G4_Ho  # scripted group (container) (typed FeaturePython)
  Dunit = g/cm3
  Dvalue = 8.795
  Group = -> [Ho_element001]
  conduct = 2
  density = 1
  expand = 3
  formula = Ho
  name = G4_Ho
  specific = 4
FEATURE [App::DocumentObjectGroupPython] Er_element001  label="Er_element : 1"  # scripted group (container) (typed FeaturePython)
  n = 1
  ref = Er_element
FEATURE [App::DocumentObjectGroupPython] G4_Er  # scripted group (container) (typed FeaturePython)
  Dunit = g/cm3
  Dvalue = 9.066
  Group = -> [Er_element001]
  conduct = 2
  density = 1
  expand = 3
  formula = Er
  name = G4_Er
  specific = 4
FEATURE [App::DocumentObjectGroupPython] Tm_element001  label="Tm_element : 1"  # scripted group (container) (typed FeaturePython)
  n = 1
  ref = Tm_element
FEATURE [App::DocumentObjectGroupPython] G4_Tm  # scripted group (container) (typed FeaturePython)
  Dunit = g/cm3
  Dvalue = 9.321
  Group = -> [Tm_element001]
  conduct = 2
  density = 1
  expand = 3
  formula = Tm
  name = G4_Tm
  specific = 4
FEATURE [App::DocumentObjectGroupPython] Yb_element001  label="Yb_element : 1"  # scripted group (container) (typed FeaturePython)
  n = 1
  ref = Yb_element
FEATURE [App::DocumentObjectGroupPython] G4_Yb  # scripted group (container) (typed FeaturePython)
  Dunit = g/cm3
  Dvalue = 6.73
  Group = -> [Yb_element001]
  conduct = 2
  density = 1
  expand = 3
  formula = Yb
  name = G4_Yb
  specific = 4
FEATURE [App::DocumentObjectGroupPython] Lu_element001  label="Lu_element : 1"  # scripted group (container) (typed FeaturePython)
  n = 1
  ref = Lu_element
FEATURE [App::DocumentObjectGroupPython] G4_Lu  # scripted group (container) (typed FeaturePython)
  Dunit = g/cm3
  Dvalue = 9.84
  Group = -> [Lu_element001]
  conduct = 2
  density = 1
  expand = 3
  formula = Lu
  name = G4_Lu
  specific = 4
FEATURE [App::DocumentObjectGroupPython] Hf_element001  label="Hf_element : 1"  # scripted group (container) (typed FeaturePython)
  n = 1
  ref = Hf_element
FEATURE [App::DocumentObjectGroupPython] G4_Hf  # scripted group (container) (typed FeaturePython)
  Dunit = g/cm3
  Dvalue = 13.31
  Group = -> [Hf_element001]
  conduct = 2
  density = 1
  expand = 3
  formula = Hf
  name = G4_Hf
  specific = 4
FEATURE [App::DocumentObjectGroupPython] Ta_element001  label="Ta_element : 1"  # scripted group (container) (typed FeaturePython)
  n = 1
  ref = Ta_element
FEATURE [App::DocumentObjectGroupPython] G4_Ta  # scripted group (container) (typed FeaturePython)
  Dunit = g/cm3
  Dvalue = 16.654
  Group = -> [Ta_element001]
  conduct = 2
  density = 1
  expand = 3
  formula = Ta
  name = G4_Ta
  specific = 4
FEATURE [App::DocumentObjectGroupPython] W_element004  label="W_element : 004"  # scripted group (container) (typed FeaturePython)
  n = 1
  ref = W_element
FEATURE [App::DocumentObjectGroupPython] G4_W  # scripted group (container) (typed FeaturePython)
  Dunit = g/cm3
  Dvalue = 19.3
  Group = -> [W_element004]
  conduct = 2
  density = 1
  expand = 3
  formula = W
  name = G4_W
  specific = 4
FEATURE [App::DocumentObjectGroupPython] Re_element001  label="Re_element : 1"  # scripted group (container) (typed FeaturePython)
  n = 1
  ref = Re_element
FEATURE [App::DocumentObjectGroupPython] G4_Re  # scripted group (container) (typed FeaturePython)
  Dunit = g/cm3
  Dvalue = 21.02
  Group = -> [Re_element001]
  conduct = 2
  density = 1
  expand = 3
  formula = Re
  name = G4_Re
  specific = 4
FEATURE [App::DocumentObjectGroupPython] Os_element001  label="Os_element : 1"  # scripted group (container) (typed FeaturePython)
  n = 1
  ref = Os_element
FEATURE [App::DocumentObjectGroupPython] G4_Os  # scripted group (container) (typed FeaturePython)
  Dunit = g/cm3
  Dvalue = 22.57
  Group = -> [Os_element001]
  conduct = 2
  density = 1
  expand = 3
  formula = Os
  name = G4_Os
  specific = 4
FEATURE [App::DocumentObjectGroupPython] Ir_element001  label="Ir_element : 1"  # scripted group (container) (typed FeaturePython)
  n = 1
  ref = Ir_element
FEATURE [App::DocumentObjectGroupPython] G4_Ir  # scripted group (container) (typed FeaturePython)
  Dunit = g/cm3
  Dvalue = 22.42
  Group = -> [Ir_element001]
  conduct = 2
  density = 1
  expand = 3
  formula = Ir
  name = G4_Ir
  specific = 4
FEATURE [App::DocumentObjectGroupPython] Pt_element001  label="Pt_element : 1"  # scripted group (container) (typed FeaturePython)
  n = 1
  ref = Pt_element
FEATURE [App::DocumentObjectGroupPython] G4_Pt  # scripted group (container) (typed FeaturePython)
  Dunit = g/cm3
  Dvalue = 21.45
  Group = -> [Pt_element001]
  conduct = 2
  density = 1
  expand = 3
  formula = Pt
  name = G4_Pt
  specific = 4
FEATURE [App::DocumentObjectGroupPython] Au_element001  label="Au_element : 1"  # scripted group (container) (typed FeaturePython)
  n = 1
  ref = Au_element
FEATURE [App::DocumentObjectGroupPython] G4_Au  # scripted group (container) (typed FeaturePython)
  Dunit = g/cm3
  Dvalue = 19.32
  Group = -> [Au_element001]
  conduct = 2
  density = 1
  expand = 3
  formula = Au
  name = G4_Au
  specific = 4
FEATURE [App::DocumentObjectGroupPython] Hg_element002  label="Hg_element : 002"  # scripted group (container) (typed FeaturePython)
  n = 1
  ref = Hg_element
FEATURE [App::DocumentObjectGroupPython] G4_Hg  # scripted group (container) (typed FeaturePython)
  Dunit = g/cm3
  Dvalue = 13.546
  Group = -> [Hg_element002]
  conduct = 2
  density = 1
  expand = 3
  formula = Hg
  name = G4_Hg
  specific = 4
FEATURE [App::DocumentObjectGroupPython] Tl_element002  label="Tl_element : 002"  # scripted group (container) (typed FeaturePython)
  n = 1
  ref = Tl_element
FEATURE [App::DocumentObjectGroupPython] G4_Tl  # scripted group (container) (typed FeaturePython)
  Dunit = g/cm3
  Dvalue = 11.72
  Group = -> [Tl_element002]
  conduct = 2
  density = 1
  expand = 3
  formula = Tl
  name = G4_Tl
  specific = 4
FEATURE [App::DocumentObjectGroupPython] Pb_element003  label="Pb_element : 1"  # scripted group (container) (typed FeaturePython)
  n = 1
  ref = Pb_element
FEATURE [App::DocumentObjectGroupPython] G4_Pb  # scripted group (container) (typed FeaturePython)
  Dunit = g/cm3
  Dvalue = 11.35
  Group = -> [Pb_element003]
  conduct = 2
  density = 1
  expand = 3
  formula = Pb
  name = G4_Pb
  specific = 4
FEATURE [App::DocumentObjectGroupPython] Bi_element002  label="Bi_element : 1"  # scripted group (container) (typed FeaturePython)
  n = 1
  ref = Bi_element
FEATURE [App::DocumentObjectGroupPython] G4_Bi  # scripted group (container) (typed FeaturePython)
  Dunit = g/cm3
  Dvalue = 9.747
  Group = -> [Bi_element002]
  conduct = 2
  density = 1
  expand = 3
  formula = Bi
  name = G4_Bi
  specific = 4
FEATURE [App::DocumentObjectGroupPython] Po_element001  label="Po_element : 1"  # scripted group (container) (typed FeaturePython)
  n = 1
  ref = Po_element
FEATURE [App::DocumentObjectGroupPython] G4_Po  # scripted group (container) (typed FeaturePython)
  Dunit = g/cm3
  Dvalue = 9.32
  Group = -> [Po_element001]
  conduct = 2
  density = 1
  expand = 3
  formula = Po
  name = G4_Po
  specific = 4
FEATURE [App::DocumentObjectGroupPython] At_element001  label="At_element : 1"  # scripted group (container) (typed FeaturePython)
  n = 1
  ref = At_element
FEATURE [App::DocumentObjectGroupPython] G4_At  # scripted group (container) (typed FeaturePython)
  Dunit = g/cm3
  Dvalue = 9.32
  Group = -> [At_element001]
  conduct = 2
  density = 1
  expand = 3
  formula = At
  name = G4_At
  specific = 4
FEATURE [App::DocumentObjectGroupPython] Rn_element001  label="Rn_element : 1"  # scripted group (container) (typed FeaturePython)
  n = 1
  ref = Rn_element
FEATURE [App::DocumentObjectGroupPython] G4_Rn  # scripted group (container) (typed FeaturePython)
  Dunit = g/cm3
  Dvalue = 0.00900662
  Group = -> [Rn_element001]
  conduct = 2
  density = 1
  expand = 3
  formula = Rn
  name = G4_Rn
  specific = 4
FEATURE [App::DocumentObjectGroupPython] Fr_element001  label="Fr_element : 1"  # scripted group (container) (typed FeaturePython)
  n = 1
  ref = Fr_element
FEATURE [App::DocumentObjectGroupPython] G4_Fr  # scripted group (container) (typed FeaturePython)
  Dunit = g/cm3
  Dvalue = 1
  Group = -> [Fr_element001]
  conduct = 2
  density = 1
  expand = 3
  formula = Fr
  name = G4_Fr
  specific = 4
FEATURE [App::DocumentObjectGroupPython] Ra_element001  label="Ra_element : 1"  # scripted group (container) (typed FeaturePython)
  n = 1
  ref = Ra_element
FEATURE [App::DocumentObjectGroupPython] G4_Ra  # scripted group (container) (typed FeaturePython)
  Dunit = g/cm3
  Dvalue = 5
  Group = -> [Ra_element001]
  conduct = 2
  density = 1
  expand = 3
  formula = Ra
  name = G4_Ra
  specific = 4
FEATURE [App::DocumentObjectGroupPython] Ac_element001  label="Ac_element : 1"  # scripted group (container) (typed FeaturePython)
  n = 1
  ref = Ac_element
FEATURE [App::DocumentObjectGroupPython] G4_Ac  # scripted group (container) (typed FeaturePython)
  Dunit = g/cm3
  Dvalue = 10.07
  Group = -> [Ac_element001]
  conduct = 2
  density = 1
  expand = 3
  formula = Ac
  name = G4_Ac
  specific = 4
FEATURE [App::DocumentObjectGroupPython] Th_element001  label="Th_element : 1"  # scripted group (container) (typed FeaturePython)
  n = 1
  ref = Th_element
FEATURE [App::DocumentObjectGroupPython] G4_Th  # scripted group (container) (typed FeaturePython)
  Dunit = g/cm3
  Dvalue = 11.72
  Group = -> [Th_element001]
  conduct = 2
  density = 1
  expand = 3
  formula = Th
  name = G4_Th
  specific = 4
FEATURE [App::DocumentObjectGroupPython] Pa_element001  label="Pa_element : 1"  # scripted group (container) (typed FeaturePython)
  n = 1
  ref = Pa_element
FEATURE [App::DocumentObjectGroupPython] G4_Pa  # scripted group (container) (typed FeaturePython)
  Dunit = g/cm3
  Dvalue = 15.37
  Group = -> [Pa_element001]
  conduct = 2
  density = 1
  expand = 3
  formula = Pa
  name = G4_Pa
  specific = 4
FEATURE [App::DocumentObjectGroupPython] U_element004  label="U_element : 004"  # scripted group (container) (typed FeaturePython)
  n = 1
  ref = U_element
FEATURE [App::DocumentObjectGroupPython] G4_U  # scripted group (container) (typed FeaturePython)
  Dunit = g/cm3
  Dvalue = 18.95
  Group = -> [U_element004]
  conduct = 2
  density = 1
  expand = 3
  formula = U
  name = G4_U
  specific = 4
FEATURE [App::DocumentObjectGroupPython] Np_element001  label="Np_element : 1"  # scripted group (container) (typed FeaturePython)
  n = 1
  ref = Np_element
FEATURE [App::DocumentObjectGroupPython] G4_Np  # scripted group (container) (typed FeaturePython)
  Dunit = g/cm3
  Dvalue = 20.25
  Group = -> [Np_element001]
  conduct = 2
  density = 1
  expand = 3
  formula = Np
  name = G4_Np
  specific = 4
FEATURE [App::DocumentObjectGroupPython] Pu_element002  label="Pu_element : 002"  # scripted group (container) (typed FeaturePython)
  n = 1
  ref = Pu_element
FEATURE [App::DocumentObjectGroupPython] G4_Pu  # scripted group (container) (typed FeaturePython)
  Dunit = g/cm3
  Dvalue = 19.84
  Group = -> [Pu_element002]
  conduct = 2
  density = 1
  expand = 3
  formula = Pu
  name = G4_Pu
  specific = 4
FEATURE [App::DocumentObjectGroupPython] Am_element001  label="Am_element : 1"  # scripted group (container) (typed FeaturePython)
  n = 1
  ref = Am_element
FEATURE [App::DocumentObjectGroupPython] G4_Am  # scripted group (container) (typed FeaturePython)
  Dunit = g/cm3
  Dvalue = 13.67
  Group = -> [Am_element001]
  conduct = 2
  density = 1
  expand = 3
  formula = Am
  name = G4_Am
  specific = 4
FEATURE [App::DocumentObjectGroupPython] Cm_element001  label="Cm_element : 1"  # scripted group (container) (typed FeaturePython)
  n = 1
  ref = Cm_element
FEATURE [App::DocumentObjectGroupPython] G4_Cm  # scripted group (container) (typed FeaturePython)
  Dunit = g/cm3
  Dvalue = 13.51
  Group = -> [Cm_element001]
  conduct = 2
  density = 1
  expand = 3
  formula = Cm
  name = G4_Cm
  specific = 4
FEATURE [App::DocumentObjectGroupPython] Bk_element001  label="Bk_element : 1"  # scripted group (container) (typed FeaturePython)
  n = 1
  ref = Bk_element
FEATURE [App::DocumentObjectGroupPython] G4_Bk  # scripted group (container) (typed FeaturePython)
  Dunit = g/cm3
  Dvalue = 14
  Group = -> [Bk_element001]
  conduct = 2
  density = 1
  expand = 3
  formula = Bk
  name = G4_Bk
  specific = 4
FEATURE [App::DocumentObjectGroupPython] Cf_element001  label="Cf_element : 1"  # scripted group (container) (typed FeaturePython)
  n = 1
  ref = Cf_element
FEATURE [App::DocumentObjectGroupPython] G4_Cf  # scripted group (container) (typed FeaturePython)
  Dunit = g/cm3
  Dvalue = 10
  Group = -> [Cf_element001]
  conduct = 2
  density = 1
  expand = 3
  formula = Cf
  name = G4_Cf
  specific = 4
FEATURE [App::DocumentObjectGroupPython] Element  # scripted group (container) (typed FeaturePython)
  Group = -> [G4_H,G4_He,G4_Li,G4_Be,G4_B,G4_C,G4_N,G4_O,G4_F,G4_Ne,G4_Na,G4_Mg,G4_Al,G4_Si,G4_P,G4_S,G4_Cl,G4_Ar,G4_K,G4_Ca,G4_Sc,G4_Ti,G4_V,G4_Cr,G4_Mn,G4_Fe,G4_Co,G4_Ni,G4_Cu,G4_Zn,G4_Ga,G4_Ge,G4_As,G4_Se,G4_Br,G4_Kr,G4_Rb,G4_Sr,G4_Y,G4_Zr,G4_Nb,G4_Mo,G4_Tc,G4_Ru,G4_Rh,G4_Pd,G4_Ag,G4_Cd,G4_In,G4_Sn,G4_Sb,G4_Te,G4_I,G4_Xe,G4_Cs,G4_Ba,G4_La,G4_Ce,G4_Pr,G4_Nd,G4_Pm,G4_Sm,G4_Eu,G4_Gd,G4_Tb,G4_Dy,G4_Ho,G4_Er,+30 more]
FEATURE [App::DocumentObjectGroupPython] H_element114  label="H_element : 063"  # scripted group (container) (typed FeaturePython)
  n = 2
  ref = H_element
FEATURE [App::DocumentObjectGroupPython] G4_lH2  # scripted group (container) (typed FeaturePython)
  Dunit = g/cm3
  Dvalue = 0.0708
  Group = -> [H_element114]
  conduct = 2
  density = 1
  expand = 3
  formula = G4_lH2
  name = G4_lH2
  specific = 4
FEATURE [App::DocumentObjectGroupPython] N_element049  label="N_element : 022"  # scripted group (container) (typed FeaturePython)
  n = 2
  ref = N_element
FEATURE [App::DocumentObjectGroupPython] G4_lN2  # scripted group (container) (typed FeaturePython)
  Dunit = g/cm3
  Dvalue = 0.807
  Group = -> [N_element049]
  conduct = 2
  density = 1
  expand = 3
  formula = G4_lN2
  name = G4_lN2
  specific = 4
FEATURE [App::DocumentObjectGroupPython] O_element106  label="O_element : 060"  # scripted group (container) (typed FeaturePython)
  n = 2
  ref = O_element
FEATURE [App::DocumentObjectGroupPython] G4_lO2  # scripted group (container) (typed FeaturePython)
  Dunit = g/cm3
  Dvalue = 1.141
  Group = -> [O_element106]
  conduct = 2
  density = 1
  expand = 3
  formula = G4_lO2
  name = G4_lO2
  specific = 4
FEATURE [App::DocumentObjectGroupPython] Ar  label="Ar : 1"  # scripted group (container) (typed FeaturePython)
  n = 1
  ref = Ar
FEATURE [App::DocumentObjectGroupPython] G4_lAr  # scripted group (container) (typed FeaturePython)
  Dunit = g/cm3
  Dvalue = 1.396
  Group = -> [Ar]
  conduct = 2
  density = 1
  expand = 3
  formula = G4_lAr
  name = G4_lAr
  specific = 4
FEATURE [App::DocumentObjectGroupPython] Br  label="Br : 1"  # scripted group (container) (typed FeaturePython)
  n = 1
  ref = Br
FEATURE [App::DocumentObjectGroupPython] G4_lBr  # scripted group (container) (typed FeaturePython)
  Dunit = g/cm3
  Dvalue = 3.1028
  Group = -> [Br]
  conduct = 2
  density = 1
  expand = 3
  formula = G4_lBr
  name = G4_lBr
  specific = 4
FEATURE [App::DocumentObjectGroupPython] Kr  label="Kr : 1"  # scripted group (container) (typed FeaturePython)
  n = 1
  ref = Kr
FEATURE [App::DocumentObjectGroupPython] G4_lKr  # scripted group (container) (typed FeaturePython)
  Dunit = g/cm3
  Dvalue = 2.418
  Group = -> [Kr]
  conduct = 2
  density = 1
  expand = 3
  formula = G4_lKr
  name = G4_lKr
  specific = 4
FEATURE [App::DocumentObjectGroupPython] Xe  label="Xe : 1"  # scripted group (container) (typed FeaturePython)
  n = 1
  ref = Xe
FEATURE [App::DocumentObjectGroupPython] G4_lXe  # scripted group (container) (typed FeaturePython)
  Dunit = g/cm3
  Dvalue = 2.953
  Group = -> [Xe]
  conduct = 2
  density = 1
  expand = 3
  formula = G4_lXe
  name = G4_lXe
  specific = 4
FEATURE [App::DocumentObjectGroupPython] O_element107  label="O_element : 061"  # scripted group (container) (typed FeaturePython)
  n = 4
  ref = O_element
FEATURE [App::DocumentObjectGroupPython] Pb_element004  label="Pb_element : 002"  # scripted group (container) (typed FeaturePython)
  n = 1
  ref = Pb_element
FEATURE [App::DocumentObjectGroupPython] W_element005  label="W_element : 005"  # scripted group (container) (typed FeaturePython)
  n = 1
  ref = W_element
FEATURE [App::DocumentObjectGroupPython] G4_PbWO4  # scripted group (container) (typed FeaturePython)
  Dunit = g/cm3
  Dvalue = 8.28
  Group = -> [O_element107,Pb_element004,W_element005]
  conduct = 2
  density = 1
  expand = 3
  formula = G4_PbWO4
  name = G4_PbWO4
  specific = 4
FEATURE [App::DocumentObjectGroupPython] alactic  label="alactic : 1"  # scripted group (container) (typed FeaturePython)
  n = 1
  ref = alactic
FEATURE [App::DocumentObjectGroupPython] G4_Galactic  # scripted group (container) (typed FeaturePython)
  Dunit = g/cm3
  Dvalue = 0
  Group = -> [alactic]
  conduct = 2
  density = 1
  expand = 3
  formula = G4_Galactic
  name = G4_Galactic
  specific = 4
FEATURE [App::DocumentObjectGroupPython] RAPHITE_POROUS  label="RAPHITE_POROUS : 1"  # scripted group (container) (typed FeaturePython)
  n = 1
  ref = RAPHITE_POROUS
FEATURE [App::DocumentObjectGroupPython] G4_GRAPHITE_POROUS  # scripted group (container) (typed FeaturePython)
  Dunit = g/cm3
  Dvalue = 1.7
  Group = -> [RAPHITE_POROUS]
  conduct = 2
  density = 1
  expand = 3
  formula = G4_GRAPHITE_POROUS
  name = G4_GRAPHITE_POROUS
  specific = 4
FEATURE [App::DocumentObjectGroupPython] H_element115  label="H_element : 0.150"  # scripted group (container) (typed FeaturePython)
  n = 0.080538
FEATURE [App::DocumentObjectGroupPython] C_element125  label="C_element : 0.600"  # scripted group (container) (typed FeaturePython)
  n = 0.599848
FEATURE [App::DocumentObjectGroupPython] O_element108  label="O_element : 0.320"  # scripted group (container) (typed FeaturePython)
  n = 0.319614
FEATURE [App::DocumentObjectGroupPython] G4_LUCITE  # scripted group (container) (typed FeaturePython)
  Dunit = g/cm3
  Dvalue = 1.19
  Group = -> [H_element115,C_element125,O_element108]
  conduct = 2
  density = 1
  expand = 3
  formula = G4_LUCITE
  name = G4_LUCITE
  specific = 4
FEATURE [App::DocumentObjectGroupPython] Cu_element002  label="Cu_element : 62"  # scripted group (container) (typed FeaturePython)
  n = 62
  ref = Cu_element
FEATURE [App::DocumentObjectGroupPython] Zn_element002  label="Zn_element : 35"  # scripted group (container) (typed FeaturePython)
  n = 35
  ref = Zn_element
FEATURE [App::DocumentObjectGroupPython] Pb_element005  label="Pb_element : 3"  # scripted group (container) (typed FeaturePython)
  n = 3
  ref = Pb_element
FEATURE [App::DocumentObjectGroupPython] G4_BRASS  # scripted group (container) (typed FeaturePython)
  Dunit = g/cm3
  Dvalue = 8.52
  Group = -> [Cu_element002,Zn_element002,Pb_element005]
  conduct = 2
  density = 1
  expand = 3
  formula = G4_BRASS
  name = G4_BRASS
  specific = 4
FEATURE [App::DocumentObjectGroupPython] Cu_element003  label="Cu_element : 89"  # scripted group (container) (typed FeaturePython)
  n = 89
  ref = Cu_element
FEATURE [App::DocumentObjectGroupPython] Zn_element003  label="Zn_element : 9"  # scripted group (container) (typed FeaturePython)
  n = 9
  ref = Zn_element
FEATURE [App::DocumentObjectGroupPython] Pb_element006  label="Pb_element : 2"  # scripted group (container) (typed FeaturePython)
  n = 2
  ref = Pb_element
FEATURE [App::DocumentObjectGroupPython] G4_BRONZE  # scripted group (container) (typed FeaturePython)
  Dunit = g/cm3
  Dvalue = 8.82
  Group = -> [Cu_element003,Zn_element003,Pb_element006]
  conduct = 2
  density = 1
  expand = 3
  formula = G4_BRONZE
  name = G4_BRONZE
  specific = 4
FEATURE [App::DocumentObjectGroupPython] Fe_element008  label="Fe_element : 74"  # scripted group (container) (typed FeaturePython)
  n = 74
  ref = Fe_element
FEATURE [App::DocumentObjectGroupPython] Cr_element002  label="Cr_element : 18"  # scripted group (container) (typed FeaturePython)
  n = 18
  ref = Cr_element
FEATURE [App::DocumentObjectGroupPython] Ni_element002  label="Ni_element : 8"  # scripted group (container) (typed FeaturePython)
  n = 8
  ref = Ni_element
FEATURE [App::DocumentObjectGroupPython] G4_STAINLESS_STEEL  label="G4_STAINLESS-STEEL"  # scripted group (container) (typed FeaturePython)
  Dunit = g/cm3
  Dvalue = 8
  Group = -> [Fe_element008,Cr_element002,Ni_element002]
  conduct = 2
  density = 1
  expand = 3
  formula = G4_STAINLESS-STEEL
  name = G4_STAINLESS-STEEL
  specific = 4
FEATURE [App::DocumentObjectGroupPython] H_element116  label="H_element : 064"  # scripted group (container) (typed FeaturePython)
  n = 18
  ref = H_element
FEATURE [App::DocumentObjectGroupPython] C_element126  label="C_element : 071"  # scripted group (container) (typed FeaturePython)
  n = 12
  ref = C_element
FEATURE [App::DocumentObjectGroupPython] O_element109  label="O_element : 062"  # scripted group (container) (typed FeaturePython)
  n = 7
  ref = O_element
FEATURE [App::DocumentObjectGroupPython] G4_CR39  # scripted group (container) (typed FeaturePython)
  Dunit = g/cm3
  Dvalue = 1.32
  Group = -> [H_element116,C_element126,O_element109]
  conduct = 2
  density = 1
  expand = 3
  formula = G4_CR39
  name = G4_CR39
  specific = 4
FEATURE [App::DocumentObjectGroupPython] H_element117  label="H_element : 38"  # scripted group (container) (typed FeaturePython)
  n = 38
  ref = H_element
FEATURE [App::DocumentObjectGroupPython] C_element127  label="C_element : 072"  # scripted group (container) (typed FeaturePython)
  n = 18
  ref = C_element
FEATURE [App::DocumentObjectGroupPython] O_element110  label="O_element : 063"  # scripted group (container) (typed FeaturePython)
  n = 1
  ref = O_element
FEATURE [App::DocumentObjectGroupPython] G4_OCTADECANOL  # scripted group (container) (typed FeaturePython)
  Dunit = g/cm3
  Dvalue = 0.812
  Group = -> [H_element117,C_element127,O_element110]
  conduct = 2
  density = 1
  expand = 3
  formula = G4_OCTADECANOL
  name = G4_OCTADECANOL
  specific = 4
FEATURE [App::DocumentObjectGroupPython] HEP  # scripted group (container) (typed FeaturePython)
  Group = -> [G4_lH2,G4_lN2,G4_lO2,G4_lAr,G4_lBr,G4_lKr,G4_lXe,G4_PbWO4,G4_Galactic,G4_GRAPHITE_POROUS,G4_LUCITE,G4_BRASS,G4_BRONZE,G4_STAINLESS_STEEL,G4_CR39,G4_OCTADECANOL]
FEATURE [App::DocumentObjectGroupPython] C_element128  label="C_element : 073"  # scripted group (container) (typed FeaturePython)
  n = 14
  ref = C_element
FEATURE [App::DocumentObjectGroupPython] H_element118  label="H_element : 065"  # scripted group (container) (typed FeaturePython)
  n = 10
  ref = H_element
FEATURE [App::DocumentObjectGroupPython] O_element111  label="O_element : 064"  # scripted group (container) (typed FeaturePython)
  n = 2
  ref = O_element
FEATURE [App::DocumentObjectGroupPython] N_element050  label="N_element : 023"  # scripted group (container) (typed FeaturePython)
  n = 2
  ref = N_element
FEATURE [App::DocumentObjectGroupPython] G4_KEVLAR  # scripted group (container) (typed FeaturePython)
  Dunit = g/cm3
  Dvalue = 1.44
  Group = -> [C_element128,H_element118,O_element111,N_element050]
  conduct = 2
  density = 1
  expand = 3
  formula = G4_KEVLAR
  name = G4_KEVLAR
  specific = 4
FEATURE [App::DocumentObjectGroupPython] C_element129  label="C_element : 074"  # scripted group (container) (typed FeaturePython)
  n = 10
  ref = C_element
FEATURE [App::DocumentObjectGroupPython] H_element119  label="H_element : 066"  # scripted group (container) (typed FeaturePython)
  n = 8
  ref = H_element
FEATURE [App::DocumentObjectGroupPython] O_element112  label="O_element : 065"  # scripted group (container) (typed FeaturePython)
  n = 4
  ref = O_element
FEATURE [App::DocumentObjectGroupPython] G4_DACRON  # scripted group (container) (typed FeaturePython)
  Dunit = g/cm3
  Dvalue = 1.4
  Group = -> [C_element129,H_element119,O_element112]
  conduct = 2
  density = 1
  expand = 3
  formula = G4_DACRON
  name = G4_DACRON
  specific = 4
FEATURE [App::DocumentObjectGroupPython] C_element130  label="C_element : 075"  # scripted group (container) (typed FeaturePython)
  n = 4
  ref = C_element
FEATURE [App::DocumentObjectGroupPython] H_element120  label="H_element : 067"  # scripted group (container) (typed FeaturePython)
  n = 5
  ref = H_element
FEATURE [App::DocumentObjectGroupPython] Cl_element030  label="Cl_element : 016"  # scripted group (container) (typed FeaturePython)
  n = 1
  ref = Cl_element
FEATURE [App::DocumentObjectGroupPython] G4_NEOPRENE  # scripted group (container) (typed FeaturePython)
  Dunit = g/cm3
  Dvalue = 1.23
  Group = -> [C_element130,H_element120,Cl_element030]
  conduct = 2
  density = 1
  expand = 3
  formula = G4_NEOPRENE
  name = G4_NEOPRENE
  specific = 4
FEATURE [App::DocumentObjectGroupPython] Space  # scripted group (container) (typed FeaturePython)
  Group = -> [G4_KEVLAR,G4_DACRON,G4_NEOPRENE]
FEATURE [App::DocumentObjectGroupPython] H_element121  label="H_element : 068"  # scripted group (container) (typed FeaturePython)
  n = 5
  ref = H_element
FEATURE [App::DocumentObjectGroupPython] C_element131  label="C_element : 076"  # scripted group (container) (typed FeaturePython)
  n = 4
  ref = C_element
FEATURE [App::DocumentObjectGroupPython] N_element051  label="N_element : 3"  # scripted group (container) (typed FeaturePython)
  n = 3
  ref = N_element
FEATURE [App::DocumentObjectGroupPython] O_element113  label="O_element : 066"  # scripted group (container) (typed FeaturePython)
  n = 1
  ref = O_element
FEATURE [App::DocumentObjectGroupPython] G4_CYTOSINE  # scripted group (container) (typed FeaturePython)
  Dunit = g/cm3
  Dvalue = 1.55
  Group = -> [H_element121,C_element131,N_element051,O_element113]
  conduct = 2
  density = 1
  expand = 3
  formula = G4_CYTOSINE
  name = G4_CYTOSINE
  specific = 4
FEATURE [App::DocumentObjectGroupPython] H_element122  label="H_element : 069"  # scripted group (container) (typed FeaturePython)
  n = 6
  ref = H_element
FEATURE [App::DocumentObjectGroupPython] C_element132  label="C_element : 077"  # scripted group (container) (typed FeaturePython)
  n = 5
  ref = C_element
FEATURE [App::DocumentObjectGroupPython] N_element052  label="N_element : 024"  # scripted group (container) (typed FeaturePython)
  n = 2
  ref = N_element
FEATURE [App::DocumentObjectGroupPython] O_element114  label="O_element : 067"  # scripted group (container) (typed FeaturePython)
  n = 2
  ref = O_element
FEATURE [App::DocumentObjectGroupPython] G4_THYMINE  # scripted group (container) (typed FeaturePython)
  Dunit = g/cm3
  Dvalue = 1.23
  Group = -> [H_element122,C_element132,N_element052,O_element114]
  conduct = 2
  density = 1
  expand = 3
  formula = G4_THYMINE
  name = G4_THYMINE
  specific = 4
FEATURE [App::DocumentObjectGroupPython] H_element123  label="H_element : 070"  # scripted group (container) (typed FeaturePython)
  n = 4
  ref = H_element
FEATURE [App::DocumentObjectGroupPython] C_element133  label="C_element : 078"  # scripted group (container) (typed FeaturePython)
  n = 4
  ref = C_element
FEATURE [App::DocumentObjectGroupPython] N_element053  label="N_element : 025"  # scripted group (container) (typed FeaturePython)
  n = 2
  ref = N_element
FEATURE [App::DocumentObjectGroupPython] O_element115  label="O_element : 068"  # scripted group (container) (typed FeaturePython)
  n = 2
  ref = O_element
FEATURE [App::DocumentObjectGroupPython] G4_URACIL  # scripted group (container) (typed FeaturePython)
  Dunit = g/cm3
  Dvalue = 1.32
  Group = -> [H_element123,C_element133,N_element053,O_element115]
  conduct = 2
  density = 1
  expand = 3
  formula = G4_URACIL
  name = G4_URACIL
  specific = 4
FEATURE [App::DocumentObjectGroupPython] H_element124  label="H_element : 071"  # scripted group (container) (typed FeaturePython)
  n = 4
  ref = H_element
FEATURE [App::DocumentObjectGroupPython] C_element134  label="C_element : 079"  # scripted group (container) (typed FeaturePython)
  n = 5
  ref = C_element
FEATURE [App::DocumentObjectGroupPython] N_element054  label="N_element : 026"  # scripted group (container) (typed FeaturePython)
  n = 5
  ref = N_element
FEATURE [App::DocumentObjectGroupPython] G4_DNA_ADENINE  # scripted group (container) (typed FeaturePython)
  Dunit = g/cm3
  Dvalue = 1
  Group = -> [H_element124,C_element134,N_element054]
  conduct = 2
  density = 1
  expand = 3
  formula = G4_DNA_ADENINE
  name = G4_DNA_ADENINE
  specific = 4
FEATURE [App::DocumentObjectGroupPython] H_element125  label="H_element : 072"  # scripted group (container) (typed FeaturePython)
  n = 4
  ref = H_element
FEATURE [App::DocumentObjectGroupPython] C_element135  label="C_element : 080"  # scripted group (container) (typed FeaturePython)
  n = 5
  ref = C_element
FEATURE [App::DocumentObjectGroupPython] N_element055  label="N_element : 027"  # scripted group (container) (typed FeaturePython)
  n = 5
  ref = N_element
FEATURE [App::DocumentObjectGroupPython] O_element116  label="O_element : 069"  # scripted group (container) (typed FeaturePython)
  n = 1
  ref = O_element
FEATURE [App::DocumentObjectGroupPython] G4_DNA_GUANINE  # scripted group (container) (typed FeaturePython)
  Dunit = g/cm3
  Dvalue = 1
  Group = -> [H_element125,C_element135,N_element055,O_element116]
  conduct = 2
  density = 1
  expand = 3
  formula = G4_DNA_GUANINE
  name = G4_DNA_GUANINE
  specific = 4
FEATURE [App::DocumentObjectGroupPython] H_element126  label="H_element : 073"  # scripted group (container) (typed FeaturePython)
  n = 4
  ref = H_element
FEATURE [App::DocumentObjectGroupPython] C_element136  label="C_element : 081"  # scripted group (container) (typed FeaturePython)
  n = 4
  ref = C_element
FEATURE [App::DocumentObjectGroupPython] N_element056  label="N_element : 028"  # scripted group (container) (typed FeaturePython)
  n = 3
  ref = N_element
FEATURE [App::DocumentObjectGroupPython] O_element117  label="O_element : 070"  # scripted group (container) (typed FeaturePython)
  n = 1
  ref = O_element
FEATURE [App::DocumentObjectGroupPython] G4_DNA_CYTOSINE  # scripted group (container) (typed FeaturePython)
  Dunit = g/cm3
  Dvalue = 1
  Group = -> [H_element126,C_element136,N_element056,O_element117]
  conduct = 2
  density = 1
  expand = 3
  formula = G4_DNA_CYTOSINE
  name = G4_DNA_CYTOSINE
  specific = 4
FEATURE [App::DocumentObjectGroupPython] H_element127  label="H_element : 074"  # scripted group (container) (typed FeaturePython)
  n = 5
  ref = H_element
FEATURE [App::DocumentObjectGroupPython] C_element137  label="C_element : 082"  # scripted group (container) (typed FeaturePython)
  n = 5
  ref = C_element
FEATURE [App::DocumentObjectGroupPython] N_element057  label="N_element : 029"  # scripted group (container) (typed FeaturePython)
  n = 2
  ref = N_element
FEATURE [App::DocumentObjectGroupPython] O_element118  label="O_element : 071"  # scripted group (container) (typed FeaturePython)
  n = 2
  ref = O_element
FEATURE [App::DocumentObjectGroupPython] G4_DNA_THYMINE  # scripted group (container) (typed FeaturePython)
  Dunit = g/cm3
  Dvalue = 1
  Group = -> [H_element127,C_element137,N_element057,O_element118]
  conduct = 2
  density = 1
  expand = 3
  formula = G4_DNA_THYMINE
  name = G4_DNA_THYMINE
  specific = 4
FEATURE [App::DocumentObjectGroupPython] H_element128  label="H_element : 075"  # scripted group (container) (typed FeaturePython)
  n = 3
  ref = H_element
FEATURE [App::DocumentObjectGroupPython] C_element138  label="C_element : 083"  # scripted group (container) (typed FeaturePython)
  n = 4
  ref = C_element
FEATURE [App::DocumentObjectGroupPython] N_element058  label="N_element : 030"  # scripted group (container) (typed FeaturePython)
  n = 2
  ref = N_element
FEATURE [App::DocumentObjectGroupPython] O_element119  label="O_element : 072"  # scripted group (container) (typed FeaturePython)
  n = 2
  ref = O_element
FEATURE [App::DocumentObjectGroupPython] G4_DNA_URACIL  # scripted group (container) (typed FeaturePython)
  Dunit = g/cm3
  Dvalue = 1
  Group = -> [H_element128,C_element138,N_element058,O_element119]
  conduct = 2
  density = 1
  expand = 3
  formula = G4_DNA_URACIL
  name = G4_DNA_URACIL
  specific = 4
FEATURE [App::DocumentObjectGroupPython] H_element129  label="H_element : 076"  # scripted group (container) (typed FeaturePython)
  n = 10
  ref = H_element
FEATURE [App::DocumentObjectGroupPython] C_element139  label="C_element : 084"  # scripted group (container) (typed FeaturePython)
  n = 10
  ref = C_element
FEATURE [App::DocumentObjectGroupPython] N_element059  label="N_element : 031"  # scripted group (container) (typed FeaturePython)
  n = 5
  ref = N_element
FEATURE [App::DocumentObjectGroupPython] O_element120  label="O_element : 073"  # scripted group (container) (typed FeaturePython)
  n = 4
  ref = O_element
FEATURE [App::DocumentObjectGroupPython] G4_DNA_ADENOSINE  # scripted group (container) (typed FeaturePython)
  Dunit = g/cm3
  Dvalue = 1
  Group = -> [H_element129,C_element139,N_element059,O_element120]
  conduct = 2
  density = 1
  expand = 3
  formula = G4_DNA_ADENOSINE
  name = G4_DNA_ADENOSINE
  specific = 4
FEATURE [App::DocumentObjectGroupPython] H_element130  label="H_element : 077"  # scripted group (container) (typed FeaturePython)
  n = 10
  ref = H_element
FEATURE [App::DocumentObjectGroupPython] C_element140  label="C_element : 085"  # scripted group (container) (typed FeaturePython)
  n = 10
  ref = C_element
FEATURE [App::DocumentObjectGroupPython] N_element060  label="N_element : 032"  # scripted group (container) (typed FeaturePython)
  n = 5
  ref = N_element
FEATURE [App::DocumentObjectGroupPython] O_element121  label="O_element : 074"  # scripted group (container) (typed FeaturePython)
  n = 5
  ref = O_element
FEATURE [App::DocumentObjectGroupPython] G4_DNA_GUANOSINE  # scripted group (container) (typed FeaturePython)
  Dunit = g/cm3
  Dvalue = 1
  Group = -> [H_element130,C_element140,N_element060,O_element121]
  conduct = 2
  density = 1
  expand = 3
  formula = G4_DNA_GUANOSINE
  name = G4_DNA_GUANOSINE
  specific = 4
FEATURE [App::DocumentObjectGroupPython] H_element131  label="H_element : 078"  # scripted group (container) (typed FeaturePython)
  n = 10
  ref = H_element
FEATURE [App::DocumentObjectGroupPython] C_element141  label="C_element : 086"  # scripted group (container) (typed FeaturePython)
  n = 9
  ref = C_element
FEATURE [App::DocumentObjectGroupPython] N_element061  label="N_element : 033"  # scripted group (container) (typed FeaturePython)
  n = 3
  ref = N_element
FEATURE [App::DocumentObjectGroupPython] O_element122  label="O_element : 075"  # scripted group (container) (typed FeaturePython)
  n = 5
  ref = O_element
FEATURE [App::DocumentObjectGroupPython] G4_DNA_CYTIDINE  # scripted group (container) (typed FeaturePython)
  Dunit = g/cm3
  Dvalue = 1
  Group = -> [H_element131,C_element141,N_element061,O_element122]
  conduct = 2
  density = 1
  expand = 3
  formula = G4_DNA_CYTIDINE
  name = G4_DNA_CYTIDINE
  specific = 4
FEATURE [App::DocumentObjectGroupPython] H_element132  label="H_element : 079"  # scripted group (container) (typed FeaturePython)
  n = 9
  ref = H_element
FEATURE [App::DocumentObjectGroupPython] C_element142  label="C_element : 087"  # scripted group (container) (typed FeaturePython)
  n = 9
  ref = C_element
FEATURE [App::DocumentObjectGroupPython] N_element062  label="N_element : 034"  # scripted group (container) (typed FeaturePython)
  n = 2
  ref = N_element
FEATURE [App::DocumentObjectGroupPython] O_element123  label="O_element : 076"  # scripted group (container) (typed FeaturePython)
  n = 6
  ref = O_element
FEATURE [App::DocumentObjectGroupPython] G4_DNA_URIDINE  # scripted group (container) (typed FeaturePython)
  Dunit = g/cm3
  Dvalue = 1
  Group = -> [H_element132,C_element142,N_element062,O_element123]
  conduct = 2
  density = 1
  expand = 3
  formula = G4_DNA_URIDINE
  name = G4_DNA_URIDINE
  specific = 4
FEATURE [App::DocumentObjectGroupPython] H_element133  label="H_element : 080"  # scripted group (container) (typed FeaturePython)
  n = 11
  ref = H_element
FEATURE [App::DocumentObjectGroupPython] C_element143  label="C_element : 088"  # scripted group (container) (typed FeaturePython)
  n = 10
  ref = C_element
FEATURE [App::DocumentObjectGroupPython] N_element063  label="N_element : 035"  # scripted group (container) (typed FeaturePython)
  n = 2
  ref = N_element
FEATURE [App::DocumentObjectGroupPython] O_element124  label="O_element : 077"  # scripted group (container) (typed FeaturePython)
  n = 6
  ref = O_element
FEATURE [App::DocumentObjectGroupPython] G4_DNA_METHYLURIDINE  # scripted group (container) (typed FeaturePython)
  Dunit = g/cm3
  Dvalue = 1
  Group = -> [H_element133,C_element143,N_element063,O_element124]
  conduct = 2
  density = 1
  expand = 3
  formula = G4_DNA_METHYLURIDINE
  name = G4_DNA_METHYLURIDINE
  specific = 4
FEATURE [App::DocumentObjectGroupPython] P_element014  label="P_element : 003"  # scripted group (container) (typed FeaturePython)
  n = 1
  ref = P_element
FEATURE [App::DocumentObjectGroupPython] O_element125  label="O_element : 078"  # scripted group (container) (typed FeaturePython)
  n = 3
  ref = O_element
FEATURE [App::DocumentObjectGroupPython] G4_DNA_MONOPHOSPHATE  # scripted group (container) (typed FeaturePython)
  Dunit = g/cm3
  Dvalue = 1
  Group = -> [P_element014,O_element125]
  conduct = 2
  density = 1
  expand = 3
  formula = G4_DNA_MONOPHOSPHATE
  name = G4_DNA_MONOPHOSPHATE
  specific = 4
FEATURE [App::DocumentObjectGroupPython] H_element134  label="H_element : 081"  # scripted group (container) (typed FeaturePython)
  n = 10
  ref = H_element
FEATURE [App::DocumentObjectGroupPython] C_element144  label="C_element : 089"  # scripted group (container) (typed FeaturePython)
  n = 10
  ref = C_element
FEATURE [App::DocumentObjectGroupPython] N_element064  label="N_element : 036"  # scripted group (container) (typed FeaturePython)
  n = 5
  ref = N_element
FEATURE [App::DocumentObjectGroupPython] O_element126  label="O_element : 079"  # scripted group (container) (typed FeaturePython)
  n = 7
  ref = O_element
FEATURE [App::DocumentObjectGroupPython] P_element015  label="P_element : 004"  # scripted group (container) (typed FeaturePython)
  n = 1
  ref = P_element
FEATURE [App::DocumentObjectGroupPython] G4_DNA_A  # scripted group (container) (typed FeaturePython)
  Dunit = g/cm3
  Dvalue = 1
  Group = -> [H_element134,C_element144,N_element064,O_element126,P_element015]
  conduct = 2
  density = 1
  expand = 3
  formula = G4_DNA_A
  name = G4_DNA_A
  specific = 4
FEATURE [App::DocumentObjectGroupPython] H_element135  label="H_element : 082"  # scripted group (container) (typed FeaturePython)
  n = 10
  ref = H_element
FEATURE [App::DocumentObjectGroupPython] C_element145  label="C_element : 090"  # scripted group (container) (typed FeaturePython)
  n = 10
  ref = C_element
FEATURE [App::DocumentObjectGroupPython] N_element065  label="N_element : 037"  # scripted group (container) (typed FeaturePython)
  n = 5
  ref = N_element
FEATURE [App::DocumentObjectGroupPython] O_element127  label="O_element : 8"  # scripted group (container) (typed FeaturePython)
  n = 8
  ref = O_element
FEATURE [App::DocumentObjectGroupPython] P_element016  label="P_element : 005"  # scripted group (container) (typed FeaturePython)
  n = 1
  ref = P_element
FEATURE [App::DocumentObjectGroupPython] G4_DNA_G  # scripted group (container) (typed FeaturePython)
  Dunit = g/cm3
  Dvalue = 1
  Group = -> [H_element135,C_element145,N_element065,O_element127,P_element016]
  conduct = 2
  density = 1
  expand = 3
  formula = G4_DNA_G
  name = G4_DNA_G
  specific = 4
FEATURE [App::DocumentObjectGroupPython] H_element136  label="H_element : 083"  # scripted group (container) (typed FeaturePython)
  n = 10
  ref = H_element
FEATURE [App::DocumentObjectGroupPython] C_element146  label="C_element : 091"  # scripted group (container) (typed FeaturePython)
  n = 9
  ref = C_element
FEATURE [App::DocumentObjectGroupPython] N_element066  label="N_element : 038"  # scripted group (container) (typed FeaturePython)
  n = 3
  ref = N_element
FEATURE [App::DocumentObjectGroupPython] O_element128  label="O_element : 080"  # scripted group (container) (typed FeaturePython)
  n = 8
  ref = O_element
FEATURE [App::DocumentObjectGroupPython] P_element017  label="P_element : 006"  # scripted group (container) (typed FeaturePython)
  n = 1
  ref = P_element
FEATURE [App::DocumentObjectGroupPython] G4_DNA_C  # scripted group (container) (typed FeaturePython)
  Dunit = g/cm3
  Dvalue = 1
  Group = -> [H_element136,C_element146,N_element066,O_element128,P_element017]
  conduct = 2
  density = 1
  expand = 3
  formula = G4_DNA_C
  name = G4_DNA_C
  specific = 4
FEATURE [App::DocumentObjectGroupPython] H_element137  label="H_element : 084"  # scripted group (container) (typed FeaturePython)
  n = 9
  ref = H_element
FEATURE [App::DocumentObjectGroupPython] C_element147  label="C_element : 092"  # scripted group (container) (typed FeaturePython)
  n = 9
  ref = C_element
FEATURE [App::DocumentObjectGroupPython] N_element067  label="N_element : 039"  # scripted group (container) (typed FeaturePython)
  n = 2
  ref = N_element
FEATURE [App::DocumentObjectGroupPython] O_element129  label="O_element : 9"  # scripted group (container) (typed FeaturePython)
  n = 9
  ref = O_element
FEATURE [App::DocumentObjectGroupPython] P_element018  label="P_element : 007"  # scripted group (container) (typed FeaturePython)
  n = 1
  ref = P_element
FEATURE [App::DocumentObjectGroupPython] G4_DNA_U  # scripted group (container) (typed FeaturePython)
  Dunit = g/cm3
  Dvalue = 1
  Group = -> [H_element137,C_element147,N_element067,O_element129,P_element018]
  conduct = 2
  density = 1
  expand = 3
  formula = G4_DNA_U
  name = G4_DNA_U
  specific = 4
FEATURE [App::DocumentObjectGroupPython] H_element138  label="H_element : 085"  # scripted group (container) (typed FeaturePython)
  n = 11
  ref = H_element
FEATURE [App::DocumentObjectGroupPython] C_element148  label="C_element : 093"  # scripted group (container) (typed FeaturePython)
  n = 10
  ref = C_element
FEATURE [App::DocumentObjectGroupPython] N_element068  label="N_element : 040"  # scripted group (container) (typed FeaturePython)
  n = 2
  ref = N_element
FEATURE [App::DocumentObjectGroupPython] O_element130  label="O_element : 081"  # scripted group (container) (typed FeaturePython)
  n = 9
  ref = O_element
FEATURE [App::DocumentObjectGroupPython] P_element019  label="P_element : 008"  # scripted group (container) (typed FeaturePython)
  n = 1
  ref = P_element
FEATURE [App::DocumentObjectGroupPython] G4_DNA_MU  # scripted group (container) (typed FeaturePython)
  Dunit = g/cm3
  Dvalue = 1
  Group = -> [H_element138,C_element148,N_element068,O_element130,P_element019]
  conduct = 2
  density = 1
  expand = 3
  formula = G4_DNA_MU
  name = G4_DNA_MU
  specific = 4
FEATURE [App::DocumentObjectGroupPython] BioChemical  # scripted group (container) (typed FeaturePython)
  Group = -> [G4_CYTOSINE,G4_THYMINE,G4_URACIL,G4_DNA_ADENINE,G4_DNA_GUANINE,G4_DNA_CYTOSINE,G4_DNA_THYMINE,G4_DNA_URACIL,G4_DNA_ADENOSINE,G4_DNA_GUANOSINE,G4_DNA_CYTIDINE,G4_DNA_URIDINE,G4_DNA_METHYLURIDINE,G4_DNA_MONOPHOSPHATE,G4_DNA_A,G4_DNA_G,G4_DNA_C,G4_DNA_U,G4_DNA_MU]
FEATURE [App::DocumentObjectGroupPython] G4Materials  # scripted group (container) (typed FeaturePython)
  Group = -> [NIST,Element,HEP,Space,BioChemical]
  version = 1
FEATURE [App::DocumentObjectGroupPython] Geant4  # scripted group (container) (typed FeaturePython)
  Group = -> [G4Isotopes,G4Elements,G4Materials]
FEATURE [App::DocumentObjectGroupPython] Materials  # scripted group (container) (typed FeaturePython)
  Group = -> [Geant4]
FEATURE [Part::FeaturePython] GDMLBox_WorldBox  # WARN: FeaturePython — macro-defined, semantics opaque (R4)
  lunit = 2
  material = 5
  x = 200
  y = 200
  z = 200
FEATURE [Sketcher::SketchObject] Sketch
  FullyConstrained = false
  sketch-geometry (5):
    g0: ArcOfHyperbola CenterX=-23.607 CenterY=7.125 CenterZ=0 NormalX=0 NormalY=0 NormalZ=1 MajorRadius=20.1608 MinorRadius=14.3903 AngleXU=-0.133002 StartAngle=-1.4336 EndAngle=1.4079
    g1: LineSegment StartX=-3.62428 StartY=4.45146 StartZ=0 EndX=-43.5897 EndY=9.79853 EndZ=0
    g2: LineSegment StartX=-1.71598 StartY=18.7146 StartZ=0 EndX=-5.53258 EndY=-9.81171 EndZ=0
    g3: GeomPoint X=0.943907 Y=3.84028 Z=0
    g4: LineSegment StartX=23.3422 StartY=28.7386 StartZ=0 EndX=16.9028 EndY=-27.0075 EndZ=0
  constraints (5):
    c: InternalAlignment(g1,g0)
    c: InternalAlignment(g2,g0)
    c: InternalAlignment(g3,g0)
    c: Coincident(g4,g0)
    c: Coincident(g4,g0)
FEATURE [Part::Extrusion] Extrude
  Base = -> Sketch
  Dir = (0,0,1)
  DirMode = 2
  FaceMakerClass = Part::FaceMakerBullseye
  LengthFwd = 10
  LengthRev = 0
  Solid = true
  Symmetric = false
FEATURE [App::Part] Part
  Group = -> [Sketch,Extrude]
  Origin = -> Origin001
  material = 5
FEATURE [App::Part] worldVOL
  Group = -> [GDMLBox_WorldBox,Part]
  Origin = -> Origin
